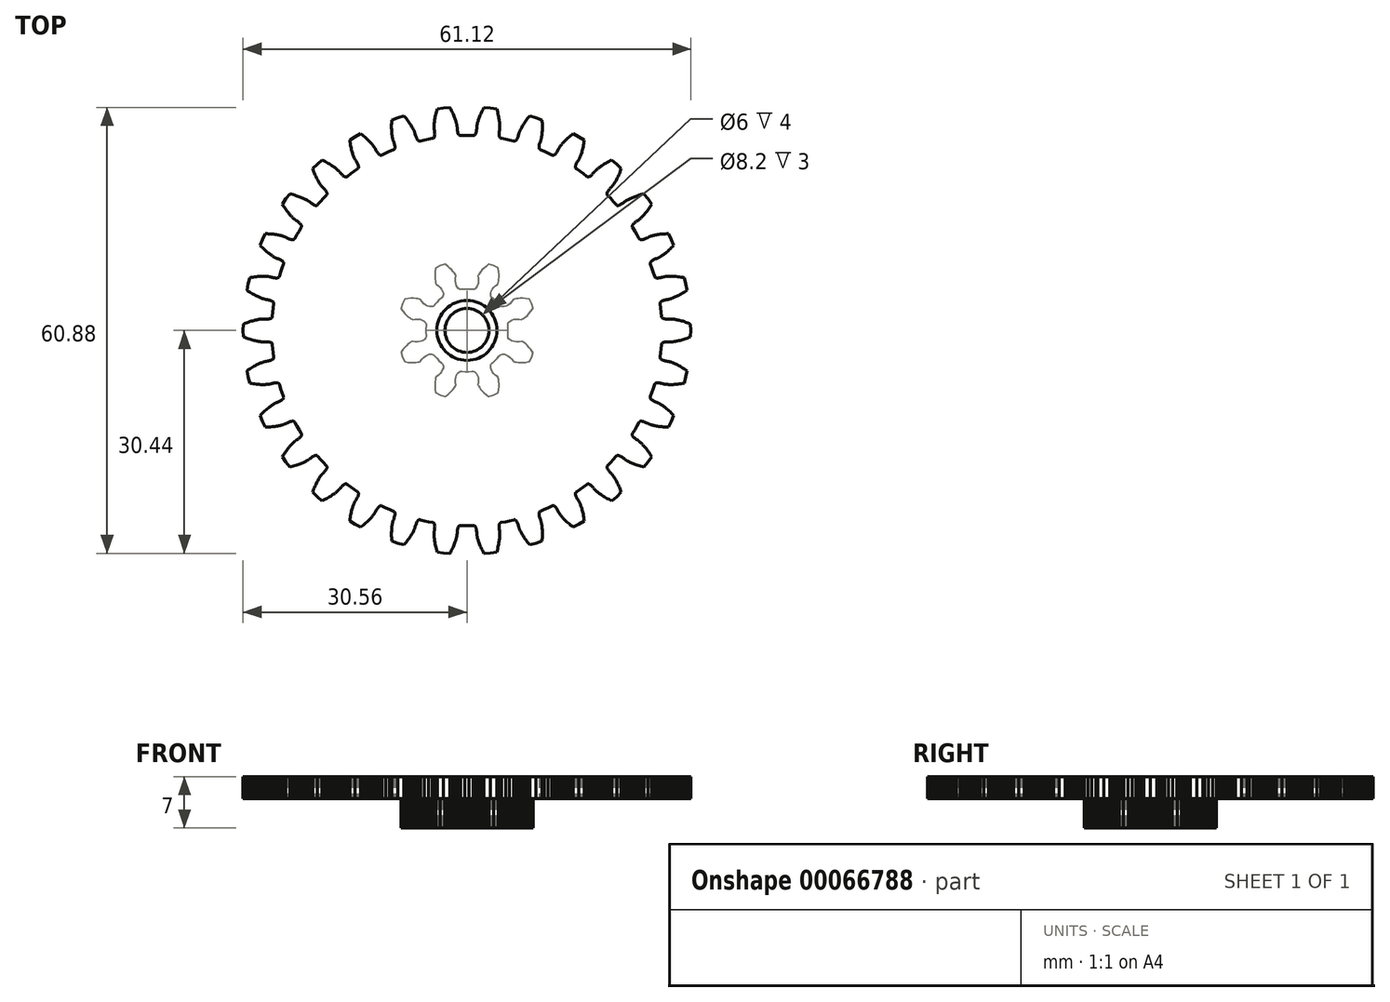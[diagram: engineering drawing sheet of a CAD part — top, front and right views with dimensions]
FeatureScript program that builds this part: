
annotation { "Feature Type Name" : "Feature", "Feature Type Description" : "" }
export const myFeature = defineFeature(function(context is Context, id is Id, definition is map)
    precondition{}
    {
        {
            var Q0;
            Q0=qCreatedBy(makeId("Top.planeOp"),FACE);
            var sketch = newSketch(context, id + "F0", { "sketchPlane" : qUnion([Q0])});
            skCircle(sketch, "E0", {"center": v(0, 0) * mm, "radius": 3 * mm});
            skLineSegment(sketch, "E1", {"start": v(-8.5, 4.26) * mm, "end": v(-8.82, 3.65) * mm});
            skLineSegment(sketch, "E2", {"start": v(-8.82, 3.65) * mm, "end": v(-9.02, 3) * mm});
            skLineSegment(sketch, "E3", {"start": v(-9.02, 3) * mm, "end": v(-9, 2.97) * mm});
            skLineSegment(sketch, "E4", {"start": v(-9, 2.97) * mm, "end": v(-8.75, 2.6) * mm});
            skLineSegment(sketch, "E5", {"start": v(-8.75, 2.6) * mm, "end": v(-8.5, 2.3) * mm});
            skLineSegment(sketch, "E6", {"start": v(-8.5, 2.3) * mm, "end": v(-8.25, 2.06) * mm});
            skLineSegment(sketch, "E7", {"start": v(-8.25, 2.06) * mm, "end": v(-8.02, 1.86) * mm});
            skLineSegment(sketch, "E8", {"start": v(-8.02, 1.86) * mm, "end": v(-7.81, 1.7) * mm});
            skLineSegment(sketch, "E9", {"start": v(-7.81, 1.7) * mm, "end": v(-7.63, 1.59) * mm});
            skLineSegment(sketch, "E10", {"start": v(-7.63, 1.59) * mm, "end": v(-7.48, 1.51) * mm});
            skLineSegment(sketch, "E11", {"start": v(-7.48, 1.51) * mm, "end": v(-7.43, 1.5) * mm});
            skLineSegment(sketch, "E12", {"start": v(-7.43, 1.5) * mm, "end": v(-7.11, 1.56) * mm});
            skLineSegment(sketch, "E13", {"start": v(-7.11, 1.56) * mm, "end": v(-6.74, 1.56) * mm});
            skLineSegment(sketch, "E14", {"start": v(-6.74, 1.56) * mm, "end": v(-6.41, 1.52) * mm});
            skLineSegment(sketch, "E15", {"start": v(-6.41, 1.52) * mm, "end": v(-6.13, 1.43) * mm});
            skLineSegment(sketch, "E16", {"start": v(-6.13, 1.43) * mm, "end": v(-5.9, 1.31) * mm});
            skLineSegment(sketch, "E17", {"start": v(-5.9, 1.31) * mm, "end": v(-5.74, 1.18) * mm});
            skLineSegment(sketch, "E18", {"start": v(-5.74, 1.18) * mm, "end": v(-5.63, 1.02) * mm});
            skLineSegment(sketch, "E19", {"start": v(-5.63, 1.02) * mm, "end": v(-5.58, 0.86) * mm});
            skLineSegment(sketch, "E20", {"start": v(-5.58, 0.86) * mm, "end": v(-5.59, 0.7) * mm});
            skLineSegment(sketch, "E21", {"start": v(-5.59, 0.7) * mm, "end": v(-5.6, 0.66) * mm});
            skLineSegment(sketch, "E22", {"start": v(-5.6, 0.66) * mm, "end": v(-5.63, 0.22) * mm});
            skLineSegment(sketch, "E23", {"start": v(-5.63, 0.22) * mm, "end": v(-5.63, -0.22) * mm});
            skLineSegment(sketch, "E24", {"start": v(-5.63, -0.22) * mm, "end": v(-5.6, -0.66) * mm});
            skLineSegment(sketch, "E25", {"start": v(-5.6, -0.66) * mm, "end": v(-5.59, -0.7) * mm});
            skLineSegment(sketch, "E26", {"start": v(-5.59, -0.7) * mm, "end": v(-5.58, -0.86) * mm});
            skLineSegment(sketch, "E27", {"start": v(-5.58, -0.86) * mm, "end": v(-5.63, -1.02) * mm});
            skLineSegment(sketch, "E28", {"start": v(-5.63, -1.02) * mm, "end": v(-5.74, -1.18) * mm});
            skLineSegment(sketch, "E29", {"start": v(-5.74, -1.18) * mm, "end": v(-5.9, -1.31) * mm});
            skLineSegment(sketch, "E30", {"start": v(-5.9, -1.31) * mm, "end": v(-6.13, -1.43) * mm});
            skLineSegment(sketch, "E31", {"start": v(-6.13, -1.43) * mm, "end": v(-6.41, -1.52) * mm});
            skLineSegment(sketch, "E32", {"start": v(-6.41, -1.52) * mm, "end": v(-6.74, -1.56) * mm});
            skLineSegment(sketch, "E33", {"start": v(-6.74, -1.56) * mm, "end": v(-7.11, -1.56) * mm});
            skLineSegment(sketch, "E34", {"start": v(-7.11, -1.56) * mm, "end": v(-7.43, -1.5) * mm});
            skLineSegment(sketch, "E35", {"start": v(-7.43, -1.5) * mm, "end": v(-7.48, -1.51) * mm});
            skLineSegment(sketch, "E36", {"start": v(-7.48, -1.51) * mm, "end": v(-7.63, -1.59) * mm});
            skLineSegment(sketch, "E37", {"start": v(-7.63, -1.59) * mm, "end": v(-7.81, -1.7) * mm});
            skLineSegment(sketch, "E38", {"start": v(-7.81, -1.7) * mm, "end": v(-8.02, -1.86) * mm});
            skLineSegment(sketch, "E39", {"start": v(-8.02, -1.86) * mm, "end": v(-8.25, -2.06) * mm});
            skLineSegment(sketch, "E40", {"start": v(-8.25, -2.06) * mm, "end": v(-8.5, -2.3) * mm});
            skLineSegment(sketch, "E41", {"start": v(-8.5, -2.3) * mm, "end": v(-8.75, -2.6) * mm});
            skLineSegment(sketch, "E42", {"start": v(-8.75, -2.6) * mm, "end": v(-9, -2.97) * mm});
            skLineSegment(sketch, "E43", {"start": v(-9, -2.97) * mm, "end": v(-9.02, -3) * mm});
            skLineSegment(sketch, "E44", {"start": v(-9.02, -3) * mm, "end": v(-8.82, -3.65) * mm});
            skLineSegment(sketch, "E45", {"start": v(-8.82, -3.65) * mm, "end": v(-8.5, -4.26) * mm});
            skLineSegment(sketch, "E46", {"start": v(-8.5, -4.26) * mm, "end": v(-8.46, -4.27) * mm});
            skLineSegment(sketch, "E47", {"start": v(-8.46, -4.27) * mm, "end": v(-8.03, -4.34) * mm});
            skLineSegment(sketch, "E48", {"start": v(-8.03, -4.34) * mm, "end": v(-7.64, -4.38) * mm});
            skLineSegment(sketch, "E49", {"start": v(-7.64, -4.38) * mm, "end": v(-7.29, -4.38) * mm});
            skLineSegment(sketch, "E50", {"start": v(-7.29, -4.38) * mm, "end": v(-6.98, -4.36) * mm});
            skLineSegment(sketch, "E51", {"start": v(-6.98, -4.36) * mm, "end": v(-6.73, -4.32) * mm});
            skLineSegment(sketch, "E52", {"start": v(-6.73, -4.32) * mm, "end": v(-6.52, -4.27) * mm});
            skLineSegment(sketch, "E53", {"start": v(-6.52, -4.27) * mm, "end": v(-6.36, -4.22) * mm});
            skLineSegment(sketch, "E54", {"start": v(-6.36, -4.22) * mm, "end": v(-6.3, -4.2) * mm});
            skLineSegment(sketch, "E55", {"start": v(-6.3, -4.2) * mm, "end": v(-6.14, -3.93) * mm});
            skLineSegment(sketch, "E56", {"start": v(-6.14, -3.93) * mm, "end": v(-5.87, -3.66) * mm});
            skLineSegment(sketch, "E57", {"start": v(-5.87, -3.66) * mm, "end": v(-5.6, -3.46) * mm});
            skLineSegment(sketch, "E58", {"start": v(-5.6, -3.46) * mm, "end": v(-5.35, -3.33) * mm});
            skLineSegment(sketch, "E59", {"start": v(-5.35, -3.33) * mm, "end": v(-5.1, -3.25) * mm});
            skLineSegment(sketch, "E60", {"start": v(-5.1, -3.25) * mm, "end": v(-4.89, -3.23) * mm});
            skLineSegment(sketch, "E61", {"start": v(-4.89, -3.23) * mm, "end": v(-4.7, -3.26) * mm});
            skLineSegment(sketch, "E62", {"start": v(-4.7, -3.26) * mm, "end": v(-4.56, -3.33) * mm});
            skLineSegment(sketch, "E63", {"start": v(-4.56, -3.33) * mm, "end": v(-4.45, -3.45) * mm});
            skLineSegment(sketch, "E64", {"start": v(-4.45, -3.45) * mm, "end": v(-4.42, -3.49) * mm});
            skLineSegment(sketch, "E65", {"start": v(-4.42, -3.49) * mm, "end": v(-4.14, -3.82) * mm});
            skLineSegment(sketch, "E66", {"start": v(-4.14, -3.82) * mm, "end": v(-3.82, -4.14) * mm});
            skLineSegment(sketch, "E67", {"start": v(-3.82, -4.14) * mm, "end": v(-3.49, -4.42) * mm});
            skLineSegment(sketch, "E68", {"start": v(-3.49, -4.42) * mm, "end": v(-3.45, -4.45) * mm});
            skLineSegment(sketch, "E69", {"start": v(-3.45, -4.45) * mm, "end": v(-3.33, -4.56) * mm});
            skLineSegment(sketch, "E70", {"start": v(-3.33, -4.56) * mm, "end": v(-3.26, -4.7) * mm});
            skLineSegment(sketch, "E71", {"start": v(-3.26, -4.7) * mm, "end": v(-3.23, -4.89) * mm});
            skLineSegment(sketch, "E72", {"start": v(-3.23, -4.89) * mm, "end": v(-3.25, -5.1) * mm});
            skLineSegment(sketch, "E73", {"start": v(-3.25, -5.1) * mm, "end": v(-3.33, -5.35) * mm});
            skLineSegment(sketch, "E74", {"start": v(-3.33, -5.35) * mm, "end": v(-3.46, -5.6) * mm});
            skLineSegment(sketch, "E75", {"start": v(-3.46, -5.6) * mm, "end": v(-3.66, -5.87) * mm});
            skLineSegment(sketch, "E76", {"start": v(-3.66, -5.87) * mm, "end": v(-3.93, -6.14) * mm});
            skLineSegment(sketch, "E77", {"start": v(-3.93, -6.14) * mm, "end": v(-4.2, -6.3) * mm});
            skLineSegment(sketch, "E78", {"start": v(-4.2, -6.3) * mm, "end": v(-4.22, -6.36) * mm});
            skLineSegment(sketch, "E79", {"start": v(-4.22, -6.36) * mm, "end": v(-4.27, -6.52) * mm});
            skLineSegment(sketch, "E80", {"start": v(-4.27, -6.52) * mm, "end": v(-4.32, -6.73) * mm});
            skLineSegment(sketch, "E81", {"start": v(-4.32, -6.73) * mm, "end": v(-4.36, -6.98) * mm});
            skLineSegment(sketch, "E82", {"start": v(-4.36, -6.98) * mm, "end": v(-4.38, -7.29) * mm});
            skLineSegment(sketch, "E83", {"start": v(-4.38, -7.29) * mm, "end": v(-4.38, -7.64) * mm});
            skLineSegment(sketch, "E84", {"start": v(-4.38, -7.64) * mm, "end": v(-4.34, -8.03) * mm});
            skLineSegment(sketch, "E85", {"start": v(-4.34, -8.03) * mm, "end": v(-4.27, -8.46) * mm});
            skLineSegment(sketch, "E86", {"start": v(-4.27, -8.46) * mm, "end": v(-4.26, -8.5) * mm});
            skLineSegment(sketch, "E87", {"start": v(-4.26, -8.5) * mm, "end": v(-3.65, -8.82) * mm});
            skLineSegment(sketch, "E88", {"start": v(-3.65, -8.82) * mm, "end": v(-3, -9.02) * mm});
            skLineSegment(sketch, "E89", {"start": v(-3, -9.02) * mm, "end": v(-2.97, -9) * mm});
            skLineSegment(sketch, "E90", {"start": v(-2.97, -9) * mm, "end": v(-2.6, -8.75) * mm});
            skLineSegment(sketch, "E91", {"start": v(-2.6, -8.75) * mm, "end": v(-2.3, -8.5) * mm});
            skLineSegment(sketch, "E92", {"start": v(-2.3, -8.5) * mm, "end": v(-2.06, -8.25) * mm});
            skLineSegment(sketch, "E93", {"start": v(-2.06, -8.25) * mm, "end": v(-1.86, -8.02) * mm});
            skLineSegment(sketch, "E94", {"start": v(-1.86, -8.02) * mm, "end": v(-1.7, -7.81) * mm});
            skLineSegment(sketch, "E95", {"start": v(-1.7, -7.81) * mm, "end": v(-1.59, -7.63) * mm});
            skLineSegment(sketch, "E96", {"start": v(-1.59, -7.63) * mm, "end": v(-1.51, -7.48) * mm});
            skLineSegment(sketch, "E97", {"start": v(-1.51, -7.48) * mm, "end": v(-1.5, -7.43) * mm});
            skLineSegment(sketch, "E98", {"start": v(-1.5, -7.43) * mm, "end": v(-1.56, -7.11) * mm});
            skLineSegment(sketch, "E99", {"start": v(-1.56, -7.11) * mm, "end": v(-1.56, -6.74) * mm});
            skLineSegment(sketch, "E100", {"start": v(-1.56, -6.74) * mm, "end": v(-1.52, -6.41) * mm});
            skLineSegment(sketch, "E101", {"start": v(-1.52, -6.41) * mm, "end": v(-1.43, -6.13) * mm});
            skLineSegment(sketch, "E102", {"start": v(-1.43, -6.13) * mm, "end": v(-1.31, -5.9) * mm});
            skLineSegment(sketch, "E103", {"start": v(-1.31, -5.9) * mm, "end": v(-1.18, -5.74) * mm});
            skLineSegment(sketch, "E104", {"start": v(-1.18, -5.74) * mm, "end": v(-1.02, -5.63) * mm});
            skLineSegment(sketch, "E105", {"start": v(-1.02, -5.63) * mm, "end": v(-0.86, -5.58) * mm});
            skLineSegment(sketch, "E106", {"start": v(-0.86, -5.58) * mm, "end": v(-0.7, -5.59) * mm});
            skLineSegment(sketch, "E107", {"start": v(-0.7, -5.59) * mm, "end": v(-0.66, -5.6) * mm});
            skLineSegment(sketch, "E108", {"start": v(-0.66, -5.6) * mm, "end": v(-0.22, -5.63) * mm});
            skLineSegment(sketch, "E109", {"start": v(-0.22, -5.63) * mm, "end": v(0.22, -5.63) * mm});
            skLineSegment(sketch, "E110", {"start": v(0.22, -5.63) * mm, "end": v(0.66, -5.6) * mm});
            skLineSegment(sketch, "E111", {"start": v(0.66, -5.6) * mm, "end": v(0.7, -5.59) * mm});
            skLineSegment(sketch, "E112", {"start": v(0.7, -5.59) * mm, "end": v(0.86, -5.58) * mm});
            skLineSegment(sketch, "E113", {"start": v(0.86, -5.58) * mm, "end": v(1.02, -5.63) * mm});
            skLineSegment(sketch, "E114", {"start": v(1.02, -5.63) * mm, "end": v(1.18, -5.74) * mm});
            skLineSegment(sketch, "E115", {"start": v(1.18, -5.74) * mm, "end": v(1.31, -5.9) * mm});
            skLineSegment(sketch, "E116", {"start": v(1.31, -5.9) * mm, "end": v(1.43, -6.13) * mm});
            skLineSegment(sketch, "E117", {"start": v(1.43, -6.13) * mm, "end": v(1.52, -6.41) * mm});
            skLineSegment(sketch, "E118", {"start": v(1.52, -6.41) * mm, "end": v(1.56, -6.74) * mm});
            skLineSegment(sketch, "E119", {"start": v(1.56, -6.74) * mm, "end": v(1.56, -7.11) * mm});
            skLineSegment(sketch, "E120", {"start": v(1.56, -7.11) * mm, "end": v(1.5, -7.43) * mm});
            skLineSegment(sketch, "E121", {"start": v(1.5, -7.43) * mm, "end": v(1.51, -7.48) * mm});
            skLineSegment(sketch, "E122", {"start": v(1.51, -7.48) * mm, "end": v(1.59, -7.63) * mm});
            skLineSegment(sketch, "E123", {"start": v(1.59, -7.63) * mm, "end": v(1.7, -7.81) * mm});
            skLineSegment(sketch, "E124", {"start": v(1.7, -7.81) * mm, "end": v(1.86, -8.02) * mm});
            skLineSegment(sketch, "E125", {"start": v(1.86, -8.02) * mm, "end": v(2.06, -8.25) * mm});
            skLineSegment(sketch, "E126", {"start": v(2.06, -8.25) * mm, "end": v(2.3, -8.5) * mm});
            skLineSegment(sketch, "E127", {"start": v(2.3, -8.5) * mm, "end": v(2.6, -8.75) * mm});
            skLineSegment(sketch, "E128", {"start": v(2.6, -8.75) * mm, "end": v(2.97, -9) * mm});
            skLineSegment(sketch, "E129", {"start": v(2.97, -9) * mm, "end": v(3, -9.02) * mm});
            skLineSegment(sketch, "E130", {"start": v(3, -9.02) * mm, "end": v(3.65, -8.82) * mm});
            skLineSegment(sketch, "E131", {"start": v(3.65, -8.82) * mm, "end": v(4.26, -8.5) * mm});
            skLineSegment(sketch, "E132", {"start": v(4.26, -8.5) * mm, "end": v(4.27, -8.46) * mm});
            skLineSegment(sketch, "E133", {"start": v(4.27, -8.46) * mm, "end": v(4.34, -8.03) * mm});
            skLineSegment(sketch, "E134", {"start": v(4.34, -8.03) * mm, "end": v(4.38, -7.64) * mm});
            skLineSegment(sketch, "E135", {"start": v(4.38, -7.64) * mm, "end": v(4.38, -7.29) * mm});
            skLineSegment(sketch, "E136", {"start": v(4.38, -7.29) * mm, "end": v(4.36, -6.98) * mm});
            skLineSegment(sketch, "E137", {"start": v(4.36, -6.98) * mm, "end": v(4.32, -6.73) * mm});
            skLineSegment(sketch, "E138", {"start": v(4.32, -6.73) * mm, "end": v(4.27, -6.52) * mm});
            skLineSegment(sketch, "E139", {"start": v(4.27, -6.52) * mm, "end": v(4.22, -6.36) * mm});
            skLineSegment(sketch, "E140", {"start": v(4.22, -6.36) * mm, "end": v(4.2, -6.3) * mm});
            skLineSegment(sketch, "E141", {"start": v(4.2, -6.3) * mm, "end": v(3.93, -6.14) * mm});
            skLineSegment(sketch, "E142", {"start": v(3.93, -6.14) * mm, "end": v(3.66, -5.87) * mm});
            skLineSegment(sketch, "E143", {"start": v(3.66, -5.87) * mm, "end": v(3.46, -5.6) * mm});
            skLineSegment(sketch, "E144", {"start": v(3.46, -5.6) * mm, "end": v(3.33, -5.35) * mm});
            skLineSegment(sketch, "E145", {"start": v(3.33, -5.35) * mm, "end": v(3.25, -5.1) * mm});
            skLineSegment(sketch, "E146", {"start": v(3.25, -5.1) * mm, "end": v(3.23, -4.89) * mm});
            skLineSegment(sketch, "E147", {"start": v(3.23, -4.89) * mm, "end": v(3.26, -4.7) * mm});
            skLineSegment(sketch, "E148", {"start": v(3.26, -4.7) * mm, "end": v(3.33, -4.56) * mm});
            skLineSegment(sketch, "E149", {"start": v(3.33, -4.56) * mm, "end": v(3.45, -4.45) * mm});
            skLineSegment(sketch, "E150", {"start": v(3.45, -4.45) * mm, "end": v(3.49, -4.42) * mm});
            skLineSegment(sketch, "E151", {"start": v(3.49, -4.42) * mm, "end": v(3.82, -4.14) * mm});
            skLineSegment(sketch, "E152", {"start": v(3.82, -4.14) * mm, "end": v(4.14, -3.82) * mm});
            skLineSegment(sketch, "E153", {"start": v(4.14, -3.82) * mm, "end": v(4.42, -3.49) * mm});
            skLineSegment(sketch, "E154", {"start": v(4.42, -3.49) * mm, "end": v(4.45, -3.45) * mm});
            skLineSegment(sketch, "E155", {"start": v(4.45, -3.45) * mm, "end": v(4.56, -3.33) * mm});
            skLineSegment(sketch, "E156", {"start": v(4.56, -3.33) * mm, "end": v(4.7, -3.26) * mm});
            skLineSegment(sketch, "E157", {"start": v(4.7, -3.26) * mm, "end": v(4.89, -3.23) * mm});
            skLineSegment(sketch, "E158", {"start": v(4.89, -3.23) * mm, "end": v(5.1, -3.25) * mm});
            skLineSegment(sketch, "E159", {"start": v(5.1, -3.25) * mm, "end": v(5.35, -3.33) * mm});
            skLineSegment(sketch, "E160", {"start": v(5.35, -3.33) * mm, "end": v(5.6, -3.46) * mm});
            skLineSegment(sketch, "E161", {"start": v(5.6, -3.46) * mm, "end": v(5.87, -3.66) * mm});
            skLineSegment(sketch, "E162", {"start": v(5.87, -3.66) * mm, "end": v(6.14, -3.93) * mm});
            skLineSegment(sketch, "E163", {"start": v(6.14, -3.93) * mm, "end": v(6.3, -4.2) * mm});
            skLineSegment(sketch, "E164", {"start": v(6.3, -4.2) * mm, "end": v(6.36, -4.22) * mm});
            skLineSegment(sketch, "E165", {"start": v(6.36, -4.22) * mm, "end": v(6.52, -4.27) * mm});
            skLineSegment(sketch, "E166", {"start": v(6.52, -4.27) * mm, "end": v(6.73, -4.32) * mm});
            skLineSegment(sketch, "E167", {"start": v(6.73, -4.32) * mm, "end": v(6.98, -4.36) * mm});
            skLineSegment(sketch, "E168", {"start": v(6.98, -4.36) * mm, "end": v(7.29, -4.38) * mm});
            skLineSegment(sketch, "E169", {"start": v(7.29, -4.38) * mm, "end": v(7.64, -4.38) * mm});
            skLineSegment(sketch, "E170", {"start": v(7.64, -4.38) * mm, "end": v(8.03, -4.34) * mm});
            skLineSegment(sketch, "E171", {"start": v(8.03, -4.34) * mm, "end": v(8.46, -4.27) * mm});
            skLineSegment(sketch, "E172", {"start": v(8.46, -4.27) * mm, "end": v(8.5, -4.26) * mm});
            skLineSegment(sketch, "E173", {"start": v(8.5, -4.26) * mm, "end": v(8.82, -3.65) * mm});
            skLineSegment(sketch, "E174", {"start": v(8.82, -3.65) * mm, "end": v(9.02, -3) * mm});
            skLineSegment(sketch, "E175", {"start": v(9.02, -3) * mm, "end": v(9, -2.97) * mm});
            skLineSegment(sketch, "E176", {"start": v(9, -2.97) * mm, "end": v(8.75, -2.6) * mm});
            skLineSegment(sketch, "E177", {"start": v(8.75, -2.6) * mm, "end": v(8.5, -2.3) * mm});
            skLineSegment(sketch, "E178", {"start": v(8.5, -2.3) * mm, "end": v(8.25, -2.06) * mm});
            skLineSegment(sketch, "E179", {"start": v(8.25, -2.06) * mm, "end": v(8.02, -1.86) * mm});
            skLineSegment(sketch, "E180", {"start": v(8.02, -1.86) * mm, "end": v(7.81, -1.7) * mm});
            skLineSegment(sketch, "E181", {"start": v(7.81, -1.7) * mm, "end": v(7.63, -1.59) * mm});
            skLineSegment(sketch, "E182", {"start": v(7.63, -1.59) * mm, "end": v(7.48, -1.51) * mm});
            skLineSegment(sketch, "E183", {"start": v(7.48, -1.51) * mm, "end": v(7.43, -1.5) * mm});
            skLineSegment(sketch, "E184", {"start": v(7.43, -1.5) * mm, "end": v(7.11, -1.56) * mm});
            skLineSegment(sketch, "E185", {"start": v(7.11, -1.56) * mm, "end": v(6.74, -1.56) * mm});
            skLineSegment(sketch, "E186", {"start": v(6.74, -1.56) * mm, "end": v(6.41, -1.52) * mm});
            skLineSegment(sketch, "E187", {"start": v(6.41, -1.52) * mm, "end": v(6.13, -1.43) * mm});
            skLineSegment(sketch, "E188", {"start": v(6.13, -1.43) * mm, "end": v(5.9, -1.31) * mm});
            skLineSegment(sketch, "E189", {"start": v(5.9, -1.31) * mm, "end": v(5.74, -1.18) * mm});
            skLineSegment(sketch, "E190", {"start": v(5.74, -1.18) * mm, "end": v(5.63, -1.02) * mm});
            skLineSegment(sketch, "E191", {"start": v(5.63, -1.02) * mm, "end": v(5.58, -0.86) * mm});
            skLineSegment(sketch, "E192", {"start": v(5.58, -0.86) * mm, "end": v(5.59, -0.7) * mm});
            skLineSegment(sketch, "E193", {"start": v(5.59, -0.7) * mm, "end": v(5.6, -0.66) * mm});
            skLineSegment(sketch, "E194", {"start": v(5.6, -0.66) * mm, "end": v(5.63, -0.22) * mm});
            skLineSegment(sketch, "E195", {"start": v(5.63, -0.22) * mm, "end": v(5.63, 0.22) * mm});
            skLineSegment(sketch, "E196", {"start": v(5.63, 0.22) * mm, "end": v(5.6, 0.66) * mm});
            skLineSegment(sketch, "E197", {"start": v(5.6, 0.66) * mm, "end": v(5.59, 0.7) * mm});
            skLineSegment(sketch, "E198", {"start": v(5.59, 0.7) * mm, "end": v(5.58, 0.86) * mm});
            skLineSegment(sketch, "E199", {"start": v(5.58, 0.86) * mm, "end": v(5.63, 1.02) * mm});
            skLineSegment(sketch, "E200", {"start": v(5.63, 1.02) * mm, "end": v(5.74, 1.18) * mm});
            skLineSegment(sketch, "E201", {"start": v(5.74, 1.18) * mm, "end": v(5.9, 1.31) * mm});
            skLineSegment(sketch, "E202", {"start": v(5.9, 1.31) * mm, "end": v(6.13, 1.43) * mm});
            skLineSegment(sketch, "E203", {"start": v(6.13, 1.43) * mm, "end": v(6.41, 1.52) * mm});
            skLineSegment(sketch, "E204", {"start": v(6.41, 1.52) * mm, "end": v(6.74, 1.56) * mm});
            skLineSegment(sketch, "E205", {"start": v(6.74, 1.56) * mm, "end": v(7.11, 1.56) * mm});
            skLineSegment(sketch, "E206", {"start": v(7.11, 1.56) * mm, "end": v(7.43, 1.5) * mm});
            skLineSegment(sketch, "E207", {"start": v(7.43, 1.5) * mm, "end": v(7.48, 1.51) * mm});
            skLineSegment(sketch, "E208", {"start": v(7.48, 1.51) * mm, "end": v(7.63, 1.59) * mm});
            skLineSegment(sketch, "E209", {"start": v(7.63, 1.59) * mm, "end": v(7.81, 1.7) * mm});
            skLineSegment(sketch, "E210", {"start": v(7.81, 1.7) * mm, "end": v(8.02, 1.86) * mm});
            skLineSegment(sketch, "E211", {"start": v(8.02, 1.86) * mm, "end": v(8.25, 2.06) * mm});
            skLineSegment(sketch, "E212", {"start": v(8.25, 2.06) * mm, "end": v(8.5, 2.3) * mm});
            skLineSegment(sketch, "E213", {"start": v(8.5, 2.3) * mm, "end": v(8.75, 2.6) * mm});
            skLineSegment(sketch, "E214", {"start": v(8.75, 2.6) * mm, "end": v(9, 2.97) * mm});
            skLineSegment(sketch, "E215", {"start": v(9, 2.97) * mm, "end": v(9.02, 3) * mm});
            skLineSegment(sketch, "E216", {"start": v(9.02, 3) * mm, "end": v(8.82, 3.65) * mm});
            skLineSegment(sketch, "E217", {"start": v(8.82, 3.65) * mm, "end": v(8.5, 4.26) * mm});
            skLineSegment(sketch, "E218", {"start": v(8.5, 4.26) * mm, "end": v(8.46, 4.27) * mm});
            skLineSegment(sketch, "E219", {"start": v(8.46, 4.27) * mm, "end": v(8.03, 4.34) * mm});
            skLineSegment(sketch, "E220", {"start": v(8.03, 4.34) * mm, "end": v(7.64, 4.38) * mm});
            skLineSegment(sketch, "E221", {"start": v(7.64, 4.38) * mm, "end": v(7.29, 4.38) * mm});
            skLineSegment(sketch, "E222", {"start": v(7.29, 4.38) * mm, "end": v(6.98, 4.36) * mm});
            skLineSegment(sketch, "E223", {"start": v(6.98, 4.36) * mm, "end": v(6.73, 4.32) * mm});
            skLineSegment(sketch, "E224", {"start": v(6.73, 4.32) * mm, "end": v(6.52, 4.27) * mm});
            skLineSegment(sketch, "E225", {"start": v(6.52, 4.27) * mm, "end": v(6.36, 4.22) * mm});
            skLineSegment(sketch, "E226", {"start": v(6.36, 4.22) * mm, "end": v(6.3, 4.2) * mm});
            skLineSegment(sketch, "E227", {"start": v(6.3, 4.2) * mm, "end": v(6.14, 3.93) * mm});
            skLineSegment(sketch, "E228", {"start": v(6.14, 3.93) * mm, "end": v(5.87, 3.66) * mm});
            skLineSegment(sketch, "E229", {"start": v(5.87, 3.66) * mm, "end": v(5.6, 3.46) * mm});
            skLineSegment(sketch, "E230", {"start": v(5.6, 3.46) * mm, "end": v(5.35, 3.33) * mm});
            skLineSegment(sketch, "E231", {"start": v(5.35, 3.33) * mm, "end": v(5.1, 3.25) * mm});
            skLineSegment(sketch, "E232", {"start": v(5.1, 3.25) * mm, "end": v(4.89, 3.23) * mm});
            skLineSegment(sketch, "E233", {"start": v(4.89, 3.23) * mm, "end": v(4.7, 3.26) * mm});
            skLineSegment(sketch, "E234", {"start": v(4.7, 3.26) * mm, "end": v(4.56, 3.33) * mm});
            skLineSegment(sketch, "E235", {"start": v(4.56, 3.33) * mm, "end": v(4.45, 3.45) * mm});
            skLineSegment(sketch, "E236", {"start": v(4.45, 3.45) * mm, "end": v(4.42, 3.49) * mm});
            skLineSegment(sketch, "E237", {"start": v(4.42, 3.49) * mm, "end": v(4.14, 3.82) * mm});
            skLineSegment(sketch, "E238", {"start": v(4.14, 3.82) * mm, "end": v(3.82, 4.14) * mm});
            skLineSegment(sketch, "E239", {"start": v(3.82, 4.14) * mm, "end": v(3.49, 4.42) * mm});
            skLineSegment(sketch, "E240", {"start": v(3.49, 4.42) * mm, "end": v(3.45, 4.45) * mm});
            skLineSegment(sketch, "E241", {"start": v(3.45, 4.45) * mm, "end": v(3.33, 4.56) * mm});
            skLineSegment(sketch, "E242", {"start": v(3.33, 4.56) * mm, "end": v(3.26, 4.7) * mm});
            skLineSegment(sketch, "E243", {"start": v(3.26, 4.7) * mm, "end": v(3.23, 4.89) * mm});
            skLineSegment(sketch, "E244", {"start": v(3.23, 4.89) * mm, "end": v(3.25, 5.1) * mm});
            skLineSegment(sketch, "E245", {"start": v(3.25, 5.1) * mm, "end": v(3.33, 5.35) * mm});
            skLineSegment(sketch, "E246", {"start": v(3.33, 5.35) * mm, "end": v(3.46, 5.6) * mm});
            skLineSegment(sketch, "E247", {"start": v(3.46, 5.6) * mm, "end": v(3.66, 5.87) * mm});
            skLineSegment(sketch, "E248", {"start": v(3.66, 5.87) * mm, "end": v(3.93, 6.14) * mm});
            skLineSegment(sketch, "E249", {"start": v(3.93, 6.14) * mm, "end": v(4.2, 6.3) * mm});
            skLineSegment(sketch, "E250", {"start": v(4.2, 6.3) * mm, "end": v(4.22, 6.36) * mm});
            skLineSegment(sketch, "E251", {"start": v(4.22, 6.36) * mm, "end": v(4.27, 6.52) * mm});
            skLineSegment(sketch, "E252", {"start": v(4.27, 6.52) * mm, "end": v(4.32, 6.73) * mm});
            skLineSegment(sketch, "E253", {"start": v(4.32, 6.73) * mm, "end": v(4.36, 6.98) * mm});
            skLineSegment(sketch, "E254", {"start": v(4.36, 6.98) * mm, "end": v(4.38, 7.29) * mm});
            skLineSegment(sketch, "E255", {"start": v(4.38, 7.29) * mm, "end": v(4.38, 7.64) * mm});
            skLineSegment(sketch, "E256", {"start": v(4.38, 7.64) * mm, "end": v(4.34, 8.03) * mm});
            skLineSegment(sketch, "E257", {"start": v(4.34, 8.03) * mm, "end": v(4.27, 8.46) * mm});
            skLineSegment(sketch, "E258", {"start": v(4.27, 8.46) * mm, "end": v(4.26, 8.5) * mm});
            skLineSegment(sketch, "E259", {"start": v(4.26, 8.5) * mm, "end": v(3.65, 8.82) * mm});
            skLineSegment(sketch, "E260", {"start": v(3.65, 8.82) * mm, "end": v(3, 9.02) * mm});
            skLineSegment(sketch, "E261", {"start": v(3, 9.02) * mm, "end": v(2.97, 9) * mm});
            skLineSegment(sketch, "E262", {"start": v(2.97, 9) * mm, "end": v(2.6, 8.75) * mm});
            skLineSegment(sketch, "E263", {"start": v(2.6, 8.75) * mm, "end": v(2.3, 8.5) * mm});
            skLineSegment(sketch, "E264", {"start": v(2.3, 8.5) * mm, "end": v(2.06, 8.25) * mm});
            skLineSegment(sketch, "E265", {"start": v(2.06, 8.25) * mm, "end": v(1.86, 8.02) * mm});
            skLineSegment(sketch, "E266", {"start": v(1.86, 8.02) * mm, "end": v(1.7, 7.81) * mm});
            skLineSegment(sketch, "E267", {"start": v(1.7, 7.81) * mm, "end": v(1.59, 7.63) * mm});
            skLineSegment(sketch, "E268", {"start": v(1.59, 7.63) * mm, "end": v(1.51, 7.48) * mm});
            skLineSegment(sketch, "E269", {"start": v(1.51, 7.48) * mm, "end": v(1.5, 7.43) * mm});
            skLineSegment(sketch, "E270", {"start": v(1.5, 7.43) * mm, "end": v(1.56, 7.11) * mm});
            skLineSegment(sketch, "E271", {"start": v(1.56, 7.11) * mm, "end": v(1.56, 6.74) * mm});
            skLineSegment(sketch, "E272", {"start": v(1.56, 6.74) * mm, "end": v(1.52, 6.41) * mm});
            skLineSegment(sketch, "E273", {"start": v(1.52, 6.41) * mm, "end": v(1.43, 6.13) * mm});
            skLineSegment(sketch, "E274", {"start": v(1.43, 6.13) * mm, "end": v(1.31, 5.9) * mm});
            skLineSegment(sketch, "E275", {"start": v(1.31, 5.9) * mm, "end": v(1.18, 5.74) * mm});
            skLineSegment(sketch, "E276", {"start": v(1.18, 5.74) * mm, "end": v(1.02, 5.63) * mm});
            skLineSegment(sketch, "E277", {"start": v(1.02, 5.63) * mm, "end": v(0.86, 5.58) * mm});
            skLineSegment(sketch, "E278", {"start": v(0.86, 5.58) * mm, "end": v(0.7, 5.59) * mm});
            skLineSegment(sketch, "E279", {"start": v(0.7, 5.59) * mm, "end": v(0.66, 5.6) * mm});
            skLineSegment(sketch, "E280", {"start": v(0.66, 5.6) * mm, "end": v(0.22, 5.63) * mm});
            skLineSegment(sketch, "E281", {"start": v(0.22, 5.63) * mm, "end": v(-0.22, 5.63) * mm});
            skLineSegment(sketch, "E282", {"start": v(-0.22, 5.63) * mm, "end": v(-0.66, 5.6) * mm});
            skLineSegment(sketch, "E283", {"start": v(-0.66, 5.6) * mm, "end": v(-0.7, 5.59) * mm});
            skLineSegment(sketch, "E284", {"start": v(-0.7, 5.59) * mm, "end": v(-0.86, 5.58) * mm});
            skLineSegment(sketch, "E285", {"start": v(-0.86, 5.58) * mm, "end": v(-1.02, 5.63) * mm});
            skLineSegment(sketch, "E286", {"start": v(-1.02, 5.63) * mm, "end": v(-1.18, 5.74) * mm});
            skLineSegment(sketch, "E287", {"start": v(-1.18, 5.74) * mm, "end": v(-1.31, 5.9) * mm});
            skLineSegment(sketch, "E288", {"start": v(-1.31, 5.9) * mm, "end": v(-1.43, 6.13) * mm});
            skLineSegment(sketch, "E289", {"start": v(-1.43, 6.13) * mm, "end": v(-1.52, 6.41) * mm});
            skLineSegment(sketch, "E290", {"start": v(-1.52, 6.41) * mm, "end": v(-1.56, 6.74) * mm});
            skLineSegment(sketch, "E291", {"start": v(-1.56, 6.74) * mm, "end": v(-1.56, 7.11) * mm});
            skLineSegment(sketch, "E292", {"start": v(-1.56, 7.11) * mm, "end": v(-1.5, 7.43) * mm});
            skLineSegment(sketch, "E293", {"start": v(-1.5, 7.43) * mm, "end": v(-1.51, 7.48) * mm});
            skLineSegment(sketch, "E294", {"start": v(-1.51, 7.48) * mm, "end": v(-1.59, 7.63) * mm});
            skLineSegment(sketch, "E295", {"start": v(-1.59, 7.63) * mm, "end": v(-1.7, 7.81) * mm});
            skLineSegment(sketch, "E296", {"start": v(-1.7, 7.81) * mm, "end": v(-1.86, 8.02) * mm});
            skLineSegment(sketch, "E297", {"start": v(-1.86, 8.02) * mm, "end": v(-2.06, 8.25) * mm});
            skLineSegment(sketch, "E298", {"start": v(-2.06, 8.25) * mm, "end": v(-2.3, 8.5) * mm});
            skLineSegment(sketch, "E299", {"start": v(-2.3, 8.5) * mm, "end": v(-2.6, 8.75) * mm});
            skLineSegment(sketch, "E300", {"start": v(-2.6, 8.75) * mm, "end": v(-2.97, 9) * mm});
            skLineSegment(sketch, "E301", {"start": v(-2.97, 9) * mm, "end": v(-3, 9.02) * mm});
            skLineSegment(sketch, "E302", {"start": v(-3, 9.02) * mm, "end": v(-3.65, 8.82) * mm});
            skLineSegment(sketch, "E303", {"start": v(-3.65, 8.82) * mm, "end": v(-4.26, 8.5) * mm});
            skLineSegment(sketch, "E304", {"start": v(-4.26, 8.5) * mm, "end": v(-4.27, 8.46) * mm});
            skLineSegment(sketch, "E305", {"start": v(-4.27, 8.46) * mm, "end": v(-4.34, 8.03) * mm});
            skLineSegment(sketch, "E306", {"start": v(-4.34, 8.03) * mm, "end": v(-4.38, 7.64) * mm});
            skLineSegment(sketch, "E307", {"start": v(-4.38, 7.64) * mm, "end": v(-4.38, 7.29) * mm});
            skLineSegment(sketch, "E308", {"start": v(-4.38, 7.29) * mm, "end": v(-4.36, 6.98) * mm});
            skLineSegment(sketch, "E309", {"start": v(-4.36, 6.98) * mm, "end": v(-4.32, 6.73) * mm});
            skLineSegment(sketch, "E310", {"start": v(-4.32, 6.73) * mm, "end": v(-4.27, 6.52) * mm});
            skLineSegment(sketch, "E311", {"start": v(-4.27, 6.52) * mm, "end": v(-4.22, 6.36) * mm});
            skLineSegment(sketch, "E312", {"start": v(-4.22, 6.36) * mm, "end": v(-4.2, 6.3) * mm});
            skLineSegment(sketch, "E313", {"start": v(-4.2, 6.3) * mm, "end": v(-3.93, 6.14) * mm});
            skLineSegment(sketch, "E314", {"start": v(-3.93, 6.14) * mm, "end": v(-3.66, 5.87) * mm});
            skLineSegment(sketch, "E315", {"start": v(-3.66, 5.87) * mm, "end": v(-3.46, 5.6) * mm});
            skLineSegment(sketch, "E316", {"start": v(-3.46, 5.6) * mm, "end": v(-3.33, 5.35) * mm});
            skLineSegment(sketch, "E317", {"start": v(-3.33, 5.35) * mm, "end": v(-3.25, 5.1) * mm});
            skLineSegment(sketch, "E318", {"start": v(-3.25, 5.1) * mm, "end": v(-3.23, 4.89) * mm});
            skLineSegment(sketch, "E319", {"start": v(-3.23, 4.89) * mm, "end": v(-3.26, 4.7) * mm});
            skLineSegment(sketch, "E320", {"start": v(-3.26, 4.7) * mm, "end": v(-3.33, 4.56) * mm});
            skLineSegment(sketch, "E321", {"start": v(-3.33, 4.56) * mm, "end": v(-3.45, 4.45) * mm});
            skLineSegment(sketch, "E322", {"start": v(-3.45, 4.45) * mm, "end": v(-3.49, 4.42) * mm});
            skLineSegment(sketch, "E323", {"start": v(-3.49, 4.42) * mm, "end": v(-3.82, 4.14) * mm});
            skLineSegment(sketch, "E324", {"start": v(-3.82, 4.14) * mm, "end": v(-4.14, 3.82) * mm});
            skLineSegment(sketch, "E325", {"start": v(-4.14, 3.82) * mm, "end": v(-4.42, 3.49) * mm});
            skLineSegment(sketch, "E326", {"start": v(-4.42, 3.49) * mm, "end": v(-4.45, 3.45) * mm});
            skLineSegment(sketch, "E327", {"start": v(-4.45, 3.45) * mm, "end": v(-4.56, 3.33) * mm});
            skLineSegment(sketch, "E328", {"start": v(-4.56, 3.33) * mm, "end": v(-4.7, 3.26) * mm});
            skLineSegment(sketch, "E329", {"start": v(-4.7, 3.26) * mm, "end": v(-4.89, 3.23) * mm});
            skLineSegment(sketch, "E330", {"start": v(-4.89, 3.23) * mm, "end": v(-5.1, 3.25) * mm});
            skLineSegment(sketch, "E331", {"start": v(-5.1, 3.25) * mm, "end": v(-5.35, 3.33) * mm});
            skLineSegment(sketch, "E332", {"start": v(-5.35, 3.33) * mm, "end": v(-5.6, 3.46) * mm});
            skLineSegment(sketch, "E333", {"start": v(-5.6, 3.46) * mm, "end": v(-5.87, 3.66) * mm});
            skLineSegment(sketch, "E334", {"start": v(-5.87, 3.66) * mm, "end": v(-6.14, 3.93) * mm});
            skLineSegment(sketch, "E335", {"start": v(-6.14, 3.93) * mm, "end": v(-6.3, 4.2) * mm});
            skLineSegment(sketch, "E336", {"start": v(-6.3, 4.2) * mm, "end": v(-6.36, 4.22) * mm});
            skLineSegment(sketch, "E337", {"start": v(-6.36, 4.22) * mm, "end": v(-6.52, 4.27) * mm});
            skLineSegment(sketch, "E338", {"start": v(-6.52, 4.27) * mm, "end": v(-6.73, 4.32) * mm});
            skLineSegment(sketch, "E339", {"start": v(-6.73, 4.32) * mm, "end": v(-6.98, 4.36) * mm});
            skLineSegment(sketch, "E340", {"start": v(-6.98, 4.36) * mm, "end": v(-7.29, 4.38) * mm});
            skLineSegment(sketch, "E341", {"start": v(-7.29, 4.38) * mm, "end": v(-7.64, 4.38) * mm});
            skLineSegment(sketch, "E342", {"start": v(-7.64, 4.38) * mm, "end": v(-8.03, 4.34) * mm});
            skLineSegment(sketch, "E343", {"start": v(-8.03, 4.34) * mm, "end": v(-8.46, 4.27) * mm});
            skLineSegment(sketch, "E344", {"start": v(-8.46, 4.27) * mm, "end": v(-8.5, 4.26) * mm});
            skSolve(sketch);
        }
        {
            var Q0;
            Q0=makeQuery(id+"F0.imprint","IMPRINT",FACE,{"disambiguationData":[TD([[makeQuery(id+"F0.imprint","IMPRINT",EDGE,{"derivedFrom":sQuery(id+"F0.wireOp",EDGE,"E0")}),-1.0]])]});
            extrude(context, id + "F1", {"entities" : qUnion([Q0]), "depth" : 4 * mm});
        }
        {
            var Q0;
            Q0=makeQuery(id+"F1.opExtrude","CAP_FACE",FACE,{"disambiguationData":[OSD([sQuery(id+"F0.wireOp",EDGE,"E0"),sQuery(id+"F0.wireOp",EDGE,"E1"),sQuery(id+"F0.wireOp",EDGE,"E2"),sQuery(id+"F0.wireOp",EDGE,"E3"),sQuery(id+"F0.wireOp",EDGE,"E4"),sQuery(id+"F0.wireOp",EDGE,"E5"),sQuery(id+"F0.wireOp",EDGE,"E6"),sQuery(id+"F0.wireOp",EDGE,"E7"),sQuery(id+"F0.wireOp",EDGE,"E8"),sQuery(id+"F0.wireOp",EDGE,"E9"),sQuery(id+"F0.wireOp",EDGE,"E10"),sQuery(id+"F0.wireOp",EDGE,"E11"),sQuery(id+"F0.wireOp",EDGE,"E12"),sQuery(id+"F0.wireOp",EDGE,"E13"),sQuery(id+"F0.wireOp",EDGE,"E14"),sQuery(id+"F0.wireOp",EDGE,"E15"),sQuery(id+"F0.wireOp",EDGE,"E16"),sQuery(id+"F0.wireOp",EDGE,"E17"),sQuery(id+"F0.wireOp",EDGE,"E18"),sQuery(id+"F0.wireOp",EDGE,"E19"),sQuery(id+"F0.wireOp",EDGE,"E20"),sQuery(id+"F0.wireOp",EDGE,"E21"),sQuery(id+"F0.wireOp",EDGE,"E22"),sQuery(id+"F0.wireOp",EDGE,"E23"),sQuery(id+"F0.wireOp",EDGE,"E24"),sQuery(id+"F0.wireOp",EDGE,"E25"),sQuery(id+"F0.wireOp",EDGE,"E26"),sQuery(id+"F0.wireOp",EDGE,"E27"),sQuery(id+"F0.wireOp",EDGE,"E28"),sQuery(id+"F0.wireOp",EDGE,"E29"),sQuery(id+"F0.wireOp",EDGE,"E30"),sQuery(id+"F0.wireOp",EDGE,"E31"),sQuery(id+"F0.wireOp",EDGE,"E32"),sQuery(id+"F0.wireOp",EDGE,"E33"),sQuery(id+"F0.wireOp",EDGE,"E34"),sQuery(id+"F0.wireOp",EDGE,"E35"),sQuery(id+"F0.wireOp",EDGE,"E36"),sQuery(id+"F0.wireOp",EDGE,"E37"),sQuery(id+"F0.wireOp",EDGE,"E38"),sQuery(id+"F0.wireOp",EDGE,"E39"),sQuery(id+"F0.wireOp",EDGE,"E40"),sQuery(id+"F0.wireOp",EDGE,"E41"),sQuery(id+"F0.wireOp",EDGE,"E42"),sQuery(id+"F0.wireOp",EDGE,"E43"),sQuery(id+"F0.wireOp",EDGE,"E44"),sQuery(id+"F0.wireOp",EDGE,"E45"),sQuery(id+"F0.wireOp",EDGE,"E46"),sQuery(id+"F0.wireOp",EDGE,"E47"),sQuery(id+"F0.wireOp",EDGE,"E48"),sQuery(id+"F0.wireOp",EDGE,"E49"),sQuery(id+"F0.wireOp",EDGE,"E50"),sQuery(id+"F0.wireOp",EDGE,"E51"),sQuery(id+"F0.wireOp",EDGE,"E52"),sQuery(id+"F0.wireOp",EDGE,"E53"),sQuery(id+"F0.wireOp",EDGE,"E54"),sQuery(id+"F0.wireOp",EDGE,"E55"),sQuery(id+"F0.wireOp",EDGE,"E56"),sQuery(id+"F0.wireOp",EDGE,"E57"),sQuery(id+"F0.wireOp",EDGE,"E58"),sQuery(id+"F0.wireOp",EDGE,"E59"),sQuery(id+"F0.wireOp",EDGE,"E60"),sQuery(id+"F0.wireOp",EDGE,"E61"),sQuery(id+"F0.wireOp",EDGE,"E62"),sQuery(id+"F0.wireOp",EDGE,"E63"),sQuery(id+"F0.wireOp",EDGE,"E64"),sQuery(id+"F0.wireOp",EDGE,"E65"),sQuery(id+"F0.wireOp",EDGE,"E66"),sQuery(id+"F0.wireOp",EDGE,"E67"),sQuery(id+"F0.wireOp",EDGE,"E68"),sQuery(id+"F0.wireOp",EDGE,"E69"),sQuery(id+"F0.wireOp",EDGE,"E70"),sQuery(id+"F0.wireOp",EDGE,"E71"),sQuery(id+"F0.wireOp",EDGE,"E72"),sQuery(id+"F0.wireOp",EDGE,"E73"),sQuery(id+"F0.wireOp",EDGE,"E74"),sQuery(id+"F0.wireOp",EDGE,"E75"),sQuery(id+"F0.wireOp",EDGE,"E76"),sQuery(id+"F0.wireOp",EDGE,"E77"),sQuery(id+"F0.wireOp",EDGE,"E78"),sQuery(id+"F0.wireOp",EDGE,"E79"),sQuery(id+"F0.wireOp",EDGE,"E80"),sQuery(id+"F0.wireOp",EDGE,"E81"),sQuery(id+"F0.wireOp",EDGE,"E82"),sQuery(id+"F0.wireOp",EDGE,"E83"),sQuery(id+"F0.wireOp",EDGE,"E84"),sQuery(id+"F0.wireOp",EDGE,"E85"),sQuery(id+"F0.wireOp",EDGE,"E86"),sQuery(id+"F0.wireOp",EDGE,"E87"),sQuery(id+"F0.wireOp",EDGE,"E88"),sQuery(id+"F0.wireOp",EDGE,"E89"),sQuery(id+"F0.wireOp",EDGE,"E90"),sQuery(id+"F0.wireOp",EDGE,"E91"),sQuery(id+"F0.wireOp",EDGE,"E92"),sQuery(id+"F0.wireOp",EDGE,"E93"),sQuery(id+"F0.wireOp",EDGE,"E94"),sQuery(id+"F0.wireOp",EDGE,"E95"),sQuery(id+"F0.wireOp",EDGE,"E96"),sQuery(id+"F0.wireOp",EDGE,"E97"),sQuery(id+"F0.wireOp",EDGE,"E98"),sQuery(id+"F0.wireOp",EDGE,"E99"),sQuery(id+"F0.wireOp",EDGE,"E100"),sQuery(id+"F0.wireOp",EDGE,"E101"),sQuery(id+"F0.wireOp",EDGE,"E102"),sQuery(id+"F0.wireOp",EDGE,"E103"),sQuery(id+"F0.wireOp",EDGE,"E104"),sQuery(id+"F0.wireOp",EDGE,"E105"),sQuery(id+"F0.wireOp",EDGE,"E106"),sQuery(id+"F0.wireOp",EDGE,"E107"),sQuery(id+"F0.wireOp",EDGE,"E108"),sQuery(id+"F0.wireOp",EDGE,"E109"),sQuery(id+"F0.wireOp",EDGE,"E110"),sQuery(id+"F0.wireOp",EDGE,"E111"),sQuery(id+"F0.wireOp",EDGE,"E112"),sQuery(id+"F0.wireOp",EDGE,"E113"),sQuery(id+"F0.wireOp",EDGE,"E114"),sQuery(id+"F0.wireOp",EDGE,"E115"),sQuery(id+"F0.wireOp",EDGE,"E116"),sQuery(id+"F0.wireOp",EDGE,"E117"),sQuery(id+"F0.wireOp",EDGE,"E118"),sQuery(id+"F0.wireOp",EDGE,"E119"),sQuery(id+"F0.wireOp",EDGE,"E120"),sQuery(id+"F0.wireOp",EDGE,"E121"),sQuery(id+"F0.wireOp",EDGE,"E122"),sQuery(id+"F0.wireOp",EDGE,"E123"),sQuery(id+"F0.wireOp",EDGE,"E124"),sQuery(id+"F0.wireOp",EDGE,"E125"),sQuery(id+"F0.wireOp",EDGE,"E126"),sQuery(id+"F0.wireOp",EDGE,"E127"),sQuery(id+"F0.wireOp",EDGE,"E128"),sQuery(id+"F0.wireOp",EDGE,"E129"),sQuery(id+"F0.wireOp",EDGE,"E130"),sQuery(id+"F0.wireOp",EDGE,"E131"),sQuery(id+"F0.wireOp",EDGE,"E132"),sQuery(id+"F0.wireOp",EDGE,"E133"),sQuery(id+"F0.wireOp",EDGE,"E134"),sQuery(id+"F0.wireOp",EDGE,"E135"),sQuery(id+"F0.wireOp",EDGE,"E136"),sQuery(id+"F0.wireOp",EDGE,"E137"),sQuery(id+"F0.wireOp",EDGE,"E138"),sQuery(id+"F0.wireOp",EDGE,"E139"),sQuery(id+"F0.wireOp",EDGE,"E140"),sQuery(id+"F0.wireOp",EDGE,"E141"),sQuery(id+"F0.wireOp",EDGE,"E142"),sQuery(id+"F0.wireOp",EDGE,"E143"),sQuery(id+"F0.wireOp",EDGE,"E144"),sQuery(id+"F0.wireOp",EDGE,"E145"),sQuery(id+"F0.wireOp",EDGE,"E146"),sQuery(id+"F0.wireOp",EDGE,"E147"),sQuery(id+"F0.wireOp",EDGE,"E148"),sQuery(id+"F0.wireOp",EDGE,"E149"),sQuery(id+"F0.wireOp",EDGE,"E150"),sQuery(id+"F0.wireOp",EDGE,"E151"),sQuery(id+"F0.wireOp",EDGE,"E152"),sQuery(id+"F0.wireOp",EDGE,"E153"),sQuery(id+"F0.wireOp",EDGE,"E154"),sQuery(id+"F0.wireOp",EDGE,"E155"),sQuery(id+"F0.wireOp",EDGE,"E156"),sQuery(id+"F0.wireOp",EDGE,"E157"),sQuery(id+"F0.wireOp",EDGE,"E158"),sQuery(id+"F0.wireOp",EDGE,"E159"),sQuery(id+"F0.wireOp",EDGE,"E160"),sQuery(id+"F0.wireOp",EDGE,"E161"),sQuery(id+"F0.wireOp",EDGE,"E162"),sQuery(id+"F0.wireOp",EDGE,"E163"),sQuery(id+"F0.wireOp",EDGE,"E164"),sQuery(id+"F0.wireOp",EDGE,"E165"),sQuery(id+"F0.wireOp",EDGE,"E166"),sQuery(id+"F0.wireOp",EDGE,"E167"),sQuery(id+"F0.wireOp",EDGE,"E168"),sQuery(id+"F0.wireOp",EDGE,"E169"),sQuery(id+"F0.wireOp",EDGE,"E170"),sQuery(id+"F0.wireOp",EDGE,"E171"),sQuery(id+"F0.wireOp",EDGE,"E172"),sQuery(id+"F0.wireOp",EDGE,"E173"),sQuery(id+"F0.wireOp",EDGE,"E174"),sQuery(id+"F0.wireOp",EDGE,"E175"),sQuery(id+"F0.wireOp",EDGE,"E176"),sQuery(id+"F0.wireOp",EDGE,"E177"),sQuery(id+"F0.wireOp",EDGE,"E178"),sQuery(id+"F0.wireOp",EDGE,"E179"),sQuery(id+"F0.wireOp",EDGE,"E180"),sQuery(id+"F0.wireOp",EDGE,"E181"),sQuery(id+"F0.wireOp",EDGE,"E182"),sQuery(id+"F0.wireOp",EDGE,"E183"),sQuery(id+"F0.wireOp",EDGE,"E184"),sQuery(id+"F0.wireOp",EDGE,"E185"),sQuery(id+"F0.wireOp",EDGE,"E186"),sQuery(id+"F0.wireOp",EDGE,"E187"),sQuery(id+"F0.wireOp",EDGE,"E188"),sQuery(id+"F0.wireOp",EDGE,"E189"),sQuery(id+"F0.wireOp",EDGE,"E190"),sQuery(id+"F0.wireOp",EDGE,"E191"),sQuery(id+"F0.wireOp",EDGE,"E192"),sQuery(id+"F0.wireOp",EDGE,"E193"),sQuery(id+"F0.wireOp",EDGE,"E194"),sQuery(id+"F0.wireOp",EDGE,"E195"),sQuery(id+"F0.wireOp",EDGE,"E196"),sQuery(id+"F0.wireOp",EDGE,"E197"),sQuery(id+"F0.wireOp",EDGE,"E198"),sQuery(id+"F0.wireOp",EDGE,"E199"),sQuery(id+"F0.wireOp",EDGE,"E200"),sQuery(id+"F0.wireOp",EDGE,"E201"),sQuery(id+"F0.wireOp",EDGE,"E202"),sQuery(id+"F0.wireOp",EDGE,"E203"),sQuery(id+"F0.wireOp",EDGE,"E204"),sQuery(id+"F0.wireOp",EDGE,"E205"),sQuery(id+"F0.wireOp",EDGE,"E206"),sQuery(id+"F0.wireOp",EDGE,"E207"),sQuery(id+"F0.wireOp",EDGE,"E208"),sQuery(id+"F0.wireOp",EDGE,"E209"),sQuery(id+"F0.wireOp",EDGE,"E210"),sQuery(id+"F0.wireOp",EDGE,"E211"),sQuery(id+"F0.wireOp",EDGE,"E212"),sQuery(id+"F0.wireOp",EDGE,"E213"),sQuery(id+"F0.wireOp",EDGE,"E214"),sQuery(id+"F0.wireOp",EDGE,"E215"),sQuery(id+"F0.wireOp",EDGE,"E216"),sQuery(id+"F0.wireOp",EDGE,"E217"),sQuery(id+"F0.wireOp",EDGE,"E218"),sQuery(id+"F0.wireOp",EDGE,"E219"),sQuery(id+"F0.wireOp",EDGE,"E220"),sQuery(id+"F0.wireOp",EDGE,"E221"),sQuery(id+"F0.wireOp",EDGE,"E222"),sQuery(id+"F0.wireOp",EDGE,"E223"),sQuery(id+"F0.wireOp",EDGE,"E224"),sQuery(id+"F0.wireOp",EDGE,"E225"),sQuery(id+"F0.wireOp",EDGE,"E226"),sQuery(id+"F0.wireOp",EDGE,"E227"),sQuery(id+"F0.wireOp",EDGE,"E228"),sQuery(id+"F0.wireOp",EDGE,"E229"),sQuery(id+"F0.wireOp",EDGE,"E230"),sQuery(id+"F0.wireOp",EDGE,"E231"),sQuery(id+"F0.wireOp",EDGE,"E232"),sQuery(id+"F0.wireOp",EDGE,"E233"),sQuery(id+"F0.wireOp",EDGE,"E234"),sQuery(id+"F0.wireOp",EDGE,"E235"),sQuery(id+"F0.wireOp",EDGE,"E236"),sQuery(id+"F0.wireOp",EDGE,"E237"),sQuery(id+"F0.wireOp",EDGE,"E238"),sQuery(id+"F0.wireOp",EDGE,"E239"),sQuery(id+"F0.wireOp",EDGE,"E240"),sQuery(id+"F0.wireOp",EDGE,"E241"),sQuery(id+"F0.wireOp",EDGE,"E242"),sQuery(id+"F0.wireOp",EDGE,"E243"),sQuery(id+"F0.wireOp",EDGE,"E244"),sQuery(id+"F0.wireOp",EDGE,"E245"),sQuery(id+"F0.wireOp",EDGE,"E246"),sQuery(id+"F0.wireOp",EDGE,"E247"),sQuery(id+"F0.wireOp",EDGE,"E248"),sQuery(id+"F0.wireOp",EDGE,"E249"),sQuery(id+"F0.wireOp",EDGE,"E250"),sQuery(id+"F0.wireOp",EDGE,"E251"),sQuery(id+"F0.wireOp",EDGE,"E252"),sQuery(id+"F0.wireOp",EDGE,"E253"),sQuery(id+"F0.wireOp",EDGE,"E254"),sQuery(id+"F0.wireOp",EDGE,"E255"),sQuery(id+"F0.wireOp",EDGE,"E256"),sQuery(id+"F0.wireOp",EDGE,"E257"),sQuery(id+"F0.wireOp",EDGE,"E258"),sQuery(id+"F0.wireOp",EDGE,"E259"),sQuery(id+"F0.wireOp",EDGE,"E260"),sQuery(id+"F0.wireOp",EDGE,"E261"),sQuery(id+"F0.wireOp",EDGE,"E262"),sQuery(id+"F0.wireOp",EDGE,"E263"),sQuery(id+"F0.wireOp",EDGE,"E264"),sQuery(id+"F0.wireOp",EDGE,"E265"),sQuery(id+"F0.wireOp",EDGE,"E266"),sQuery(id+"F0.wireOp",EDGE,"E267"),sQuery(id+"F0.wireOp",EDGE,"E268"),sQuery(id+"F0.wireOp",EDGE,"E269"),sQuery(id+"F0.wireOp",EDGE,"E270"),sQuery(id+"F0.wireOp",EDGE,"E271"),sQuery(id+"F0.wireOp",EDGE,"E272"),sQuery(id+"F0.wireOp",EDGE,"E273"),sQuery(id+"F0.wireOp",EDGE,"E274"),sQuery(id+"F0.wireOp",EDGE,"E275"),sQuery(id+"F0.wireOp",EDGE,"E276"),sQuery(id+"F0.wireOp",EDGE,"E277"),sQuery(id+"F0.wireOp",EDGE,"E278"),sQuery(id+"F0.wireOp",EDGE,"E279"),sQuery(id+"F0.wireOp",EDGE,"E280"),sQuery(id+"F0.wireOp",EDGE,"E281"),sQuery(id+"F0.wireOp",EDGE,"E282"),sQuery(id+"F0.wireOp",EDGE,"E283"),sQuery(id+"F0.wireOp",EDGE,"E284"),sQuery(id+"F0.wireOp",EDGE,"E285"),sQuery(id+"F0.wireOp",EDGE,"E286"),sQuery(id+"F0.wireOp",EDGE,"E287"),sQuery(id+"F0.wireOp",EDGE,"E288"),sQuery(id+"F0.wireOp",EDGE,"E289"),sQuery(id+"F0.wireOp",EDGE,"E290"),sQuery(id+"F0.wireOp",EDGE,"E291"),sQuery(id+"F0.wireOp",EDGE,"E292"),sQuery(id+"F0.wireOp",EDGE,"E293"),sQuery(id+"F0.wireOp",EDGE,"E294"),sQuery(id+"F0.wireOp",EDGE,"E295"),sQuery(id+"F0.wireOp",EDGE,"E296"),sQuery(id+"F0.wireOp",EDGE,"E297"),sQuery(id+"F0.wireOp",EDGE,"E298"),sQuery(id+"F0.wireOp",EDGE,"E299"),sQuery(id+"F0.wireOp",EDGE,"E300"),sQuery(id+"F0.wireOp",EDGE,"E301"),sQuery(id+"F0.wireOp",EDGE,"E302"),sQuery(id+"F0.wireOp",EDGE,"E303"),sQuery(id+"F0.wireOp",EDGE,"E304"),sQuery(id+"F0.wireOp",EDGE,"E305"),sQuery(id+"F0.wireOp",EDGE,"E306"),sQuery(id+"F0.wireOp",EDGE,"E307"),sQuery(id+"F0.wireOp",EDGE,"E308"),sQuery(id+"F0.wireOp",EDGE,"E309"),sQuery(id+"F0.wireOp",EDGE,"E310"),sQuery(id+"F0.wireOp",EDGE,"E311"),sQuery(id+"F0.wireOp",EDGE,"E312"),sQuery(id+"F0.wireOp",EDGE,"E313"),sQuery(id+"F0.wireOp",EDGE,"E314"),sQuery(id+"F0.wireOp",EDGE,"E315"),sQuery(id+"F0.wireOp",EDGE,"E316"),sQuery(id+"F0.wireOp",EDGE,"E317"),sQuery(id+"F0.wireOp",EDGE,"E318"),sQuery(id+"F0.wireOp",EDGE,"E319"),sQuery(id+"F0.wireOp",EDGE,"E320"),sQuery(id+"F0.wireOp",EDGE,"E321"),sQuery(id+"F0.wireOp",EDGE,"E322"),sQuery(id+"F0.wireOp",EDGE,"E323"),sQuery(id+"F0.wireOp",EDGE,"E324"),sQuery(id+"F0.wireOp",EDGE,"E325"),sQuery(id+"F0.wireOp",EDGE,"E326"),sQuery(id+"F0.wireOp",EDGE,"E327"),sQuery(id+"F0.wireOp",EDGE,"E328"),sQuery(id+"F0.wireOp",EDGE,"E329"),sQuery(id+"F0.wireOp",EDGE,"E330"),sQuery(id+"F0.wireOp",EDGE,"E331"),sQuery(id+"F0.wireOp",EDGE,"E332"),sQuery(id+"F0.wireOp",EDGE,"E333"),sQuery(id+"F0.wireOp",EDGE,"E334"),sQuery(id+"F0.wireOp",EDGE,"E335"),sQuery(id+"F0.wireOp",EDGE,"E336"),sQuery(id+"F0.wireOp",EDGE,"E337"),sQuery(id+"F0.wireOp",EDGE,"E338"),sQuery(id+"F0.wireOp",EDGE,"E339"),sQuery(id+"F0.wireOp",EDGE,"E340"),sQuery(id+"F0.wireOp",EDGE,"E341"),sQuery(id+"F0.wireOp",EDGE,"E342"),sQuery(id+"F0.wireOp",EDGE,"E343"),sQuery(id+"F0.wireOp",EDGE,"E344")])],"isStart":false});
            var sketch = newSketch(context, id + "F2", { "sketchPlane" : qUnion([Q0])});
            skCircle(sketch, "E345", {"center": v(0, 0) * mm, "radius": 4.1 * mm});
            skLineSegment(sketch, "E346", {"start": v(29.66, -7.2) * mm, "end": v(29.89, -6.35) * mm});
            skLineSegment(sketch, "E347", {"start": v(29.89, -6.35) * mm, "end": v(30.03, -5.49) * mm});
            skLineSegment(sketch, "E348", {"start": v(30.03, -5.49) * mm, "end": v(29.86, -5.37) * mm});
            skLineSegment(sketch, "E349", {"start": v(29.86, -5.37) * mm, "end": v(29.65, -5.24) * mm});
            skLineSegment(sketch, "E350", {"start": v(29.65, -5.24) * mm, "end": v(29.45, -5.11) * mm});
            skLineSegment(sketch, "E351", {"start": v(29.45, -5.11) * mm, "end": v(29.26, -5) * mm});
            skLineSegment(sketch, "E352", {"start": v(29.26, -5) * mm, "end": v(29.07, -4.9) * mm});
            skLineSegment(sketch, "E353", {"start": v(29.07, -4.9) * mm, "end": v(28.9, -4.8) * mm});
            skLineSegment(sketch, "E354", {"start": v(28.9, -4.8) * mm, "end": v(28.73, -4.71) * mm});
            skLineSegment(sketch, "E355", {"start": v(28.73, -4.71) * mm, "end": v(28.57, -4.63) * mm});
            skLineSegment(sketch, "E356", {"start": v(28.57, -4.63) * mm, "end": v(28.42, -4.57) * mm});
            skLineSegment(sketch, "E357", {"start": v(28.42, -4.57) * mm, "end": v(28.29, -4.5) * mm});
            skLineSegment(sketch, "E358", {"start": v(28.29, -4.5) * mm, "end": v(28.16, -4.45) * mm});
            skLineSegment(sketch, "E359", {"start": v(28.16, -4.45) * mm, "end": v(28.04, -4.4) * mm});
            skLineSegment(sketch, "E360", {"start": v(28.04, -4.4) * mm, "end": v(27.93, -4.37) * mm});
            skLineSegment(sketch, "E361", {"start": v(27.93, -4.37) * mm, "end": v(27.83, -4.33) * mm});
            skLineSegment(sketch, "E362", {"start": v(27.83, -4.33) * mm, "end": v(27.75, -4.3) * mm});
            skLineSegment(sketch, "E363", {"start": v(27.75, -4.3) * mm, "end": v(27.67, -4.28) * mm});
            skLineSegment(sketch, "E364", {"start": v(27.67, -4.28) * mm, "end": v(27.6, -4.27) * mm});
            skLineSegment(sketch, "E365", {"start": v(27.6, -4.27) * mm, "end": v(27.56, -4.25) * mm});
            skLineSegment(sketch, "E366", {"start": v(27.56, -4.25) * mm, "end": v(27.52, -4.24) * mm});
            skLineSegment(sketch, "E367", {"start": v(27.52, -4.24) * mm, "end": v(27.49, -4.24) * mm});
            skLineSegment(sketch, "E368", {"start": v(27.49, -4.24) * mm, "end": v(27.47, -4.23) * mm});
            skLineSegment(sketch, "E369", {"start": v(27.47, -4.23) * mm, "end": v(27.47, -4.23) * mm});
            skLineSegment(sketch, "E370", {"start": v(27.47, -4.23) * mm, "end": v(27.38, -4.22) * mm});
            skLineSegment(sketch, "E371", {"start": v(27.38, -4.22) * mm, "end": v(27.23, -4.2) * mm});
            skLineSegment(sketch, "E372", {"start": v(27.23, -4.2) * mm, "end": v(27.08, -4.17) * mm});
            skLineSegment(sketch, "E373", {"start": v(27.08, -4.17) * mm, "end": v(26.95, -4.14) * mm});
            skLineSegment(sketch, "E374", {"start": v(26.95, -4.14) * mm, "end": v(26.83, -4.1) * mm});
            skLineSegment(sketch, "E375", {"start": v(26.83, -4.1) * mm, "end": v(26.73, -4.06) * mm});
            skLineSegment(sketch, "E376", {"start": v(26.73, -4.06) * mm, "end": v(26.64, -4.02) * mm});
            skLineSegment(sketch, "E377", {"start": v(26.64, -4.02) * mm, "end": v(26.56, -3.98) * mm});
            skLineSegment(sketch, "E378", {"start": v(26.56, -3.98) * mm, "end": v(26.5, -3.94) * mm});
            skLineSegment(sketch, "E379", {"start": v(26.5, -3.94) * mm, "end": v(26.45, -3.9) * mm});
            skLineSegment(sketch, "E380", {"start": v(26.45, -3.9) * mm, "end": v(26.4, -3.85) * mm});
            skLineSegment(sketch, "E381", {"start": v(26.4, -3.85) * mm, "end": v(26.39, -3.8) * mm});
            skLineSegment(sketch, "E382", {"start": v(26.39, -3.8) * mm, "end": v(26.38, -3.76) * mm});
            skLineSegment(sketch, "E383", {"start": v(26.38, -3.76) * mm, "end": v(26.38, -3.72) * mm});
            skLineSegment(sketch, "E384", {"start": v(26.38, -3.72) * mm, "end": v(26.4, -3.62) * mm});
            skLineSegment(sketch, "E385", {"start": v(26.4, -3.62) * mm, "end": v(26.46, -3.06) * mm});
            skLineSegment(sketch, "E386", {"start": v(26.46, -3.06) * mm, "end": v(26.52, -2.5) * mm});
            skLineSegment(sketch, "E387", {"start": v(26.52, -2.5) * mm, "end": v(26.57, -1.95) * mm});
            skLineSegment(sketch, "E388", {"start": v(26.57, -1.95) * mm, "end": v(26.57, -1.85) * mm});
            skLineSegment(sketch, "E389", {"start": v(26.57, -1.85) * mm, "end": v(26.58, -1.8) * mm});
            skLineSegment(sketch, "E390", {"start": v(26.58, -1.8) * mm, "end": v(26.6, -1.77) * mm});
            skLineSegment(sketch, "E391", {"start": v(26.6, -1.77) * mm, "end": v(26.63, -1.73) * mm});
            skLineSegment(sketch, "E392", {"start": v(26.63, -1.73) * mm, "end": v(26.68, -1.7) * mm});
            skLineSegment(sketch, "E393", {"start": v(26.68, -1.7) * mm, "end": v(26.74, -1.66) * mm});
            skLineSegment(sketch, "E394", {"start": v(26.74, -1.66) * mm, "end": v(26.8, -1.63) * mm});
            skLineSegment(sketch, "E395", {"start": v(26.8, -1.63) * mm, "end": v(26.9, -1.6) * mm});
            skLineSegment(sketch, "E396", {"start": v(26.9, -1.6) * mm, "end": v(26.99, -1.58) * mm});
            skLineSegment(sketch, "E397", {"start": v(26.99, -1.58) * mm, "end": v(27.1, -1.57) * mm});
            skLineSegment(sketch, "E398", {"start": v(27.1, -1.57) * mm, "end": v(27.22, -1.56) * mm});
            skLineSegment(sketch, "E399", {"start": v(27.22, -1.56) * mm, "end": v(27.36, -1.55) * mm});
            skLineSegment(sketch, "E400", {"start": v(27.36, -1.55) * mm, "end": v(27.5, -1.55) * mm});
            skLineSegment(sketch, "E401", {"start": v(27.5, -1.55) * mm, "end": v(27.66, -1.56) * mm});
            skLineSegment(sketch, "E402", {"start": v(27.66, -1.56) * mm, "end": v(27.75, -1.57) * mm});
            skLineSegment(sketch, "E403", {"start": v(27.75, -1.57) * mm, "end": v(27.75, -1.57) * mm});
            skLineSegment(sketch, "E404", {"start": v(27.75, -1.57) * mm, "end": v(27.77, -1.57) * mm});
            skLineSegment(sketch, "E405", {"start": v(27.77, -1.57) * mm, "end": v(27.8, -1.57) * mm});
            skLineSegment(sketch, "E406", {"start": v(27.8, -1.57) * mm, "end": v(27.84, -1.57) * mm});
            skLineSegment(sketch, "E407", {"start": v(27.84, -1.57) * mm, "end": v(27.9, -1.57) * mm});
            skLineSegment(sketch, "E408", {"start": v(27.9, -1.57) * mm, "end": v(27.96, -1.56) * mm});
            skLineSegment(sketch, "E409", {"start": v(27.96, -1.56) * mm, "end": v(28.04, -1.56) * mm});
            skLineSegment(sketch, "E410", {"start": v(28.04, -1.56) * mm, "end": v(28.13, -1.55) * mm});
            skLineSegment(sketch, "E411", {"start": v(28.13, -1.55) * mm, "end": v(28.23, -1.54) * mm});
            skLineSegment(sketch, "E412", {"start": v(28.23, -1.54) * mm, "end": v(28.34, -1.52) * mm});
            skLineSegment(sketch, "E413", {"start": v(28.34, -1.52) * mm, "end": v(28.47, -1.5) * mm});
            skLineSegment(sketch, "E414", {"start": v(28.47, -1.5) * mm, "end": v(28.6, -1.48) * mm});
            skLineSegment(sketch, "E415", {"start": v(28.6, -1.48) * mm, "end": v(28.75, -1.44) * mm});
            skLineSegment(sketch, "E416", {"start": v(28.75, -1.44) * mm, "end": v(28.91, -1.4) * mm});
            skLineSegment(sketch, "E417", {"start": v(28.91, -1.4) * mm, "end": v(29.08, -1.37) * mm});
            skLineSegment(sketch, "E418", {"start": v(29.08, -1.37) * mm, "end": v(29.26, -1.32) * mm});
            skLineSegment(sketch, "E419", {"start": v(29.26, -1.32) * mm, "end": v(29.46, -1.26) * mm});
            skLineSegment(sketch, "E420", {"start": v(29.46, -1.26) * mm, "end": v(29.66, -1.2) * mm});
            skLineSegment(sketch, "E421", {"start": v(29.66, -1.2) * mm, "end": v(29.87, -1.12) * mm});
            skLineSegment(sketch, "E422", {"start": v(29.87, -1.12) * mm, "end": v(30.1, -1.04) * mm});
            skLineSegment(sketch, "E423", {"start": v(30.1, -1.04) * mm, "end": v(30.32, -0.95) * mm});
            skLineSegment(sketch, "E424", {"start": v(30.32, -0.95) * mm, "end": v(30.51, -0.87) * mm});
            skLineSegment(sketch, "E425", {"start": v(30.51, -0.87) * mm, "end": v(30.56, 0) * mm});
            skLineSegment(sketch, "E426", {"start": v(30.56, 0) * mm, "end": v(30.51, 0.87) * mm});
            skLineSegment(sketch, "E427", {"start": v(30.51, 0.87) * mm, "end": v(30.32, 0.95) * mm});
            skLineSegment(sketch, "E428", {"start": v(30.32, 0.95) * mm, "end": v(30.1, 1.04) * mm});
            skLineSegment(sketch, "E429", {"start": v(30.1, 1.04) * mm, "end": v(29.87, 1.12) * mm});
            skLineSegment(sketch, "E430", {"start": v(29.87, 1.12) * mm, "end": v(29.66, 1.2) * mm});
            skLineSegment(sketch, "E431", {"start": v(29.66, 1.2) * mm, "end": v(29.46, 1.26) * mm});
            skLineSegment(sketch, "E432", {"start": v(29.46, 1.26) * mm, "end": v(29.26, 1.32) * mm});
            skLineSegment(sketch, "E433", {"start": v(29.26, 1.32) * mm, "end": v(29.08, 1.37) * mm});
            skLineSegment(sketch, "E434", {"start": v(29.08, 1.37) * mm, "end": v(28.91, 1.4) * mm});
            skLineSegment(sketch, "E435", {"start": v(28.91, 1.4) * mm, "end": v(28.75, 1.44) * mm});
            skLineSegment(sketch, "E436", {"start": v(28.75, 1.44) * mm, "end": v(28.6, 1.48) * mm});
            skLineSegment(sketch, "E437", {"start": v(28.6, 1.48) * mm, "end": v(28.47, 1.5) * mm});
            skLineSegment(sketch, "E438", {"start": v(28.47, 1.5) * mm, "end": v(28.34, 1.52) * mm});
            skLineSegment(sketch, "E439", {"start": v(28.34, 1.52) * mm, "end": v(28.23, 1.54) * mm});
            skLineSegment(sketch, "E440", {"start": v(28.23, 1.54) * mm, "end": v(28.13, 1.55) * mm});
            skLineSegment(sketch, "E441", {"start": v(28.13, 1.55) * mm, "end": v(28.04, 1.56) * mm});
            skLineSegment(sketch, "E442", {"start": v(28.04, 1.56) * mm, "end": v(27.96, 1.56) * mm});
            skLineSegment(sketch, "E443", {"start": v(27.96, 1.56) * mm, "end": v(27.9, 1.57) * mm});
            skLineSegment(sketch, "E444", {"start": v(27.9, 1.57) * mm, "end": v(27.84, 1.57) * mm});
            skLineSegment(sketch, "E445", {"start": v(27.84, 1.57) * mm, "end": v(27.8, 1.57) * mm});
            skLineSegment(sketch, "E446", {"start": v(27.8, 1.57) * mm, "end": v(27.77, 1.57) * mm});
            skLineSegment(sketch, "E447", {"start": v(27.77, 1.57) * mm, "end": v(27.75, 1.57) * mm});
            skLineSegment(sketch, "E448", {"start": v(27.75, 1.57) * mm, "end": v(27.75, 1.57) * mm});
            skLineSegment(sketch, "E449", {"start": v(27.75, 1.57) * mm, "end": v(27.66, 1.56) * mm});
            skLineSegment(sketch, "E450", {"start": v(27.66, 1.56) * mm, "end": v(27.5, 1.55) * mm});
            skLineSegment(sketch, "E451", {"start": v(27.5, 1.55) * mm, "end": v(27.36, 1.55) * mm});
            skLineSegment(sketch, "E452", {"start": v(27.36, 1.55) * mm, "end": v(27.22, 1.56) * mm});
            skLineSegment(sketch, "E453", {"start": v(27.22, 1.56) * mm, "end": v(27.1, 1.57) * mm});
            skLineSegment(sketch, "E454", {"start": v(27.1, 1.57) * mm, "end": v(26.99, 1.58) * mm});
            skLineSegment(sketch, "E455", {"start": v(26.99, 1.58) * mm, "end": v(26.9, 1.6) * mm});
            skLineSegment(sketch, "E456", {"start": v(26.9, 1.6) * mm, "end": v(26.8, 1.63) * mm});
            skLineSegment(sketch, "E457", {"start": v(26.8, 1.63) * mm, "end": v(26.74, 1.66) * mm});
            skLineSegment(sketch, "E458", {"start": v(26.74, 1.66) * mm, "end": v(26.68, 1.7) * mm});
            skLineSegment(sketch, "E459", {"start": v(26.68, 1.7) * mm, "end": v(26.63, 1.73) * mm});
            skLineSegment(sketch, "E460", {"start": v(26.63, 1.73) * mm, "end": v(26.6, 1.77) * mm});
            skLineSegment(sketch, "E461", {"start": v(26.6, 1.77) * mm, "end": v(26.58, 1.8) * mm});
            skLineSegment(sketch, "E462", {"start": v(26.58, 1.8) * mm, "end": v(26.57, 1.85) * mm});
            skLineSegment(sketch, "E463", {"start": v(26.57, 1.85) * mm, "end": v(26.57, 1.95) * mm});
            skLineSegment(sketch, "E464", {"start": v(26.57, 1.95) * mm, "end": v(26.52, 2.5) * mm});
            skLineSegment(sketch, "E465", {"start": v(26.52, 2.5) * mm, "end": v(26.46, 3.06) * mm});
            skLineSegment(sketch, "E466", {"start": v(26.46, 3.06) * mm, "end": v(26.4, 3.62) * mm});
            skLineSegment(sketch, "E467", {"start": v(26.4, 3.62) * mm, "end": v(26.38, 3.72) * mm});
            skLineSegment(sketch, "E468", {"start": v(26.38, 3.72) * mm, "end": v(26.38, 3.76) * mm});
            skLineSegment(sketch, "E469", {"start": v(26.38, 3.76) * mm, "end": v(26.39, 3.8) * mm});
            skLineSegment(sketch, "E470", {"start": v(26.39, 3.8) * mm, "end": v(26.4, 3.85) * mm});
            skLineSegment(sketch, "E471", {"start": v(26.4, 3.85) * mm, "end": v(26.45, 3.9) * mm});
            skLineSegment(sketch, "E472", {"start": v(26.45, 3.9) * mm, "end": v(26.5, 3.94) * mm});
            skLineSegment(sketch, "E473", {"start": v(26.5, 3.94) * mm, "end": v(26.56, 3.98) * mm});
            skLineSegment(sketch, "E474", {"start": v(26.56, 3.98) * mm, "end": v(26.64, 4.02) * mm});
            skLineSegment(sketch, "E475", {"start": v(26.64, 4.02) * mm, "end": v(26.73, 4.06) * mm});
            skLineSegment(sketch, "E476", {"start": v(26.73, 4.06) * mm, "end": v(26.83, 4.1) * mm});
            skLineSegment(sketch, "E477", {"start": v(26.83, 4.1) * mm, "end": v(26.95, 4.14) * mm});
            skLineSegment(sketch, "E478", {"start": v(26.95, 4.14) * mm, "end": v(27.08, 4.17) * mm});
            skLineSegment(sketch, "E479", {"start": v(27.08, 4.17) * mm, "end": v(27.23, 4.2) * mm});
            skLineSegment(sketch, "E480", {"start": v(27.23, 4.2) * mm, "end": v(27.38, 4.22) * mm});
            skLineSegment(sketch, "E481", {"start": v(27.38, 4.22) * mm, "end": v(27.47, 4.23) * mm});
            skLineSegment(sketch, "E482", {"start": v(27.47, 4.23) * mm, "end": v(27.47, 4.23) * mm});
            skLineSegment(sketch, "E483", {"start": v(27.47, 4.23) * mm, "end": v(27.49, 4.24) * mm});
            skLineSegment(sketch, "E484", {"start": v(27.49, 4.24) * mm, "end": v(27.52, 4.24) * mm});
            skLineSegment(sketch, "E485", {"start": v(27.52, 4.24) * mm, "end": v(27.56, 4.25) * mm});
            skLineSegment(sketch, "E486", {"start": v(27.56, 4.25) * mm, "end": v(27.6, 4.27) * mm});
            skLineSegment(sketch, "E487", {"start": v(27.6, 4.27) * mm, "end": v(27.67, 4.28) * mm});
            skLineSegment(sketch, "E488", {"start": v(27.67, 4.28) * mm, "end": v(27.75, 4.3) * mm});
            skLineSegment(sketch, "E489", {"start": v(27.75, 4.3) * mm, "end": v(27.83, 4.33) * mm});
            skLineSegment(sketch, "E490", {"start": v(27.83, 4.33) * mm, "end": v(27.93, 4.37) * mm});
            skLineSegment(sketch, "E491", {"start": v(27.93, 4.37) * mm, "end": v(28.04, 4.4) * mm});
            skLineSegment(sketch, "E492", {"start": v(28.04, 4.4) * mm, "end": v(28.16, 4.45) * mm});
            skLineSegment(sketch, "E493", {"start": v(28.16, 4.45) * mm, "end": v(28.29, 4.5) * mm});
            skLineSegment(sketch, "E494", {"start": v(28.29, 4.5) * mm, "end": v(28.42, 4.57) * mm});
            skLineSegment(sketch, "E495", {"start": v(28.42, 4.57) * mm, "end": v(28.57, 4.63) * mm});
            skLineSegment(sketch, "E496", {"start": v(28.57, 4.63) * mm, "end": v(28.73, 4.71) * mm});
            skLineSegment(sketch, "E497", {"start": v(28.73, 4.71) * mm, "end": v(28.9, 4.8) * mm});
            skLineSegment(sketch, "E498", {"start": v(28.9, 4.8) * mm, "end": v(29.07, 4.9) * mm});
            skLineSegment(sketch, "E499", {"start": v(29.07, 4.9) * mm, "end": v(29.26, 5) * mm});
            skLineSegment(sketch, "E500", {"start": v(29.26, 5) * mm, "end": v(29.45, 5.11) * mm});
            skLineSegment(sketch, "E501", {"start": v(29.45, 5.11) * mm, "end": v(29.65, 5.24) * mm});
            skLineSegment(sketch, "E502", {"start": v(29.65, 5.24) * mm, "end": v(29.86, 5.37) * mm});
            skLineSegment(sketch, "E503", {"start": v(29.86, 5.37) * mm, "end": v(30.03, 5.49) * mm});
            skLineSegment(sketch, "E504", {"start": v(30.03, 5.49) * mm, "end": v(29.89, 6.35) * mm});
            skLineSegment(sketch, "E505", {"start": v(29.89, 6.35) * mm, "end": v(29.66, 7.2) * mm});
            skLineSegment(sketch, "E506", {"start": v(29.66, 7.2) * mm, "end": v(29.46, 7.23) * mm});
            skLineSegment(sketch, "E507", {"start": v(29.46, 7.23) * mm, "end": v(29.22, 7.28) * mm});
            skLineSegment(sketch, "E508", {"start": v(29.22, 7.28) * mm, "end": v(28.98, 7.3) * mm});
            skLineSegment(sketch, "E509", {"start": v(28.98, 7.3) * mm, "end": v(28.76, 7.33) * mm});
            skLineSegment(sketch, "E510", {"start": v(28.76, 7.33) * mm, "end": v(28.55, 7.36) * mm});
            skLineSegment(sketch, "E511", {"start": v(28.55, 7.36) * mm, "end": v(28.35, 7.37) * mm});
            skLineSegment(sketch, "E512", {"start": v(28.35, 7.37) * mm, "end": v(28.16, 7.38) * mm});
            skLineSegment(sketch, "E513", {"start": v(28.16, 7.38) * mm, "end": v(27.99, 7.39) * mm});
            skLineSegment(sketch, "E514", {"start": v(27.99, 7.39) * mm, "end": v(27.82, 7.4) * mm});
            skLineSegment(sketch, "E515", {"start": v(27.82, 7.4) * mm, "end": v(27.67, 7.39) * mm});
            skLineSegment(sketch, "E516", {"start": v(27.67, 7.39) * mm, "end": v(27.53, 7.39) * mm});
            skLineSegment(sketch, "E517", {"start": v(27.53, 7.39) * mm, "end": v(27.4, 7.38) * mm});
            skLineSegment(sketch, "E518", {"start": v(27.4, 7.38) * mm, "end": v(27.3, 7.37) * mm});
            skLineSegment(sketch, "E519", {"start": v(27.3, 7.37) * mm, "end": v(27.2, 7.36) * mm});
            skLineSegment(sketch, "E520", {"start": v(27.2, 7.36) * mm, "end": v(27.1, 7.35) * mm});
            skLineSegment(sketch, "E521", {"start": v(27.1, 7.35) * mm, "end": v(27.02, 7.34) * mm});
            skLineSegment(sketch, "E522", {"start": v(27.02, 7.34) * mm, "end": v(26.96, 7.33) * mm});
            skLineSegment(sketch, "E523", {"start": v(26.96, 7.33) * mm, "end": v(26.9, 7.32) * mm});
            skLineSegment(sketch, "E524", {"start": v(26.9, 7.32) * mm, "end": v(26.86, 7.32) * mm});
            skLineSegment(sketch, "E525", {"start": v(26.86, 7.32) * mm, "end": v(26.84, 7.3) * mm});
            skLineSegment(sketch, "E526", {"start": v(26.84, 7.3) * mm, "end": v(26.82, 7.3) * mm});
            skLineSegment(sketch, "E527", {"start": v(26.82, 7.3) * mm, "end": v(26.82, 7.3) * mm});
            skLineSegment(sketch, "E528", {"start": v(26.82, 7.3) * mm, "end": v(26.73, 7.28) * mm});
            skLineSegment(sketch, "E529", {"start": v(26.73, 7.28) * mm, "end": v(26.58, 7.24) * mm});
            skLineSegment(sketch, "E530", {"start": v(26.58, 7.24) * mm, "end": v(26.44, 7.2) * mm});
            skLineSegment(sketch, "E531", {"start": v(26.44, 7.2) * mm, "end": v(26.3, 7.18) * mm});
            skLineSegment(sketch, "E532", {"start": v(26.3, 7.18) * mm, "end": v(26.18, 7.17) * mm});
            skLineSegment(sketch, "E533", {"start": v(26.18, 7.17) * mm, "end": v(26.07, 7.16) * mm});
            skLineSegment(sketch, "E534", {"start": v(26.07, 7.16) * mm, "end": v(25.97, 7.16) * mm});
            skLineSegment(sketch, "E535", {"start": v(25.97, 7.16) * mm, "end": v(25.88, 7.17) * mm});
            skLineSegment(sketch, "E536", {"start": v(25.88, 7.17) * mm, "end": v(25.8, 7.18) * mm});
            skLineSegment(sketch, "E537", {"start": v(25.8, 7.18) * mm, "end": v(25.74, 7.2) * mm});
            skLineSegment(sketch, "E538", {"start": v(25.74, 7.2) * mm, "end": v(25.69, 7.23) * mm});
            skLineSegment(sketch, "E539", {"start": v(25.69, 7.23) * mm, "end": v(25.65, 7.26) * mm});
            skLineSegment(sketch, "E540", {"start": v(25.65, 7.26) * mm, "end": v(25.62, 7.3) * mm});
            skLineSegment(sketch, "E541", {"start": v(25.62, 7.3) * mm, "end": v(25.6, 7.33) * mm});
            skLineSegment(sketch, "E542", {"start": v(25.6, 7.33) * mm, "end": v(25.58, 7.43) * mm});
            skLineSegment(sketch, "E543", {"start": v(25.58, 7.43) * mm, "end": v(25.42, 7.97) * mm});
            skLineSegment(sketch, "E544", {"start": v(25.42, 7.97) * mm, "end": v(25.25, 8.5) * mm});
            skLineSegment(sketch, "E545", {"start": v(25.25, 8.5) * mm, "end": v(25.06, 9.02) * mm});
            skLineSegment(sketch, "E546", {"start": v(25.06, 9.02) * mm, "end": v(25.03, 9.12) * mm});
            skLineSegment(sketch, "E547", {"start": v(25.03, 9.12) * mm, "end": v(25.02, 9.16) * mm});
            skLineSegment(sketch, "E548", {"start": v(25.02, 9.16) * mm, "end": v(25.02, 9.2) * mm});
            skLineSegment(sketch, "E549", {"start": v(25.02, 9.2) * mm, "end": v(25.03, 9.25) * mm});
            skLineSegment(sketch, "E550", {"start": v(25.03, 9.25) * mm, "end": v(25.06, 9.3) * mm});
            skLineSegment(sketch, "E551", {"start": v(25.06, 9.3) * mm, "end": v(25.1, 9.36) * mm});
            skLineSegment(sketch, "E552", {"start": v(25.1, 9.36) * mm, "end": v(25.15, 9.41) * mm});
            skLineSegment(sketch, "E553", {"start": v(25.15, 9.41) * mm, "end": v(25.22, 9.47) * mm});
            skLineSegment(sketch, "E554", {"start": v(25.22, 9.47) * mm, "end": v(25.3, 9.53) * mm});
            skLineSegment(sketch, "E555", {"start": v(25.3, 9.53) * mm, "end": v(25.4, 9.6) * mm});
            skLineSegment(sketch, "E556", {"start": v(25.4, 9.6) * mm, "end": v(25.5, 9.65) * mm});
            skLineSegment(sketch, "E557", {"start": v(25.5, 9.65) * mm, "end": v(25.62, 9.71) * mm});
            skLineSegment(sketch, "E558", {"start": v(25.62, 9.71) * mm, "end": v(25.76, 9.77) * mm});
            skLineSegment(sketch, "E559", {"start": v(25.76, 9.77) * mm, "end": v(25.9, 9.82) * mm});
            skLineSegment(sketch, "E560", {"start": v(25.9, 9.82) * mm, "end": v(25.99, 9.85) * mm});
            skLineSegment(sketch, "E561", {"start": v(25.99, 9.85) * mm, "end": v(26, 9.85) * mm});
            skLineSegment(sketch, "E562", {"start": v(26, 9.85) * mm, "end": v(26, 9.86) * mm});
            skLineSegment(sketch, "E563", {"start": v(26, 9.86) * mm, "end": v(26.03, 9.87) * mm});
            skLineSegment(sketch, "E564", {"start": v(26.03, 9.87) * mm, "end": v(26.07, 9.89) * mm});
            skLineSegment(sketch, "E565", {"start": v(26.07, 9.89) * mm, "end": v(26.12, 9.91) * mm});
            skLineSegment(sketch, "E566", {"start": v(26.12, 9.91) * mm, "end": v(26.18, 9.94) * mm});
            skLineSegment(sketch, "E567", {"start": v(26.18, 9.94) * mm, "end": v(26.25, 9.98) * mm});
            skLineSegment(sketch, "E568", {"start": v(26.25, 9.98) * mm, "end": v(26.33, 10.03) * mm});
            skLineSegment(sketch, "E569", {"start": v(26.33, 10.03) * mm, "end": v(26.41, 10.08) * mm});
            skLineSegment(sketch, "E570", {"start": v(26.41, 10.08) * mm, "end": v(26.51, 10.14) * mm});
            skLineSegment(sketch, "E571", {"start": v(26.51, 10.14) * mm, "end": v(26.62, 10.2) * mm});
            skLineSegment(sketch, "E572", {"start": v(26.62, 10.2) * mm, "end": v(26.73, 10.29) * mm});
            skLineSegment(sketch, "E573", {"start": v(26.73, 10.29) * mm, "end": v(26.85, 10.38) * mm});
            skLineSegment(sketch, "E574", {"start": v(26.85, 10.38) * mm, "end": v(26.99, 10.47) * mm});
            skLineSegment(sketch, "E575", {"start": v(26.99, 10.47) * mm, "end": v(27.12, 10.58) * mm});
            skLineSegment(sketch, "E576", {"start": v(27.12, 10.58) * mm, "end": v(27.27, 10.7) * mm});
            skLineSegment(sketch, "E577", {"start": v(27.27, 10.7) * mm, "end": v(27.42, 10.83) * mm});
            skLineSegment(sketch, "E578", {"start": v(27.42, 10.83) * mm, "end": v(27.58, 10.97) * mm});
            skLineSegment(sketch, "E579", {"start": v(27.58, 10.97) * mm, "end": v(27.74, 11.12) * mm});
            skLineSegment(sketch, "E580", {"start": v(27.74, 11.12) * mm, "end": v(27.91, 11.29) * mm});
            skLineSegment(sketch, "E581", {"start": v(27.91, 11.29) * mm, "end": v(28.09, 11.47) * mm});
            skLineSegment(sketch, "E582", {"start": v(28.09, 11.47) * mm, "end": v(28.23, 11.61) * mm});
            skLineSegment(sketch, "E583", {"start": v(28.23, 11.61) * mm, "end": v(27.92, 12.43) * mm});
            skLineSegment(sketch, "E584", {"start": v(27.92, 12.43) * mm, "end": v(27.52, 13.2) * mm});
            skLineSegment(sketch, "E585", {"start": v(27.52, 13.2) * mm, "end": v(27.32, 13.2) * mm});
            skLineSegment(sketch, "E586", {"start": v(27.32, 13.2) * mm, "end": v(27.07, 13.2) * mm});
            skLineSegment(sketch, "E587", {"start": v(27.07, 13.2) * mm, "end": v(26.83, 13.17) * mm});
            skLineSegment(sketch, "E588", {"start": v(26.83, 13.17) * mm, "end": v(26.6, 13.15) * mm});
            skLineSegment(sketch, "E589", {"start": v(26.6, 13.15) * mm, "end": v(26.4, 13.13) * mm});
            skLineSegment(sketch, "E590", {"start": v(26.4, 13.13) * mm, "end": v(26.2, 13.1) * mm});
            skLineSegment(sketch, "E591", {"start": v(26.2, 13.1) * mm, "end": v(26.01, 13.08) * mm});
            skLineSegment(sketch, "E592", {"start": v(26.01, 13.08) * mm, "end": v(25.84, 13.05) * mm});
            skLineSegment(sketch, "E593", {"start": v(25.84, 13.05) * mm, "end": v(25.68, 13.01) * mm});
            skLineSegment(sketch, "E594", {"start": v(25.68, 13.01) * mm, "end": v(25.53, 12.98) * mm});
            skLineSegment(sketch, "E595", {"start": v(25.53, 12.98) * mm, "end": v(25.4, 12.95) * mm});
            skLineSegment(sketch, "E596", {"start": v(25.4, 12.95) * mm, "end": v(25.27, 12.92) * mm});
            skLineSegment(sketch, "E597", {"start": v(25.27, 12.92) * mm, "end": v(25.16, 12.89) * mm});
            skLineSegment(sketch, "E598", {"start": v(25.16, 12.89) * mm, "end": v(25.07, 12.86) * mm});
            skLineSegment(sketch, "E599", {"start": v(25.07, 12.86) * mm, "end": v(24.98, 12.83) * mm});
            skLineSegment(sketch, "E600", {"start": v(24.98, 12.83) * mm, "end": v(24.9, 12.8) * mm});
            skLineSegment(sketch, "E601", {"start": v(24.9, 12.8) * mm, "end": v(24.84, 12.78) * mm});
            skLineSegment(sketch, "E602", {"start": v(24.84, 12.78) * mm, "end": v(24.8, 12.76) * mm});
            skLineSegment(sketch, "E603", {"start": v(24.8, 12.76) * mm, "end": v(24.76, 12.74) * mm});
            skLineSegment(sketch, "E604", {"start": v(24.76, 12.74) * mm, "end": v(24.73, 12.73) * mm});
            skLineSegment(sketch, "E605", {"start": v(24.73, 12.73) * mm, "end": v(24.71, 12.72) * mm});
            skLineSegment(sketch, "E606", {"start": v(24.71, 12.72) * mm, "end": v(24.71, 12.72) * mm});
            skLineSegment(sketch, "E607", {"start": v(24.71, 12.72) * mm, "end": v(24.64, 12.68) * mm});
            skLineSegment(sketch, "E608", {"start": v(24.64, 12.68) * mm, "end": v(24.5, 12.6) * mm});
            skLineSegment(sketch, "E609", {"start": v(24.5, 12.6) * mm, "end": v(24.36, 12.54) * mm});
            skLineSegment(sketch, "E610", {"start": v(24.36, 12.54) * mm, "end": v(24.24, 12.5) * mm});
            skLineSegment(sketch, "E611", {"start": v(24.24, 12.5) * mm, "end": v(24.12, 12.45) * mm});
            skLineSegment(sketch, "E612", {"start": v(24.12, 12.45) * mm, "end": v(24.01, 12.42) * mm});
            skLineSegment(sketch, "E613", {"start": v(24.01, 12.42) * mm, "end": v(23.92, 12.4) * mm});
            skLineSegment(sketch, "E614", {"start": v(23.92, 12.4) * mm, "end": v(23.83, 12.4) * mm});
            skLineSegment(sketch, "E615", {"start": v(23.83, 12.4) * mm, "end": v(23.75, 12.4) * mm});
            skLineSegment(sketch, "E616", {"start": v(23.75, 12.4) * mm, "end": v(23.68, 12.4) * mm});
            skLineSegment(sketch, "E617", {"start": v(23.68, 12.4) * mm, "end": v(23.63, 12.41) * mm});
            skLineSegment(sketch, "E618", {"start": v(23.63, 12.41) * mm, "end": v(23.58, 12.43) * mm});
            skLineSegment(sketch, "E619", {"start": v(23.58, 12.43) * mm, "end": v(23.55, 12.46) * mm});
            skLineSegment(sketch, "E620", {"start": v(23.55, 12.46) * mm, "end": v(23.52, 12.5) * mm});
            skLineSegment(sketch, "E621", {"start": v(23.52, 12.5) * mm, "end": v(23.48, 12.59) * mm});
            skLineSegment(sketch, "E622", {"start": v(23.48, 12.59) * mm, "end": v(23.2, 13.08) * mm});
            skLineSegment(sketch, "E623", {"start": v(23.2, 13.08) * mm, "end": v(22.93, 13.56) * mm});
            skLineSegment(sketch, "E624", {"start": v(22.93, 13.56) * mm, "end": v(22.64, 14.04) * mm});
            skLineSegment(sketch, "E625", {"start": v(22.64, 14.04) * mm, "end": v(22.59, 14.12) * mm});
            skLineSegment(sketch, "E626", {"start": v(22.59, 14.12) * mm, "end": v(22.57, 14.16) * mm});
            skLineSegment(sketch, "E627", {"start": v(22.57, 14.16) * mm, "end": v(22.56, 14.2) * mm});
            skLineSegment(sketch, "E628", {"start": v(22.56, 14.2) * mm, "end": v(22.56, 14.25) * mm});
            skLineSegment(sketch, "E629", {"start": v(22.56, 14.25) * mm, "end": v(22.58, 14.31) * mm});
            skLineSegment(sketch, "E630", {"start": v(22.58, 14.31) * mm, "end": v(22.6, 14.37) * mm});
            skLineSegment(sketch, "E631", {"start": v(22.6, 14.37) * mm, "end": v(22.65, 14.44) * mm});
            skLineSegment(sketch, "E632", {"start": v(22.65, 14.44) * mm, "end": v(22.7, 14.5) * mm});
            skLineSegment(sketch, "E633", {"start": v(22.7, 14.5) * mm, "end": v(22.77, 14.58) * mm});
            skLineSegment(sketch, "E634", {"start": v(22.77, 14.58) * mm, "end": v(22.84, 14.66) * mm});
            skLineSegment(sketch, "E635", {"start": v(22.84, 14.66) * mm, "end": v(22.94, 14.74) * mm});
            skLineSegment(sketch, "E636", {"start": v(22.94, 14.74) * mm, "end": v(23.04, 14.83) * mm});
            skLineSegment(sketch, "E637", {"start": v(23.04, 14.83) * mm, "end": v(23.16, 14.91) * mm});
            skLineSegment(sketch, "E638", {"start": v(23.16, 14.91) * mm, "end": v(23.3, 15) * mm});
            skLineSegment(sketch, "E639", {"start": v(23.3, 15) * mm, "end": v(23.37, 15.04) * mm});
            skLineSegment(sketch, "E640", {"start": v(23.37, 15.04) * mm, "end": v(23.37, 15.04) * mm});
            skLineSegment(sketch, "E641", {"start": v(23.37, 15.04) * mm, "end": v(23.39, 15.05) * mm});
            skLineSegment(sketch, "E642", {"start": v(23.39, 15.05) * mm, "end": v(23.41, 15.07) * mm});
            skLineSegment(sketch, "E643", {"start": v(23.41, 15.07) * mm, "end": v(23.45, 15.1) * mm});
            skLineSegment(sketch, "E644", {"start": v(23.45, 15.1) * mm, "end": v(23.49, 15.13) * mm});
            skLineSegment(sketch, "E645", {"start": v(23.49, 15.13) * mm, "end": v(23.54, 15.17) * mm});
            skLineSegment(sketch, "E646", {"start": v(23.54, 15.17) * mm, "end": v(23.6, 15.22) * mm});
            skLineSegment(sketch, "E647", {"start": v(23.6, 15.22) * mm, "end": v(23.67, 15.28) * mm});
            skLineSegment(sketch, "E648", {"start": v(23.67, 15.28) * mm, "end": v(23.74, 15.35) * mm});
            skLineSegment(sketch, "E649", {"start": v(23.74, 15.35) * mm, "end": v(23.82, 15.43) * mm});
            skLineSegment(sketch, "E650", {"start": v(23.82, 15.43) * mm, "end": v(23.91, 15.52) * mm});
            skLineSegment(sketch, "E651", {"start": v(23.91, 15.52) * mm, "end": v(24, 15.62) * mm});
            skLineSegment(sketch, "E652", {"start": v(24, 15.62) * mm, "end": v(24.11, 15.73) * mm});
            skLineSegment(sketch, "E653", {"start": v(24.11, 15.73) * mm, "end": v(24.22, 15.85) * mm});
            skLineSegment(sketch, "E654", {"start": v(24.22, 15.85) * mm, "end": v(24.33, 15.99) * mm});
            skLineSegment(sketch, "E655", {"start": v(24.33, 15.99) * mm, "end": v(24.45, 16.14) * mm});
            skLineSegment(sketch, "E656", {"start": v(24.45, 16.14) * mm, "end": v(24.57, 16.3) * mm});
            skLineSegment(sketch, "E657", {"start": v(24.57, 16.3) * mm, "end": v(24.7, 16.47) * mm});
            skLineSegment(sketch, "E658", {"start": v(24.7, 16.47) * mm, "end": v(24.83, 16.65) * mm});
            skLineSegment(sketch, "E659", {"start": v(24.83, 16.65) * mm, "end": v(24.96, 16.85) * mm});
            skLineSegment(sketch, "E660", {"start": v(24.96, 16.85) * mm, "end": v(25.1, 17.05) * mm});
            skLineSegment(sketch, "E661", {"start": v(25.1, 17.05) * mm, "end": v(25.2, 17.23) * mm});
            skLineSegment(sketch, "E662", {"start": v(25.2, 17.23) * mm, "end": v(24.72, 17.96) * mm});
            skLineSegment(sketch, "E663", {"start": v(24.72, 17.96) * mm, "end": v(24.17, 18.64) * mm});
            skLineSegment(sketch, "E664", {"start": v(24.17, 18.64) * mm, "end": v(23.97, 18.6) * mm});
            skLineSegment(sketch, "E665", {"start": v(23.97, 18.6) * mm, "end": v(23.73, 18.53) * mm});
            skLineSegment(sketch, "E666", {"start": v(23.73, 18.53) * mm, "end": v(23.5, 18.47) * mm});
            skLineSegment(sketch, "E667", {"start": v(23.5, 18.47) * mm, "end": v(23.3, 18.4) * mm});
            skLineSegment(sketch, "E668", {"start": v(23.3, 18.4) * mm, "end": v(23.09, 18.33) * mm});
            skLineSegment(sketch, "E669", {"start": v(23.09, 18.33) * mm, "end": v(22.9, 18.27) * mm});
            skLineSegment(sketch, "E670", {"start": v(22.9, 18.27) * mm, "end": v(22.73, 18.2) * mm});
            skLineSegment(sketch, "E671", {"start": v(22.73, 18.2) * mm, "end": v(22.56, 18.13) * mm});
            skLineSegment(sketch, "E672", {"start": v(22.56, 18.13) * mm, "end": v(22.41, 18.07) * mm});
            skLineSegment(sketch, "E673", {"start": v(22.41, 18.07) * mm, "end": v(22.27, 18) * mm});
            skLineSegment(sketch, "E674", {"start": v(22.27, 18) * mm, "end": v(22.15, 17.95) * mm});
            skLineSegment(sketch, "E675", {"start": v(22.15, 17.95) * mm, "end": v(22.04, 17.89) * mm});
            skLineSegment(sketch, "E676", {"start": v(22.04, 17.89) * mm, "end": v(21.93, 17.84) * mm});
            skLineSegment(sketch, "E677", {"start": v(21.93, 17.84) * mm, "end": v(21.84, 17.79) * mm});
            skLineSegment(sketch, "E678", {"start": v(21.84, 17.79) * mm, "end": v(21.77, 17.74) * mm});
            skLineSegment(sketch, "E679", {"start": v(21.77, 17.74) * mm, "end": v(21.7, 17.7) * mm});
            skLineSegment(sketch, "E680", {"start": v(21.7, 17.7) * mm, "end": v(21.64, 17.66) * mm});
            skLineSegment(sketch, "E681", {"start": v(21.64, 17.66) * mm, "end": v(21.6, 17.63) * mm});
            skLineSegment(sketch, "E682", {"start": v(21.6, 17.63) * mm, "end": v(21.57, 17.6) * mm});
            skLineSegment(sketch, "E683", {"start": v(21.57, 17.6) * mm, "end": v(21.54, 17.6) * mm});
            skLineSegment(sketch, "E684", {"start": v(21.54, 17.6) * mm, "end": v(21.53, 17.58) * mm});
            skLineSegment(sketch, "E685", {"start": v(21.53, 17.58) * mm, "end": v(21.53, 17.58) * mm});
            skLineSegment(sketch, "E686", {"start": v(21.53, 17.58) * mm, "end": v(21.46, 17.52) * mm});
            skLineSegment(sketch, "E687", {"start": v(21.46, 17.52) * mm, "end": v(21.34, 17.42) * mm});
            skLineSegment(sketch, "E688", {"start": v(21.34, 17.42) * mm, "end": v(21.22, 17.33) * mm});
            skLineSegment(sketch, "E689", {"start": v(21.22, 17.33) * mm, "end": v(21.1, 17.26) * mm});
            skLineSegment(sketch, "E690", {"start": v(21.1, 17.26) * mm, "end": v(21, 17.2) * mm});
            skLineSegment(sketch, "E691", {"start": v(21, 17.2) * mm, "end": v(20.9, 17.14) * mm});
            skLineSegment(sketch, "E692", {"start": v(20.9, 17.14) * mm, "end": v(20.81, 17.1) * mm});
            skLineSegment(sketch, "E693", {"start": v(20.81, 17.1) * mm, "end": v(20.73, 17.08) * mm});
            skLineSegment(sketch, "E694", {"start": v(20.73, 17.08) * mm, "end": v(20.65, 17.06) * mm});
            skLineSegment(sketch, "E695", {"start": v(20.65, 17.06) * mm, "end": v(20.59, 17.05) * mm});
            skLineSegment(sketch, "E696", {"start": v(20.59, 17.05) * mm, "end": v(20.53, 17.05) * mm});
            skLineSegment(sketch, "E697", {"start": v(20.53, 17.05) * mm, "end": v(20.48, 17.06) * mm});
            skLineSegment(sketch, "E698", {"start": v(20.48, 17.06) * mm, "end": v(20.44, 17.09) * mm});
            skLineSegment(sketch, "E699", {"start": v(20.44, 17.09) * mm, "end": v(20.41, 17.12) * mm});
            skLineSegment(sketch, "E700", {"start": v(20.41, 17.12) * mm, "end": v(20.35, 17.2) * mm});
            skLineSegment(sketch, "E701", {"start": v(20.35, 17.2) * mm, "end": v(19.98, 17.62) * mm});
            skLineSegment(sketch, "E702", {"start": v(19.98, 17.62) * mm, "end": v(19.6, 18.03) * mm});
            skLineSegment(sketch, "E703", {"start": v(19.6, 18.03) * mm, "end": v(19.23, 18.44) * mm});
            skLineSegment(sketch, "E704", {"start": v(19.23, 18.44) * mm, "end": v(19.16, 18.51) * mm});
            skLineSegment(sketch, "E705", {"start": v(19.16, 18.51) * mm, "end": v(19.13, 18.54) * mm});
            skLineSegment(sketch, "E706", {"start": v(19.13, 18.54) * mm, "end": v(19.11, 18.58) * mm});
            skLineSegment(sketch, "E707", {"start": v(19.11, 18.58) * mm, "end": v(19.1, 18.63) * mm});
            skLineSegment(sketch, "E708", {"start": v(19.1, 18.63) * mm, "end": v(19.1, 18.7) * mm});
            skLineSegment(sketch, "E709", {"start": v(19.1, 18.7) * mm, "end": v(19.12, 18.76) * mm});
            skLineSegment(sketch, "E710", {"start": v(19.12, 18.76) * mm, "end": v(19.15, 18.83) * mm});
            skLineSegment(sketch, "E711", {"start": v(19.15, 18.83) * mm, "end": v(19.19, 18.91) * mm});
            skLineSegment(sketch, "E712", {"start": v(19.19, 18.91) * mm, "end": v(19.24, 19) * mm});
            skLineSegment(sketch, "E713", {"start": v(19.24, 19) * mm, "end": v(19.3, 19.1) * mm});
            skLineSegment(sketch, "E714", {"start": v(19.3, 19.1) * mm, "end": v(19.37, 19.19) * mm});
            skLineSegment(sketch, "E715", {"start": v(19.37, 19.19) * mm, "end": v(19.46, 19.3) * mm});
            skLineSegment(sketch, "E716", {"start": v(19.46, 19.3) * mm, "end": v(19.56, 19.4) * mm});
            skLineSegment(sketch, "E717", {"start": v(19.56, 19.4) * mm, "end": v(19.67, 19.51) * mm});
            skLineSegment(sketch, "E718", {"start": v(19.67, 19.51) * mm, "end": v(19.73, 19.57) * mm});
            skLineSegment(sketch, "E719", {"start": v(19.73, 19.57) * mm, "end": v(19.74, 19.57) * mm});
            skLineSegment(sketch, "E720", {"start": v(19.74, 19.57) * mm, "end": v(19.75, 19.59) * mm});
            skLineSegment(sketch, "E721", {"start": v(19.75, 19.59) * mm, "end": v(19.77, 19.6) * mm});
            skLineSegment(sketch, "E722", {"start": v(19.77, 19.6) * mm, "end": v(19.8, 19.64) * mm});
            skLineSegment(sketch, "E723", {"start": v(19.8, 19.64) * mm, "end": v(19.83, 19.68) * mm});
            skLineSegment(sketch, "E724", {"start": v(19.83, 19.68) * mm, "end": v(19.87, 19.73) * mm});
            skLineSegment(sketch, "E725", {"start": v(19.87, 19.73) * mm, "end": v(19.92, 19.8) * mm});
            skLineSegment(sketch, "E726", {"start": v(19.92, 19.8) * mm, "end": v(19.97, 19.87) * mm});
            skLineSegment(sketch, "E727", {"start": v(19.97, 19.87) * mm, "end": v(20.03, 19.95) * mm});
            skLineSegment(sketch, "E728", {"start": v(20.03, 19.95) * mm, "end": v(20.1, 20.04) * mm});
            skLineSegment(sketch, "E729", {"start": v(20.1, 20.04) * mm, "end": v(20.16, 20.15) * mm});
            skLineSegment(sketch, "E730", {"start": v(20.16, 20.15) * mm, "end": v(20.24, 20.27) * mm});
            skLineSegment(sketch, "E731", {"start": v(20.24, 20.27) * mm, "end": v(20.31, 20.4) * mm});
            skLineSegment(sketch, "E732", {"start": v(20.31, 20.4) * mm, "end": v(20.4, 20.54) * mm});
            skLineSegment(sketch, "E733", {"start": v(20.4, 20.54) * mm, "end": v(20.47, 20.7) * mm});
            skLineSegment(sketch, "E734", {"start": v(20.47, 20.7) * mm, "end": v(20.56, 20.87) * mm});
            skLineSegment(sketch, "E735", {"start": v(20.56, 20.87) * mm, "end": v(20.65, 21.05) * mm});
            skLineSegment(sketch, "E736", {"start": v(20.65, 21.05) * mm, "end": v(20.73, 21.24) * mm});
            skLineSegment(sketch, "E737", {"start": v(20.73, 21.24) * mm, "end": v(20.82, 21.45) * mm});
            skLineSegment(sketch, "E738", {"start": v(20.82, 21.45) * mm, "end": v(20.9, 21.67) * mm});
            skLineSegment(sketch, "E739", {"start": v(20.9, 21.67) * mm, "end": v(21, 21.9) * mm});
            skLineSegment(sketch, "E740", {"start": v(21, 21.9) * mm, "end": v(21.07, 22.1) * mm});
            skLineSegment(sketch, "E741", {"start": v(21.07, 22.1) * mm, "end": v(20.45, 22.7) * mm});
            skLineSegment(sketch, "E742", {"start": v(20.45, 22.7) * mm, "end": v(19.77, 23.26) * mm});
            skLineSegment(sketch, "E743", {"start": v(19.77, 23.26) * mm, "end": v(19.58, 23.17) * mm});
            skLineSegment(sketch, "E744", {"start": v(19.58, 23.17) * mm, "end": v(19.36, 23.06) * mm});
            skLineSegment(sketch, "E745", {"start": v(19.36, 23.06) * mm, "end": v(19.15, 22.95) * mm});
            skLineSegment(sketch, "E746", {"start": v(19.15, 22.95) * mm, "end": v(18.96, 22.84) * mm});
            skLineSegment(sketch, "E747", {"start": v(18.96, 22.84) * mm, "end": v(18.77, 22.73) * mm});
            skLineSegment(sketch, "E748", {"start": v(18.77, 22.73) * mm, "end": v(18.6, 22.63) * mm});
            skLineSegment(sketch, "E749", {"start": v(18.6, 22.63) * mm, "end": v(18.45, 22.53) * mm});
            skLineSegment(sketch, "E750", {"start": v(18.45, 22.53) * mm, "end": v(18.3, 22.43) * mm});
            skLineSegment(sketch, "E751", {"start": v(18.3, 22.43) * mm, "end": v(18.17, 22.33) * mm});
            skLineSegment(sketch, "E752", {"start": v(18.17, 22.33) * mm, "end": v(18.04, 22.24) * mm});
            skLineSegment(sketch, "E753", {"start": v(18.04, 22.24) * mm, "end": v(17.93, 22.16) * mm});
            skLineSegment(sketch, "E754", {"start": v(17.93, 22.16) * mm, "end": v(17.83, 22.08) * mm});
            skLineSegment(sketch, "E755", {"start": v(17.83, 22.08) * mm, "end": v(17.75, 22) * mm});
            skLineSegment(sketch, "E756", {"start": v(17.75, 22) * mm, "end": v(17.67, 21.94) * mm});
            skLineSegment(sketch, "E757", {"start": v(17.67, 21.94) * mm, "end": v(17.6, 21.88) * mm});
            skLineSegment(sketch, "E758", {"start": v(17.6, 21.88) * mm, "end": v(17.55, 21.82) * mm});
            skLineSegment(sketch, "E759", {"start": v(17.55, 21.82) * mm, "end": v(17.5, 21.78) * mm});
            skLineSegment(sketch, "E760", {"start": v(17.5, 21.78) * mm, "end": v(17.46, 21.74) * mm});
            skLineSegment(sketch, "E761", {"start": v(17.46, 21.74) * mm, "end": v(17.43, 21.7) * mm});
            skLineSegment(sketch, "E762", {"start": v(17.43, 21.7) * mm, "end": v(17.41, 21.69) * mm});
            skLineSegment(sketch, "E763", {"start": v(17.41, 21.69) * mm, "end": v(17.4, 21.67) * mm});
            skLineSegment(sketch, "E764", {"start": v(17.4, 21.67) * mm, "end": v(17.4, 21.67) * mm});
            skLineSegment(sketch, "E765", {"start": v(17.4, 21.67) * mm, "end": v(17.35, 21.6) * mm});
            skLineSegment(sketch, "E766", {"start": v(17.35, 21.6) * mm, "end": v(17.25, 21.48) * mm});
            skLineSegment(sketch, "E767", {"start": v(17.25, 21.48) * mm, "end": v(17.15, 21.37) * mm});
            skLineSegment(sketch, "E768", {"start": v(17.15, 21.37) * mm, "end": v(17.06, 21.27) * mm});
            skLineSegment(sketch, "E769", {"start": v(17.06, 21.27) * mm, "end": v(16.97, 21.19) * mm});
            skLineSegment(sketch, "E770", {"start": v(16.97, 21.19) * mm, "end": v(16.88, 21.12) * mm});
            skLineSegment(sketch, "E771", {"start": v(16.88, 21.12) * mm, "end": v(16.8, 21.06) * mm});
            skLineSegment(sketch, "E772", {"start": v(16.8, 21.06) * mm, "end": v(16.73, 21.01) * mm});
            skLineSegment(sketch, "E773", {"start": v(16.73, 21.01) * mm, "end": v(16.66, 20.98) * mm});
            skLineSegment(sketch, "E774", {"start": v(16.66, 20.98) * mm, "end": v(16.6, 20.96) * mm});
            skLineSegment(sketch, "E775", {"start": v(16.6, 20.96) * mm, "end": v(16.54, 20.95) * mm});
            skLineSegment(sketch, "E776", {"start": v(16.54, 20.95) * mm, "end": v(16.48, 20.95) * mm});
            skLineSegment(sketch, "E777", {"start": v(16.48, 20.95) * mm, "end": v(16.44, 20.96) * mm});
            skLineSegment(sketch, "E778", {"start": v(16.44, 20.96) * mm, "end": v(16.4, 20.99) * mm});
            skLineSegment(sketch, "E779", {"start": v(16.4, 20.99) * mm, "end": v(16.33, 21.05) * mm});
            skLineSegment(sketch, "E780", {"start": v(16.33, 21.05) * mm, "end": v(15.88, 21.39) * mm});
            skLineSegment(sketch, "E781", {"start": v(15.88, 21.39) * mm, "end": v(15.43, 21.71) * mm});
            skLineSegment(sketch, "E782", {"start": v(15.43, 21.71) * mm, "end": v(14.97, 22.03) * mm});
            skLineSegment(sketch, "E783", {"start": v(14.97, 22.03) * mm, "end": v(14.89, 22.09) * mm});
            skLineSegment(sketch, "E784", {"start": v(14.89, 22.09) * mm, "end": v(14.86, 22.11) * mm});
            skLineSegment(sketch, "E785", {"start": v(14.86, 22.11) * mm, "end": v(14.83, 22.15) * mm});
            skLineSegment(sketch, "E786", {"start": v(14.83, 22.15) * mm, "end": v(14.81, 22.2) * mm});
            skLineSegment(sketch, "E787", {"start": v(14.81, 22.2) * mm, "end": v(14.8, 22.26) * mm});
            skLineSegment(sketch, "E788", {"start": v(14.8, 22.26) * mm, "end": v(14.8, 22.32) * mm});
            skLineSegment(sketch, "E789", {"start": v(14.8, 22.32) * mm, "end": v(14.81, 22.4) * mm});
            skLineSegment(sketch, "E790", {"start": v(14.81, 22.4) * mm, "end": v(14.83, 22.49) * mm});
            skLineSegment(sketch, "E791", {"start": v(14.83, 22.49) * mm, "end": v(14.87, 22.58) * mm});
            skLineSegment(sketch, "E792", {"start": v(14.87, 22.58) * mm, "end": v(14.9, 22.69) * mm});
            skLineSegment(sketch, "E793", {"start": v(14.9, 22.69) * mm, "end": v(14.96, 22.8) * mm});
            skLineSegment(sketch, "E794", {"start": v(14.96, 22.8) * mm, "end": v(15.02, 22.92) * mm});
            skLineSegment(sketch, "E795", {"start": v(15.02, 22.92) * mm, "end": v(15.1, 23.04) * mm});
            skLineSegment(sketch, "E796", {"start": v(15.1, 23.04) * mm, "end": v(15.18, 23.18) * mm});
            skLineSegment(sketch, "E797", {"start": v(15.18, 23.18) * mm, "end": v(15.23, 23.25) * mm});
            skLineSegment(sketch, "E798", {"start": v(15.23, 23.25) * mm, "end": v(15.23, 23.25) * mm});
            skLineSegment(sketch, "E799", {"start": v(15.23, 23.25) * mm, "end": v(15.24, 23.26) * mm});
            skLineSegment(sketch, "E800", {"start": v(15.24, 23.26) * mm, "end": v(15.26, 23.29) * mm});
            skLineSegment(sketch, "E801", {"start": v(15.26, 23.29) * mm, "end": v(15.28, 23.32) * mm});
            skLineSegment(sketch, "E802", {"start": v(15.28, 23.32) * mm, "end": v(15.3, 23.37) * mm});
            skLineSegment(sketch, "E803", {"start": v(15.3, 23.37) * mm, "end": v(15.33, 23.43) * mm});
            skLineSegment(sketch, "E804", {"start": v(15.33, 23.43) * mm, "end": v(15.37, 23.5) * mm});
            skLineSegment(sketch, "E805", {"start": v(15.37, 23.5) * mm, "end": v(15.4, 23.58) * mm});
            skLineSegment(sketch, "E806", {"start": v(15.4, 23.58) * mm, "end": v(15.45, 23.68) * mm});
            skLineSegment(sketch, "E807", {"start": v(15.45, 23.68) * mm, "end": v(15.49, 23.78) * mm});
            skLineSegment(sketch, "E808", {"start": v(15.49, 23.78) * mm, "end": v(15.53, 23.9) * mm});
            skLineSegment(sketch, "E809", {"start": v(15.53, 23.9) * mm, "end": v(15.58, 24.03) * mm});
            skLineSegment(sketch, "E810", {"start": v(15.58, 24.03) * mm, "end": v(15.63, 24.18) * mm});
            skLineSegment(sketch, "E811", {"start": v(15.63, 24.18) * mm, "end": v(15.68, 24.33) * mm});
            skLineSegment(sketch, "E812", {"start": v(15.68, 24.33) * mm, "end": v(15.72, 24.5) * mm});
            skLineSegment(sketch, "E813", {"start": v(15.72, 24.5) * mm, "end": v(15.77, 24.69) * mm});
            skLineSegment(sketch, "E814", {"start": v(15.77, 24.69) * mm, "end": v(15.82, 24.88) * mm});
            skLineSegment(sketch, "E815", {"start": v(15.82, 24.88) * mm, "end": v(15.86, 25.09) * mm});
            skLineSegment(sketch, "E816", {"start": v(15.86, 25.09) * mm, "end": v(15.9, 25.3) * mm});
            skLineSegment(sketch, "E817", {"start": v(15.9, 25.3) * mm, "end": v(15.95, 25.54) * mm});
            skLineSegment(sketch, "E818", {"start": v(15.95, 25.54) * mm, "end": v(15.99, 25.79) * mm});
            skLineSegment(sketch, "E819", {"start": v(15.99, 25.79) * mm, "end": v(16.01, 25.99) * mm});
            skLineSegment(sketch, "E820", {"start": v(16.01, 25.99) * mm, "end": v(15.28, 26.46) * mm});
            skLineSegment(sketch, "E821", {"start": v(15.28, 26.46) * mm, "end": v(14.5, 26.86) * mm});
            skLineSegment(sketch, "E822", {"start": v(14.5, 26.86) * mm, "end": v(14.34, 26.74) * mm});
            skLineSegment(sketch, "E823", {"start": v(14.34, 26.74) * mm, "end": v(14.14, 26.58) * mm});
            skLineSegment(sketch, "E824", {"start": v(14.14, 26.58) * mm, "end": v(13.96, 26.43) * mm});
            skLineSegment(sketch, "E825", {"start": v(13.96, 26.43) * mm, "end": v(13.8, 26.28) * mm});
            skLineSegment(sketch, "E826", {"start": v(13.8, 26.28) * mm, "end": v(13.64, 26.14) * mm});
            skLineSegment(sketch, "E827", {"start": v(13.64, 26.14) * mm, "end": v(13.5, 26) * mm});
            skLineSegment(sketch, "E828", {"start": v(13.5, 26) * mm, "end": v(13.36, 25.87) * mm});
            skLineSegment(sketch, "E829", {"start": v(13.36, 25.87) * mm, "end": v(13.24, 25.74) * mm});
            skLineSegment(sketch, "E830", {"start": v(13.24, 25.74) * mm, "end": v(13.13, 25.62) * mm});
            skLineSegment(sketch, "E831", {"start": v(13.13, 25.62) * mm, "end": v(13.02, 25.5) * mm});
            skLineSegment(sketch, "E832", {"start": v(13.02, 25.5) * mm, "end": v(12.93, 25.4) * mm});
            skLineSegment(sketch, "E833", {"start": v(12.93, 25.4) * mm, "end": v(12.85, 25.3) * mm});
            skLineSegment(sketch, "E834", {"start": v(12.85, 25.3) * mm, "end": v(12.78, 25.22) * mm});
            skLineSegment(sketch, "E835", {"start": v(12.78, 25.22) * mm, "end": v(12.72, 25.13) * mm});
            skLineSegment(sketch, "E836", {"start": v(12.72, 25.13) * mm, "end": v(12.67, 25.06) * mm});
            skLineSegment(sketch, "E837", {"start": v(12.67, 25.06) * mm, "end": v(12.63, 25) * mm});
            skLineSegment(sketch, "E838", {"start": v(12.63, 25) * mm, "end": v(12.59, 24.94) * mm});
            skLineSegment(sketch, "E839", {"start": v(12.59, 24.94) * mm, "end": v(12.56, 24.9) * mm});
            skLineSegment(sketch, "E840", {"start": v(12.56, 24.9) * mm, "end": v(12.54, 24.86) * mm});
            skLineSegment(sketch, "E841", {"start": v(12.54, 24.86) * mm, "end": v(12.52, 24.83) * mm});
            skLineSegment(sketch, "E842", {"start": v(12.52, 24.83) * mm, "end": v(12.52, 24.82) * mm});
            skLineSegment(sketch, "E843", {"start": v(12.52, 24.82) * mm, "end": v(12.52, 24.82) * mm});
            skLineSegment(sketch, "E844", {"start": v(12.52, 24.82) * mm, "end": v(12.48, 24.74) * mm});
            skLineSegment(sketch, "E845", {"start": v(12.48, 24.74) * mm, "end": v(12.4, 24.6) * mm});
            skLineSegment(sketch, "E846", {"start": v(12.4, 24.6) * mm, "end": v(12.34, 24.47) * mm});
            skLineSegment(sketch, "E847", {"start": v(12.34, 24.47) * mm, "end": v(12.26, 24.35) * mm});
            skLineSegment(sketch, "E848", {"start": v(12.26, 24.35) * mm, "end": v(12.2, 24.25) * mm});
            skLineSegment(sketch, "E849", {"start": v(12.2, 24.25) * mm, "end": v(12.12, 24.17) * mm});
            skLineSegment(sketch, "E850", {"start": v(12.12, 24.17) * mm, "end": v(12.06, 24.1) * mm});
            skLineSegment(sketch, "E851", {"start": v(12.06, 24.1) * mm, "end": v(12, 24.03) * mm});
            skLineSegment(sketch, "E852", {"start": v(12, 24.03) * mm, "end": v(11.93, 23.98) * mm});
            skLineSegment(sketch, "E853", {"start": v(11.93, 23.98) * mm, "end": v(11.87, 23.95) * mm});
            skLineSegment(sketch, "E854", {"start": v(11.87, 23.95) * mm, "end": v(11.82, 23.93) * mm});
            skLineSegment(sketch, "E855", {"start": v(11.82, 23.93) * mm, "end": v(11.77, 23.92) * mm});
            skLineSegment(sketch, "E856", {"start": v(11.77, 23.92) * mm, "end": v(11.72, 23.92) * mm});
            skLineSegment(sketch, "E857", {"start": v(11.72, 23.92) * mm, "end": v(11.69, 23.94) * mm});
            skLineSegment(sketch, "E858", {"start": v(11.69, 23.94) * mm, "end": v(11.6, 23.98) * mm});
            skLineSegment(sketch, "E859", {"start": v(11.6, 23.98) * mm, "end": v(11.09, 24.22) * mm});
            skLineSegment(sketch, "E860", {"start": v(11.09, 24.22) * mm, "end": v(10.58, 24.45) * mm});
            skLineSegment(sketch, "E861", {"start": v(10.58, 24.45) * mm, "end": v(10.07, 24.66) * mm});
            skLineSegment(sketch, "E862", {"start": v(10.07, 24.66) * mm, "end": v(9.97, 24.7) * mm});
            skLineSegment(sketch, "E863", {"start": v(9.97, 24.7) * mm, "end": v(9.93, 24.72) * mm});
            skLineSegment(sketch, "E864", {"start": v(9.93, 24.72) * mm, "end": v(9.9, 24.75) * mm});
            skLineSegment(sketch, "E865", {"start": v(9.9, 24.75) * mm, "end": v(9.87, 24.8) * mm});
            skLineSegment(sketch, "E866", {"start": v(9.87, 24.8) * mm, "end": v(9.85, 24.85) * mm});
            skLineSegment(sketch, "E867", {"start": v(9.85, 24.85) * mm, "end": v(9.84, 24.91) * mm});
            skLineSegment(sketch, "E868", {"start": v(9.84, 24.91) * mm, "end": v(9.83, 25) * mm});
            skLineSegment(sketch, "E869", {"start": v(9.83, 25) * mm, "end": v(9.84, 25.08) * mm});
            skLineSegment(sketch, "E870", {"start": v(9.84, 25.08) * mm, "end": v(9.85, 25.18) * mm});
            skLineSegment(sketch, "E871", {"start": v(9.85, 25.18) * mm, "end": v(9.86, 25.29) * mm});
            skLineSegment(sketch, "E872", {"start": v(9.86, 25.29) * mm, "end": v(9.9, 25.4) * mm});
            skLineSegment(sketch, "E873", {"start": v(9.9, 25.4) * mm, "end": v(9.93, 25.54) * mm});
            skLineSegment(sketch, "E874", {"start": v(9.93, 25.54) * mm, "end": v(9.98, 25.68) * mm});
            skLineSegment(sketch, "E875", {"start": v(9.98, 25.68) * mm, "end": v(10.03, 25.83) * mm});
            skLineSegment(sketch, "E876", {"start": v(10.03, 25.83) * mm, "end": v(10.07, 25.9) * mm});
            skLineSegment(sketch, "E877", {"start": v(10.07, 25.9) * mm, "end": v(10.07, 25.9) * mm});
            skLineSegment(sketch, "E878", {"start": v(10.07, 25.9) * mm, "end": v(10.07, 25.92) * mm});
            skLineSegment(sketch, "E879", {"start": v(10.07, 25.92) * mm, "end": v(10.08, 25.95) * mm});
            skLineSegment(sketch, "E880", {"start": v(10.08, 25.95) * mm, "end": v(10.1, 26) * mm});
            skLineSegment(sketch, "E881", {"start": v(10.1, 26) * mm, "end": v(10.11, 26.04) * mm});
            skLineSegment(sketch, "E882", {"start": v(10.11, 26.04) * mm, "end": v(10.13, 26.1) * mm});
            skLineSegment(sketch, "E883", {"start": v(10.13, 26.1) * mm, "end": v(10.15, 26.18) * mm});
            skLineSegment(sketch, "E884", {"start": v(10.15, 26.18) * mm, "end": v(10.16, 26.27) * mm});
            skLineSegment(sketch, "E885", {"start": v(10.16, 26.27) * mm, "end": v(10.18, 26.37) * mm});
            skLineSegment(sketch, "E886", {"start": v(10.18, 26.37) * mm, "end": v(10.2, 26.49) * mm});
            skLineSegment(sketch, "E887", {"start": v(10.2, 26.49) * mm, "end": v(10.22, 26.61) * mm});
            skLineSegment(sketch, "E888", {"start": v(10.22, 26.61) * mm, "end": v(10.24, 26.75) * mm});
            skLineSegment(sketch, "E889", {"start": v(10.24, 26.75) * mm, "end": v(10.26, 26.9) * mm});
            skLineSegment(sketch, "E890", {"start": v(10.26, 26.9) * mm, "end": v(10.27, 27.06) * mm});
            skLineSegment(sketch, "E891", {"start": v(10.27, 27.06) * mm, "end": v(10.29, 27.24) * mm});
            skLineSegment(sketch, "E892", {"start": v(10.29, 27.24) * mm, "end": v(10.3, 27.42) * mm});
            skLineSegment(sketch, "E893", {"start": v(10.3, 27.42) * mm, "end": v(10.3, 27.62) * mm});
            skLineSegment(sketch, "E894", {"start": v(10.3, 27.62) * mm, "end": v(10.3, 27.84) * mm});
            skLineSegment(sketch, "E895", {"start": v(10.3, 27.84) * mm, "end": v(10.3, 28.06) * mm});
            skLineSegment(sketch, "E896", {"start": v(10.3, 28.06) * mm, "end": v(10.29, 28.3) * mm});
            skLineSegment(sketch, "E897", {"start": v(10.29, 28.3) * mm, "end": v(10.28, 28.55) * mm});
            skLineSegment(sketch, "E898", {"start": v(10.28, 28.55) * mm, "end": v(10.26, 28.75) * mm});
            skLineSegment(sketch, "E899", {"start": v(10.26, 28.75) * mm, "end": v(9.44, 29.06) * mm});
            skLineSegment(sketch, "E900", {"start": v(9.44, 29.06) * mm, "end": v(8.6, 29.29) * mm});
            skLineSegment(sketch, "E901", {"start": v(8.6, 29.29) * mm, "end": v(8.47, 29.13) * mm});
            skLineSegment(sketch, "E902", {"start": v(8.47, 29.13) * mm, "end": v(8.3, 28.94) * mm});
            skLineSegment(sketch, "E903", {"start": v(8.3, 28.94) * mm, "end": v(8.16, 28.76) * mm});
            skLineSegment(sketch, "E904", {"start": v(8.16, 28.76) * mm, "end": v(8.03, 28.58) * mm});
            skLineSegment(sketch, "E905", {"start": v(8.03, 28.58) * mm, "end": v(7.9, 28.4) * mm});
            skLineSegment(sketch, "E906", {"start": v(7.9, 28.4) * mm, "end": v(7.8, 28.24) * mm});
            skLineSegment(sketch, "E907", {"start": v(7.8, 28.24) * mm, "end": v(7.69, 28.08) * mm});
            skLineSegment(sketch, "E908", {"start": v(7.69, 28.08) * mm, "end": v(7.6, 27.93) * mm});
            skLineSegment(sketch, "E909", {"start": v(7.6, 27.93) * mm, "end": v(7.51, 27.8) * mm});
            skLineSegment(sketch, "E910", {"start": v(7.51, 27.8) * mm, "end": v(7.44, 27.66) * mm});
            skLineSegment(sketch, "E911", {"start": v(7.44, 27.66) * mm, "end": v(7.37, 27.54) * mm});
            skLineSegment(sketch, "E912", {"start": v(7.37, 27.54) * mm, "end": v(7.31, 27.43) * mm});
            skLineSegment(sketch, "E913", {"start": v(7.31, 27.43) * mm, "end": v(7.26, 27.32) * mm});
            skLineSegment(sketch, "E914", {"start": v(7.26, 27.32) * mm, "end": v(7.22, 27.23) * mm});
            skLineSegment(sketch, "E915", {"start": v(7.22, 27.23) * mm, "end": v(7.18, 27.15) * mm});
            skLineSegment(sketch, "E916", {"start": v(7.18, 27.15) * mm, "end": v(7.15, 27.07) * mm});
            skLineSegment(sketch, "E917", {"start": v(7.15, 27.07) * mm, "end": v(7.13, 27.01) * mm});
            skLineSegment(sketch, "E918", {"start": v(7.13, 27.01) * mm, "end": v(7.11, 26.96) * mm});
            skLineSegment(sketch, "E919", {"start": v(7.11, 26.96) * mm, "end": v(7.1, 26.92) * mm});
            skLineSegment(sketch, "E920", {"start": v(7.1, 26.92) * mm, "end": v(7.09, 26.9) * mm});
            skLineSegment(sketch, "E921", {"start": v(7.09, 26.9) * mm, "end": v(7.08, 26.88) * mm});
            skLineSegment(sketch, "E922", {"start": v(7.08, 26.88) * mm, "end": v(7.08, 26.88) * mm});
            skLineSegment(sketch, "E923", {"start": v(7.08, 26.88) * mm, "end": v(7.06, 26.8) * mm});
            skLineSegment(sketch, "E924", {"start": v(7.06, 26.8) * mm, "end": v(7.02, 26.64) * mm});
            skLineSegment(sketch, "E925", {"start": v(7.02, 26.64) * mm, "end": v(6.98, 26.5) * mm});
            skLineSegment(sketch, "E926", {"start": v(6.98, 26.5) * mm, "end": v(6.93, 26.37) * mm});
            skLineSegment(sketch, "E927", {"start": v(6.93, 26.37) * mm, "end": v(6.88, 26.26) * mm});
            skLineSegment(sketch, "E928", {"start": v(6.88, 26.26) * mm, "end": v(6.84, 26.16) * mm});
            skLineSegment(sketch, "E929", {"start": v(6.84, 26.16) * mm, "end": v(6.78, 26.07) * mm});
            skLineSegment(sketch, "E930", {"start": v(6.78, 26.07) * mm, "end": v(6.73, 26) * mm});
            skLineSegment(sketch, "E931", {"start": v(6.73, 26) * mm, "end": v(6.68, 25.94) * mm});
            skLineSegment(sketch, "E932", {"start": v(6.68, 25.94) * mm, "end": v(6.63, 25.9) * mm});
            skLineSegment(sketch, "E933", {"start": v(6.63, 25.9) * mm, "end": v(6.59, 25.86) * mm});
            skLineSegment(sketch, "E934", {"start": v(6.59, 25.86) * mm, "end": v(6.54, 25.84) * mm});
            skLineSegment(sketch, "E935", {"start": v(6.54, 25.84) * mm, "end": v(6.5, 25.84) * mm});
            skLineSegment(sketch, "E936", {"start": v(6.5, 25.84) * mm, "end": v(6.45, 25.85) * mm});
            skLineSegment(sketch, "E937", {"start": v(6.45, 25.85) * mm, "end": v(6.35, 25.87) * mm});
            skLineSegment(sketch, "E938", {"start": v(6.35, 25.87) * mm, "end": v(5.81, 26) * mm});
            skLineSegment(sketch, "E939", {"start": v(5.81, 26) * mm, "end": v(5.27, 26.11) * mm});
            skLineSegment(sketch, "E940", {"start": v(5.27, 26.11) * mm, "end": v(4.72, 26.22) * mm});
            skLineSegment(sketch, "E941", {"start": v(4.72, 26.22) * mm, "end": v(4.62, 26.24) * mm});
            skLineSegment(sketch, "E942", {"start": v(4.62, 26.24) * mm, "end": v(4.58, 26.25) * mm});
            skLineSegment(sketch, "E943", {"start": v(4.58, 26.25) * mm, "end": v(4.54, 26.27) * mm});
            skLineSegment(sketch, "E944", {"start": v(4.54, 26.27) * mm, "end": v(4.5, 26.3) * mm});
            skLineSegment(sketch, "E945", {"start": v(4.5, 26.3) * mm, "end": v(4.47, 26.35) * mm});
            skLineSegment(sketch, "E946", {"start": v(4.47, 26.35) * mm, "end": v(4.44, 26.42) * mm});
            skLineSegment(sketch, "E947", {"start": v(4.44, 26.42) * mm, "end": v(4.42, 26.5) * mm});
            skLineSegment(sketch, "E948", {"start": v(4.42, 26.5) * mm, "end": v(4.4, 26.58) * mm});
            skLineSegment(sketch, "E949", {"start": v(4.4, 26.58) * mm, "end": v(4.4, 26.68) * mm});
            skLineSegment(sketch, "E950", {"start": v(4.4, 26.68) * mm, "end": v(4.4, 26.79) * mm});
            skLineSegment(sketch, "E951", {"start": v(4.4, 26.79) * mm, "end": v(4.4, 26.91) * mm});
            skLineSegment(sketch, "E952", {"start": v(4.4, 26.91) * mm, "end": v(4.4, 27.05) * mm});
            skLineSegment(sketch, "E953", {"start": v(4.4, 27.05) * mm, "end": v(4.42, 27.2) * mm});
            skLineSegment(sketch, "E954", {"start": v(4.42, 27.2) * mm, "end": v(4.44, 27.35) * mm});
            skLineSegment(sketch, "E955", {"start": v(4.44, 27.35) * mm, "end": v(4.46, 27.43) * mm});
            skLineSegment(sketch, "E956", {"start": v(4.46, 27.43) * mm, "end": v(4.46, 27.44) * mm});
            skLineSegment(sketch, "E957", {"start": v(4.46, 27.44) * mm, "end": v(4.46, 27.45) * mm});
            skLineSegment(sketch, "E958", {"start": v(4.46, 27.45) * mm, "end": v(4.47, 27.48) * mm});
            skLineSegment(sketch, "E959", {"start": v(4.47, 27.48) * mm, "end": v(4.47, 27.52) * mm});
            skLineSegment(sketch, "E960", {"start": v(4.47, 27.52) * mm, "end": v(4.47, 27.58) * mm});
            skLineSegment(sketch, "E961", {"start": v(4.47, 27.58) * mm, "end": v(4.48, 27.64) * mm});
            skLineSegment(sketch, "E962", {"start": v(4.48, 27.64) * mm, "end": v(4.48, 27.72) * mm});
            skLineSegment(sketch, "E963", {"start": v(4.48, 27.72) * mm, "end": v(4.48, 27.81) * mm});
            skLineSegment(sketch, "E964", {"start": v(4.48, 27.81) * mm, "end": v(4.48, 27.91) * mm});
            skLineSegment(sketch, "E965", {"start": v(4.48, 27.91) * mm, "end": v(4.47, 28.03) * mm});
            skLineSegment(sketch, "E966", {"start": v(4.47, 28.03) * mm, "end": v(4.47, 28.15) * mm});
            skLineSegment(sketch, "E967", {"start": v(4.47, 28.15) * mm, "end": v(4.46, 28.3) * mm});
            skLineSegment(sketch, "E968", {"start": v(4.46, 28.3) * mm, "end": v(4.44, 28.44) * mm});
            skLineSegment(sketch, "E969", {"start": v(4.44, 28.44) * mm, "end": v(4.42, 28.6) * mm});
            skLineSegment(sketch, "E970", {"start": v(4.42, 28.6) * mm, "end": v(4.4, 28.78) * mm});
            skLineSegment(sketch, "E971", {"start": v(4.4, 28.78) * mm, "end": v(4.37, 28.97) * mm});
            skLineSegment(sketch, "E972", {"start": v(4.37, 28.97) * mm, "end": v(4.33, 29.16) * mm});
            skLineSegment(sketch, "E973", {"start": v(4.33, 29.16) * mm, "end": v(4.29, 29.37) * mm});
            skLineSegment(sketch, "E974", {"start": v(4.29, 29.37) * mm, "end": v(4.24, 29.59) * mm});
            skLineSegment(sketch, "E975", {"start": v(4.24, 29.59) * mm, "end": v(4.18, 29.82) * mm});
            skLineSegment(sketch, "E976", {"start": v(4.18, 29.82) * mm, "end": v(4.12, 30.06) * mm});
            skLineSegment(sketch, "E977", {"start": v(4.12, 30.06) * mm, "end": v(4.06, 30.25) * mm});
            skLineSegment(sketch, "E978", {"start": v(4.06, 30.25) * mm, "end": v(3.2, 30.4) * mm});
            skLineSegment(sketch, "E979", {"start": v(3.2, 30.4) * mm, "end": v(2.32, 30.44) * mm});
            skLineSegment(sketch, "E980", {"start": v(2.32, 30.44) * mm, "end": v(2.22, 30.26) * mm});
            skLineSegment(sketch, "E981", {"start": v(2.22, 30.26) * mm, "end": v(2.11, 30.04) * mm});
            skLineSegment(sketch, "E982", {"start": v(2.11, 30.04) * mm, "end": v(2, 29.82) * mm});
            skLineSegment(sketch, "E983", {"start": v(2, 29.82) * mm, "end": v(1.91, 29.62) * mm});
            skLineSegment(sketch, "E984", {"start": v(1.91, 29.62) * mm, "end": v(1.83, 29.43) * mm});
            skLineSegment(sketch, "E985", {"start": v(1.83, 29.43) * mm, "end": v(1.75, 29.24) * mm});
            skLineSegment(sketch, "E986", {"start": v(1.75, 29.24) * mm, "end": v(1.68, 29.07) * mm});
            skLineSegment(sketch, "E987", {"start": v(1.68, 29.07) * mm, "end": v(1.62, 28.9) * mm});
            skLineSegment(sketch, "E988", {"start": v(1.62, 28.9) * mm, "end": v(1.57, 28.75) * mm});
            skLineSegment(sketch, "E989", {"start": v(1.57, 28.75) * mm, "end": v(1.52, 28.6) * mm});
            skLineSegment(sketch, "E990", {"start": v(1.52, 28.6) * mm, "end": v(1.48, 28.47) * mm});
            skLineSegment(sketch, "E991", {"start": v(1.48, 28.47) * mm, "end": v(1.45, 28.35) * mm});
            skLineSegment(sketch, "E992", {"start": v(1.45, 28.35) * mm, "end": v(1.42, 28.23) * mm});
            skLineSegment(sketch, "E993", {"start": v(1.42, 28.23) * mm, "end": v(1.4, 28.13) * mm});
            skLineSegment(sketch, "E994", {"start": v(1.4, 28.13) * mm, "end": v(1.38, 28.05) * mm});
            skLineSegment(sketch, "E995", {"start": v(1.38, 28.05) * mm, "end": v(1.37, 27.97) * mm});
            skLineSegment(sketch, "E996", {"start": v(1.37, 27.97) * mm, "end": v(1.36, 27.9) * mm});
            skLineSegment(sketch, "E997", {"start": v(1.36, 27.9) * mm, "end": v(1.35, 27.85) * mm});
            skLineSegment(sketch, "E998", {"start": v(1.35, 27.85) * mm, "end": v(1.34, 27.8) * mm});
            skLineSegment(sketch, "E999", {"start": v(1.34, 27.8) * mm, "end": v(1.34, 27.78) * mm});
            skLineSegment(sketch, "E1000", {"start": v(1.34, 27.78) * mm, "end": v(1.34, 27.76) * mm});
            skLineSegment(sketch, "E1001", {"start": v(1.34, 27.76) * mm, "end": v(1.34, 27.76) * mm});
            skLineSegment(sketch, "E1002", {"start": v(1.34, 27.76) * mm, "end": v(1.34, 27.67) * mm});
            skLineSegment(sketch, "E1003", {"start": v(1.34, 27.67) * mm, "end": v(1.33, 27.52) * mm});
            skLineSegment(sketch, "E1004", {"start": v(1.33, 27.52) * mm, "end": v(1.32, 27.37) * mm});
            skLineSegment(sketch, "E1005", {"start": v(1.32, 27.37) * mm, "end": v(1.3, 27.24) * mm});
            skLineSegment(sketch, "E1006", {"start": v(1.3, 27.24) * mm, "end": v(1.28, 27.12) * mm});
            skLineSegment(sketch, "E1007", {"start": v(1.28, 27.12) * mm, "end": v(1.25, 27) * mm});
            skLineSegment(sketch, "E1008", {"start": v(1.25, 27) * mm, "end": v(1.22, 26.91) * mm});
            skLineSegment(sketch, "E1009", {"start": v(1.22, 26.91) * mm, "end": v(1.18, 26.83) * mm});
            skLineSegment(sketch, "E1010", {"start": v(1.18, 26.83) * mm, "end": v(1.14, 26.76) * mm});
            skLineSegment(sketch, "E1011", {"start": v(1.14, 26.76) * mm, "end": v(1.1, 26.7) * mm});
            skLineSegment(sketch, "E1012", {"start": v(1.1, 26.7) * mm, "end": v(1.06, 26.67) * mm});
            skLineSegment(sketch, "E1013", {"start": v(1.06, 26.67) * mm, "end": v(1.02, 26.64) * mm});
            skLineSegment(sketch, "E1014", {"start": v(1.02, 26.64) * mm, "end": v(0.98, 26.62) * mm});
            skLineSegment(sketch, "E1015", {"start": v(0.98, 26.62) * mm, "end": v(0.94, 26.62) * mm});
            skLineSegment(sketch, "E1016", {"start": v(0.94, 26.62) * mm, "end": v(0.84, 26.63) * mm});
            skLineSegment(sketch, "E1017", {"start": v(0.84, 26.63) * mm, "end": v(0.28, 26.64) * mm});
            skLineSegment(sketch, "E1018", {"start": v(0.28, 26.64) * mm, "end": v(-0.28, 26.64) * mm});
            skLineSegment(sketch, "E1019", {"start": v(-0.28, 26.64) * mm, "end": v(-0.84, 26.63) * mm});
            skLineSegment(sketch, "E1020", {"start": v(-0.84, 26.63) * mm, "end": v(-0.94, 26.62) * mm});
            skLineSegment(sketch, "E1021", {"start": v(-0.94, 26.62) * mm, "end": v(-0.98, 26.62) * mm});
            skLineSegment(sketch, "E1022", {"start": v(-0.98, 26.62) * mm, "end": v(-1.02, 26.64) * mm});
            skLineSegment(sketch, "E1023", {"start": v(-1.02, 26.64) * mm, "end": v(-1.06, 26.67) * mm});
            skLineSegment(sketch, "E1024", {"start": v(-1.06, 26.67) * mm, "end": v(-1.1, 26.7) * mm});
            skLineSegment(sketch, "E1025", {"start": v(-1.1, 26.7) * mm, "end": v(-1.14, 26.76) * mm});
            skLineSegment(sketch, "E1026", {"start": v(-1.14, 26.76) * mm, "end": v(-1.18, 26.83) * mm});
            skLineSegment(sketch, "E1027", {"start": v(-1.18, 26.83) * mm, "end": v(-1.22, 26.91) * mm});
            skLineSegment(sketch, "E1028", {"start": v(-1.22, 26.91) * mm, "end": v(-1.25, 27) * mm});
            skLineSegment(sketch, "E1029", {"start": v(-1.25, 27) * mm, "end": v(-1.28, 27.12) * mm});
            skLineSegment(sketch, "E1030", {"start": v(-1.28, 27.12) * mm, "end": v(-1.3, 27.24) * mm});
            skLineSegment(sketch, "E1031", {"start": v(-1.3, 27.24) * mm, "end": v(-1.32, 27.37) * mm});
            skLineSegment(sketch, "E1032", {"start": v(-1.32, 27.37) * mm, "end": v(-1.33, 27.52) * mm});
            skLineSegment(sketch, "E1033", {"start": v(-1.33, 27.52) * mm, "end": v(-1.34, 27.67) * mm});
            skLineSegment(sketch, "E1034", {"start": v(-1.34, 27.67) * mm, "end": v(-1.34, 27.76) * mm});
            skLineSegment(sketch, "E1035", {"start": v(-1.34, 27.76) * mm, "end": v(-1.34, 27.76) * mm});
            skLineSegment(sketch, "E1036", {"start": v(-1.34, 27.76) * mm, "end": v(-1.34, 27.78) * mm});
            skLineSegment(sketch, "E1037", {"start": v(-1.34, 27.78) * mm, "end": v(-1.34, 27.8) * mm});
            skLineSegment(sketch, "E1038", {"start": v(-1.34, 27.8) * mm, "end": v(-1.35, 27.85) * mm});
            skLineSegment(sketch, "E1039", {"start": v(-1.35, 27.85) * mm, "end": v(-1.36, 27.9) * mm});
            skLineSegment(sketch, "E1040", {"start": v(-1.36, 27.9) * mm, "end": v(-1.37, 27.97) * mm});
            skLineSegment(sketch, "E1041", {"start": v(-1.37, 27.97) * mm, "end": v(-1.38, 28.05) * mm});
            skLineSegment(sketch, "E1042", {"start": v(-1.38, 28.05) * mm, "end": v(-1.4, 28.13) * mm});
            skLineSegment(sketch, "E1043", {"start": v(-1.4, 28.13) * mm, "end": v(-1.42, 28.23) * mm});
            skLineSegment(sketch, "E1044", {"start": v(-1.42, 28.23) * mm, "end": v(-1.45, 28.35) * mm});
            skLineSegment(sketch, "E1045", {"start": v(-1.45, 28.35) * mm, "end": v(-1.48, 28.47) * mm});
            skLineSegment(sketch, "E1046", {"start": v(-1.48, 28.47) * mm, "end": v(-1.52, 28.6) * mm});
            skLineSegment(sketch, "E1047", {"start": v(-1.52, 28.6) * mm, "end": v(-1.57, 28.75) * mm});
            skLineSegment(sketch, "E1048", {"start": v(-1.57, 28.75) * mm, "end": v(-1.62, 28.9) * mm});
            skLineSegment(sketch, "E1049", {"start": v(-1.62, 28.9) * mm, "end": v(-1.68, 29.07) * mm});
            skLineSegment(sketch, "E1050", {"start": v(-1.68, 29.07) * mm, "end": v(-1.75, 29.24) * mm});
            skLineSegment(sketch, "E1051", {"start": v(-1.75, 29.24) * mm, "end": v(-1.83, 29.43) * mm});
            skLineSegment(sketch, "E1052", {"start": v(-1.83, 29.43) * mm, "end": v(-1.91, 29.62) * mm});
            skLineSegment(sketch, "E1053", {"start": v(-1.91, 29.62) * mm, "end": v(-2, 29.82) * mm});
            skLineSegment(sketch, "E1054", {"start": v(-2, 29.82) * mm, "end": v(-2.11, 30.04) * mm});
            skLineSegment(sketch, "E1055", {"start": v(-2.11, 30.04) * mm, "end": v(-2.22, 30.26) * mm});
            skLineSegment(sketch, "E1056", {"start": v(-2.22, 30.26) * mm, "end": v(-2.32, 30.44) * mm});
            skLineSegment(sketch, "E1057", {"start": v(-2.32, 30.44) * mm, "end": v(-3.2, 30.4) * mm});
            skLineSegment(sketch, "E1058", {"start": v(-3.2, 30.4) * mm, "end": v(-4.06, 30.25) * mm});
            skLineSegment(sketch, "E1059", {"start": v(-4.06, 30.25) * mm, "end": v(-4.12, 30.06) * mm});
            skLineSegment(sketch, "E1060", {"start": v(-4.12, 30.06) * mm, "end": v(-4.18, 29.82) * mm});
            skLineSegment(sketch, "E1061", {"start": v(-4.18, 29.82) * mm, "end": v(-4.24, 29.59) * mm});
            skLineSegment(sketch, "E1062", {"start": v(-4.24, 29.59) * mm, "end": v(-4.29, 29.37) * mm});
            skLineSegment(sketch, "E1063", {"start": v(-4.29, 29.37) * mm, "end": v(-4.33, 29.16) * mm});
            skLineSegment(sketch, "E1064", {"start": v(-4.33, 29.16) * mm, "end": v(-4.37, 28.97) * mm});
            skLineSegment(sketch, "E1065", {"start": v(-4.37, 28.97) * mm, "end": v(-4.4, 28.78) * mm});
            skLineSegment(sketch, "E1066", {"start": v(-4.4, 28.78) * mm, "end": v(-4.42, 28.6) * mm});
            skLineSegment(sketch, "E1067", {"start": v(-4.42, 28.6) * mm, "end": v(-4.44, 28.44) * mm});
            skLineSegment(sketch, "E1068", {"start": v(-4.44, 28.44) * mm, "end": v(-4.46, 28.3) * mm});
            skLineSegment(sketch, "E1069", {"start": v(-4.46, 28.3) * mm, "end": v(-4.47, 28.15) * mm});
            skLineSegment(sketch, "E1070", {"start": v(-4.47, 28.15) * mm, "end": v(-4.47, 28.03) * mm});
            skLineSegment(sketch, "E1071", {"start": v(-4.47, 28.03) * mm, "end": v(-4.48, 27.91) * mm});
            skLineSegment(sketch, "E1072", {"start": v(-4.48, 27.91) * mm, "end": v(-4.48, 27.81) * mm});
            skLineSegment(sketch, "E1073", {"start": v(-4.48, 27.81) * mm, "end": v(-4.48, 27.72) * mm});
            skLineSegment(sketch, "E1074", {"start": v(-4.48, 27.72) * mm, "end": v(-4.48, 27.64) * mm});
            skLineSegment(sketch, "E1075", {"start": v(-4.48, 27.64) * mm, "end": v(-4.47, 27.58) * mm});
            skLineSegment(sketch, "E1076", {"start": v(-4.47, 27.58) * mm, "end": v(-4.47, 27.52) * mm});
            skLineSegment(sketch, "E1077", {"start": v(-4.47, 27.52) * mm, "end": v(-4.47, 27.48) * mm});
            skLineSegment(sketch, "E1078", {"start": v(-4.47, 27.48) * mm, "end": v(-4.46, 27.45) * mm});
            skLineSegment(sketch, "E1079", {"start": v(-4.46, 27.45) * mm, "end": v(-4.46, 27.44) * mm});
            skLineSegment(sketch, "E1080", {"start": v(-4.46, 27.44) * mm, "end": v(-4.46, 27.43) * mm});
            skLineSegment(sketch, "E1081", {"start": v(-4.46, 27.43) * mm, "end": v(-4.44, 27.35) * mm});
            skLineSegment(sketch, "E1082", {"start": v(-4.44, 27.35) * mm, "end": v(-4.42, 27.2) * mm});
            skLineSegment(sketch, "E1083", {"start": v(-4.42, 27.2) * mm, "end": v(-4.4, 27.05) * mm});
            skLineSegment(sketch, "E1084", {"start": v(-4.4, 27.05) * mm, "end": v(-4.4, 26.91) * mm});
            skLineSegment(sketch, "E1085", {"start": v(-4.4, 26.91) * mm, "end": v(-4.4, 26.79) * mm});
            skLineSegment(sketch, "E1086", {"start": v(-4.4, 26.79) * mm, "end": v(-4.4, 26.68) * mm});
            skLineSegment(sketch, "E1087", {"start": v(-4.4, 26.68) * mm, "end": v(-4.4, 26.58) * mm});
            skLineSegment(sketch, "E1088", {"start": v(-4.4, 26.58) * mm, "end": v(-4.42, 26.5) * mm});
            skLineSegment(sketch, "E1089", {"start": v(-4.42, 26.5) * mm, "end": v(-4.44, 26.42) * mm});
            skLineSegment(sketch, "E1090", {"start": v(-4.44, 26.42) * mm, "end": v(-4.47, 26.35) * mm});
            skLineSegment(sketch, "E1091", {"start": v(-4.47, 26.35) * mm, "end": v(-4.5, 26.3) * mm});
            skLineSegment(sketch, "E1092", {"start": v(-4.5, 26.3) * mm, "end": v(-4.54, 26.27) * mm});
            skLineSegment(sketch, "E1093", {"start": v(-4.54, 26.27) * mm, "end": v(-4.58, 26.25) * mm});
            skLineSegment(sketch, "E1094", {"start": v(-4.58, 26.25) * mm, "end": v(-4.62, 26.24) * mm});
            skLineSegment(sketch, "E1095", {"start": v(-4.62, 26.24) * mm, "end": v(-4.72, 26.22) * mm});
            skLineSegment(sketch, "E1096", {"start": v(-4.72, 26.22) * mm, "end": v(-5.27, 26.11) * mm});
            skLineSegment(sketch, "E1097", {"start": v(-5.27, 26.11) * mm, "end": v(-5.81, 26) * mm});
            skLineSegment(sketch, "E1098", {"start": v(-5.81, 26) * mm, "end": v(-6.35, 25.87) * mm});
            skLineSegment(sketch, "E1099", {"start": v(-6.35, 25.87) * mm, "end": v(-6.45, 25.85) * mm});
            skLineSegment(sketch, "E1100", {"start": v(-6.45, 25.85) * mm, "end": v(-6.5, 25.84) * mm});
            skLineSegment(sketch, "E1101", {"start": v(-6.5, 25.84) * mm, "end": v(-6.54, 25.84) * mm});
            skLineSegment(sketch, "E1102", {"start": v(-6.54, 25.84) * mm, "end": v(-6.59, 25.86) * mm});
            skLineSegment(sketch, "E1103", {"start": v(-6.59, 25.86) * mm, "end": v(-6.63, 25.9) * mm});
            skLineSegment(sketch, "E1104", {"start": v(-6.63, 25.9) * mm, "end": v(-6.68, 25.94) * mm});
            skLineSegment(sketch, "E1105", {"start": v(-6.68, 25.94) * mm, "end": v(-6.73, 26) * mm});
            skLineSegment(sketch, "E1106", {"start": v(-6.73, 26) * mm, "end": v(-6.78, 26.07) * mm});
            skLineSegment(sketch, "E1107", {"start": v(-6.78, 26.07) * mm, "end": v(-6.84, 26.16) * mm});
            skLineSegment(sketch, "E1108", {"start": v(-6.84, 26.16) * mm, "end": v(-6.88, 26.26) * mm});
            skLineSegment(sketch, "E1109", {"start": v(-6.88, 26.26) * mm, "end": v(-6.93, 26.37) * mm});
            skLineSegment(sketch, "E1110", {"start": v(-6.93, 26.37) * mm, "end": v(-6.98, 26.5) * mm});
            skLineSegment(sketch, "E1111", {"start": v(-6.98, 26.5) * mm, "end": v(-7.02, 26.64) * mm});
            skLineSegment(sketch, "E1112", {"start": v(-7.02, 26.64) * mm, "end": v(-7.06, 26.8) * mm});
            skLineSegment(sketch, "E1113", {"start": v(-7.06, 26.8) * mm, "end": v(-7.08, 26.88) * mm});
            skLineSegment(sketch, "E1114", {"start": v(-7.08, 26.88) * mm, "end": v(-7.08, 26.88) * mm});
            skLineSegment(sketch, "E1115", {"start": v(-7.08, 26.88) * mm, "end": v(-7.09, 26.9) * mm});
            skLineSegment(sketch, "E1116", {"start": v(-7.09, 26.9) * mm, "end": v(-7.1, 26.92) * mm});
            skLineSegment(sketch, "E1117", {"start": v(-7.1, 26.92) * mm, "end": v(-7.11, 26.96) * mm});
            skLineSegment(sketch, "E1118", {"start": v(-7.11, 26.96) * mm, "end": v(-7.13, 27.01) * mm});
            skLineSegment(sketch, "E1119", {"start": v(-7.13, 27.01) * mm, "end": v(-7.15, 27.07) * mm});
            skLineSegment(sketch, "E1120", {"start": v(-7.15, 27.07) * mm, "end": v(-7.18, 27.15) * mm});
            skLineSegment(sketch, "E1121", {"start": v(-7.18, 27.15) * mm, "end": v(-7.22, 27.23) * mm});
            skLineSegment(sketch, "E1122", {"start": v(-7.22, 27.23) * mm, "end": v(-7.26, 27.32) * mm});
            skLineSegment(sketch, "E1123", {"start": v(-7.26, 27.32) * mm, "end": v(-7.31, 27.43) * mm});
            skLineSegment(sketch, "E1124", {"start": v(-7.31, 27.43) * mm, "end": v(-7.37, 27.54) * mm});
            skLineSegment(sketch, "E1125", {"start": v(-7.37, 27.54) * mm, "end": v(-7.44, 27.66) * mm});
            skLineSegment(sketch, "E1126", {"start": v(-7.44, 27.66) * mm, "end": v(-7.51, 27.8) * mm});
            skLineSegment(sketch, "E1127", {"start": v(-7.51, 27.8) * mm, "end": v(-7.6, 27.93) * mm});
            skLineSegment(sketch, "E1128", {"start": v(-7.6, 27.93) * mm, "end": v(-7.69, 28.08) * mm});
            skLineSegment(sketch, "E1129", {"start": v(-7.69, 28.08) * mm, "end": v(-7.8, 28.24) * mm});
            skLineSegment(sketch, "E1130", {"start": v(-7.8, 28.24) * mm, "end": v(-7.9, 28.4) * mm});
            skLineSegment(sketch, "E1131", {"start": v(-7.9, 28.4) * mm, "end": v(-8.03, 28.58) * mm});
            skLineSegment(sketch, "E1132", {"start": v(-8.03, 28.58) * mm, "end": v(-8.16, 28.76) * mm});
            skLineSegment(sketch, "E1133", {"start": v(-8.16, 28.76) * mm, "end": v(-8.3, 28.94) * mm});
            skLineSegment(sketch, "E1134", {"start": v(-8.3, 28.94) * mm, "end": v(-8.47, 29.13) * mm});
            skLineSegment(sketch, "E1135", {"start": v(-8.47, 29.13) * mm, "end": v(-8.6, 29.29) * mm});
            skLineSegment(sketch, "E1136", {"start": v(-8.6, 29.29) * mm, "end": v(-9.44, 29.06) * mm});
            skLineSegment(sketch, "E1137", {"start": v(-9.44, 29.06) * mm, "end": v(-10.26, 28.75) * mm});
            skLineSegment(sketch, "E1138", {"start": v(-10.26, 28.75) * mm, "end": v(-10.28, 28.55) * mm});
            skLineSegment(sketch, "E1139", {"start": v(-10.28, 28.55) * mm, "end": v(-10.29, 28.3) * mm});
            skLineSegment(sketch, "E1140", {"start": v(-10.29, 28.3) * mm, "end": v(-10.3, 28.06) * mm});
            skLineSegment(sketch, "E1141", {"start": v(-10.3, 28.06) * mm, "end": v(-10.3, 27.84) * mm});
            skLineSegment(sketch, "E1142", {"start": v(-10.3, 27.84) * mm, "end": v(-10.3, 27.62) * mm});
            skLineSegment(sketch, "E1143", {"start": v(-10.3, 27.62) * mm, "end": v(-10.3, 27.42) * mm});
            skLineSegment(sketch, "E1144", {"start": v(-10.3, 27.42) * mm, "end": v(-10.29, 27.24) * mm});
            skLineSegment(sketch, "E1145", {"start": v(-10.29, 27.24) * mm, "end": v(-10.27, 27.06) * mm});
            skLineSegment(sketch, "E1146", {"start": v(-10.27, 27.06) * mm, "end": v(-10.26, 26.9) * mm});
            skLineSegment(sketch, "E1147", {"start": v(-10.26, 26.9) * mm, "end": v(-10.24, 26.75) * mm});
            skLineSegment(sketch, "E1148", {"start": v(-10.24, 26.75) * mm, "end": v(-10.22, 26.61) * mm});
            skLineSegment(sketch, "E1149", {"start": v(-10.22, 26.61) * mm, "end": v(-10.2, 26.49) * mm});
            skLineSegment(sketch, "E1150", {"start": v(-10.2, 26.49) * mm, "end": v(-10.18, 26.37) * mm});
            skLineSegment(sketch, "E1151", {"start": v(-10.18, 26.37) * mm, "end": v(-10.16, 26.27) * mm});
            skLineSegment(sketch, "E1152", {"start": v(-10.16, 26.27) * mm, "end": v(-10.15, 26.18) * mm});
            skLineSegment(sketch, "E1153", {"start": v(-10.15, 26.18) * mm, "end": v(-10.13, 26.1) * mm});
            skLineSegment(sketch, "E1154", {"start": v(-10.13, 26.1) * mm, "end": v(-10.11, 26.04) * mm});
            skLineSegment(sketch, "E1155", {"start": v(-10.11, 26.04) * mm, "end": v(-10.1, 26) * mm});
            skLineSegment(sketch, "E1156", {"start": v(-10.1, 26) * mm, "end": v(-10.08, 25.95) * mm});
            skLineSegment(sketch, "E1157", {"start": v(-10.08, 25.95) * mm, "end": v(-10.07, 25.92) * mm});
            skLineSegment(sketch, "E1158", {"start": v(-10.07, 25.92) * mm, "end": v(-10.07, 25.9) * mm});
            skLineSegment(sketch, "E1159", {"start": v(-10.07, 25.9) * mm, "end": v(-10.07, 25.9) * mm});
            skLineSegment(sketch, "E1160", {"start": v(-10.07, 25.9) * mm, "end": v(-10.03, 25.83) * mm});
            skLineSegment(sketch, "E1161", {"start": v(-10.03, 25.83) * mm, "end": v(-9.98, 25.68) * mm});
            skLineSegment(sketch, "E1162", {"start": v(-9.98, 25.68) * mm, "end": v(-9.93, 25.54) * mm});
            skLineSegment(sketch, "E1163", {"start": v(-9.93, 25.54) * mm, "end": v(-9.9, 25.4) * mm});
            skLineSegment(sketch, "E1164", {"start": v(-9.9, 25.4) * mm, "end": v(-9.86, 25.29) * mm});
            skLineSegment(sketch, "E1165", {"start": v(-9.86, 25.29) * mm, "end": v(-9.85, 25.18) * mm});
            skLineSegment(sketch, "E1166", {"start": v(-9.85, 25.18) * mm, "end": v(-9.84, 25.08) * mm});
            skLineSegment(sketch, "E1167", {"start": v(-9.84, 25.08) * mm, "end": v(-9.83, 25) * mm});
            skLineSegment(sketch, "E1168", {"start": v(-9.83, 25) * mm, "end": v(-9.84, 24.91) * mm});
            skLineSegment(sketch, "E1169", {"start": v(-9.84, 24.91) * mm, "end": v(-9.85, 24.85) * mm});
            skLineSegment(sketch, "E1170", {"start": v(-9.85, 24.85) * mm, "end": v(-9.87, 24.8) * mm});
            skLineSegment(sketch, "E1171", {"start": v(-9.87, 24.8) * mm, "end": v(-9.9, 24.75) * mm});
            skLineSegment(sketch, "E1172", {"start": v(-9.9, 24.75) * mm, "end": v(-9.93, 24.72) * mm});
            skLineSegment(sketch, "E1173", {"start": v(-9.93, 24.72) * mm, "end": v(-9.97, 24.7) * mm});
            skLineSegment(sketch, "E1174", {"start": v(-9.97, 24.7) * mm, "end": v(-10.07, 24.66) * mm});
            skLineSegment(sketch, "E1175", {"start": v(-10.07, 24.66) * mm, "end": v(-10.58, 24.45) * mm});
            skLineSegment(sketch, "E1176", {"start": v(-10.58, 24.45) * mm, "end": v(-11.09, 24.22) * mm});
            skLineSegment(sketch, "E1177", {"start": v(-11.09, 24.22) * mm, "end": v(-11.6, 23.98) * mm});
            skLineSegment(sketch, "E1178", {"start": v(-11.6, 23.98) * mm, "end": v(-11.69, 23.94) * mm});
            skLineSegment(sketch, "E1179", {"start": v(-11.69, 23.94) * mm, "end": v(-11.72, 23.92) * mm});
            skLineSegment(sketch, "E1180", {"start": v(-11.72, 23.92) * mm, "end": v(-11.77, 23.92) * mm});
            skLineSegment(sketch, "E1181", {"start": v(-11.77, 23.92) * mm, "end": v(-11.82, 23.93) * mm});
            skLineSegment(sketch, "E1182", {"start": v(-11.82, 23.93) * mm, "end": v(-11.87, 23.95) * mm});
            skLineSegment(sketch, "E1183", {"start": v(-11.87, 23.95) * mm, "end": v(-11.93, 23.98) * mm});
            skLineSegment(sketch, "E1184", {"start": v(-11.93, 23.98) * mm, "end": v(-12, 24.03) * mm});
            skLineSegment(sketch, "E1185", {"start": v(-12, 24.03) * mm, "end": v(-12.06, 24.1) * mm});
            skLineSegment(sketch, "E1186", {"start": v(-12.06, 24.1) * mm, "end": v(-12.12, 24.17) * mm});
            skLineSegment(sketch, "E1187", {"start": v(-12.12, 24.17) * mm, "end": v(-12.2, 24.25) * mm});
            skLineSegment(sketch, "E1188", {"start": v(-12.2, 24.25) * mm, "end": v(-12.26, 24.35) * mm});
            skLineSegment(sketch, "E1189", {"start": v(-12.26, 24.35) * mm, "end": v(-12.34, 24.47) * mm});
            skLineSegment(sketch, "E1190", {"start": v(-12.34, 24.47) * mm, "end": v(-12.4, 24.6) * mm});
            skLineSegment(sketch, "E1191", {"start": v(-12.4, 24.6) * mm, "end": v(-12.48, 24.74) * mm});
            skLineSegment(sketch, "E1192", {"start": v(-12.48, 24.74) * mm, "end": v(-12.52, 24.82) * mm});
            skLineSegment(sketch, "E1193", {"start": v(-12.52, 24.82) * mm, "end": v(-12.52, 24.82) * mm});
            skLineSegment(sketch, "E1194", {"start": v(-12.52, 24.82) * mm, "end": v(-12.52, 24.83) * mm});
            skLineSegment(sketch, "E1195", {"start": v(-12.52, 24.83) * mm, "end": v(-12.54, 24.86) * mm});
            skLineSegment(sketch, "E1196", {"start": v(-12.54, 24.86) * mm, "end": v(-12.56, 24.9) * mm});
            skLineSegment(sketch, "E1197", {"start": v(-12.56, 24.9) * mm, "end": v(-12.59, 24.94) * mm});
            skLineSegment(sketch, "E1198", {"start": v(-12.59, 24.94) * mm, "end": v(-12.63, 25) * mm});
            skLineSegment(sketch, "E1199", {"start": v(-12.63, 25) * mm, "end": v(-12.67, 25.06) * mm});
            skLineSegment(sketch, "E1200", {"start": v(-12.67, 25.06) * mm, "end": v(-12.72, 25.13) * mm});
            skLineSegment(sketch, "E1201", {"start": v(-12.72, 25.13) * mm, "end": v(-12.78, 25.22) * mm});
            skLineSegment(sketch, "E1202", {"start": v(-12.78, 25.22) * mm, "end": v(-12.85, 25.3) * mm});
            skLineSegment(sketch, "E1203", {"start": v(-12.85, 25.3) * mm, "end": v(-12.93, 25.4) * mm});
            skLineSegment(sketch, "E1204", {"start": v(-12.93, 25.4) * mm, "end": v(-13.02, 25.5) * mm});
            skLineSegment(sketch, "E1205", {"start": v(-13.02, 25.5) * mm, "end": v(-13.13, 25.62) * mm});
            skLineSegment(sketch, "E1206", {"start": v(-13.13, 25.62) * mm, "end": v(-13.24, 25.74) * mm});
            skLineSegment(sketch, "E1207", {"start": v(-13.24, 25.74) * mm, "end": v(-13.36, 25.87) * mm});
            skLineSegment(sketch, "E1208", {"start": v(-13.36, 25.87) * mm, "end": v(-13.5, 26) * mm});
            skLineSegment(sketch, "E1209", {"start": v(-13.5, 26) * mm, "end": v(-13.64, 26.14) * mm});
            skLineSegment(sketch, "E1210", {"start": v(-13.64, 26.14) * mm, "end": v(-13.8, 26.28) * mm});
            skLineSegment(sketch, "E1211", {"start": v(-13.8, 26.28) * mm, "end": v(-13.96, 26.43) * mm});
            skLineSegment(sketch, "E1212", {"start": v(-13.96, 26.43) * mm, "end": v(-14.14, 26.58) * mm});
            skLineSegment(sketch, "E1213", {"start": v(-14.14, 26.58) * mm, "end": v(-14.34, 26.74) * mm});
            skLineSegment(sketch, "E1214", {"start": v(-14.34, 26.74) * mm, "end": v(-14.5, 26.86) * mm});
            skLineSegment(sketch, "E1215", {"start": v(-14.5, 26.86) * mm, "end": v(-15.28, 26.46) * mm});
            skLineSegment(sketch, "E1216", {"start": v(-15.28, 26.46) * mm, "end": v(-16.01, 25.99) * mm});
            skLineSegment(sketch, "E1217", {"start": v(-16.01, 25.99) * mm, "end": v(-15.99, 25.79) * mm});
            skLineSegment(sketch, "E1218", {"start": v(-15.99, 25.79) * mm, "end": v(-15.95, 25.54) * mm});
            skLineSegment(sketch, "E1219", {"start": v(-15.95, 25.54) * mm, "end": v(-15.9, 25.3) * mm});
            skLineSegment(sketch, "E1220", {"start": v(-15.9, 25.3) * mm, "end": v(-15.86, 25.09) * mm});
            skLineSegment(sketch, "E1221", {"start": v(-15.86, 25.09) * mm, "end": v(-15.82, 24.88) * mm});
            skLineSegment(sketch, "E1222", {"start": v(-15.82, 24.88) * mm, "end": v(-15.77, 24.69) * mm});
            skLineSegment(sketch, "E1223", {"start": v(-15.77, 24.69) * mm, "end": v(-15.72, 24.5) * mm});
            skLineSegment(sketch, "E1224", {"start": v(-15.72, 24.5) * mm, "end": v(-15.68, 24.33) * mm});
            skLineSegment(sketch, "E1225", {"start": v(-15.68, 24.33) * mm, "end": v(-15.63, 24.18) * mm});
            skLineSegment(sketch, "E1226", {"start": v(-15.63, 24.18) * mm, "end": v(-15.58, 24.03) * mm});
            skLineSegment(sketch, "E1227", {"start": v(-15.58, 24.03) * mm, "end": v(-15.53, 23.9) * mm});
            skLineSegment(sketch, "E1228", {"start": v(-15.53, 23.9) * mm, "end": v(-15.49, 23.78) * mm});
            skLineSegment(sketch, "E1229", {"start": v(-15.49, 23.78) * mm, "end": v(-15.45, 23.68) * mm});
            skLineSegment(sketch, "E1230", {"start": v(-15.45, 23.68) * mm, "end": v(-15.4, 23.58) * mm});
            skLineSegment(sketch, "E1231", {"start": v(-15.4, 23.58) * mm, "end": v(-15.37, 23.5) * mm});
            skLineSegment(sketch, "E1232", {"start": v(-15.37, 23.5) * mm, "end": v(-15.33, 23.43) * mm});
            skLineSegment(sketch, "E1233", {"start": v(-15.33, 23.43) * mm, "end": v(-15.3, 23.37) * mm});
            skLineSegment(sketch, "E1234", {"start": v(-15.3, 23.37) * mm, "end": v(-15.28, 23.32) * mm});
            skLineSegment(sketch, "E1235", {"start": v(-15.28, 23.32) * mm, "end": v(-15.26, 23.29) * mm});
            skLineSegment(sketch, "E1236", {"start": v(-15.26, 23.29) * mm, "end": v(-15.24, 23.26) * mm});
            skLineSegment(sketch, "E1237", {"start": v(-15.24, 23.26) * mm, "end": v(-15.23, 23.25) * mm});
            skLineSegment(sketch, "E1238", {"start": v(-15.23, 23.25) * mm, "end": v(-15.23, 23.25) * mm});
            skLineSegment(sketch, "E1239", {"start": v(-15.23, 23.25) * mm, "end": v(-15.18, 23.18) * mm});
            skLineSegment(sketch, "E1240", {"start": v(-15.18, 23.18) * mm, "end": v(-15.1, 23.04) * mm});
            skLineSegment(sketch, "E1241", {"start": v(-15.1, 23.04) * mm, "end": v(-15.02, 22.92) * mm});
            skLineSegment(sketch, "E1242", {"start": v(-15.02, 22.92) * mm, "end": v(-14.96, 22.8) * mm});
            skLineSegment(sketch, "E1243", {"start": v(-14.96, 22.8) * mm, "end": v(-14.9, 22.69) * mm});
            skLineSegment(sketch, "E1244", {"start": v(-14.9, 22.69) * mm, "end": v(-14.87, 22.58) * mm});
            skLineSegment(sketch, "E1245", {"start": v(-14.87, 22.58) * mm, "end": v(-14.83, 22.49) * mm});
            skLineSegment(sketch, "E1246", {"start": v(-14.83, 22.49) * mm, "end": v(-14.81, 22.4) * mm});
            skLineSegment(sketch, "E1247", {"start": v(-14.81, 22.4) * mm, "end": v(-14.8, 22.32) * mm});
            skLineSegment(sketch, "E1248", {"start": v(-14.8, 22.32) * mm, "end": v(-14.8, 22.26) * mm});
            skLineSegment(sketch, "E1249", {"start": v(-14.8, 22.26) * mm, "end": v(-14.81, 22.2) * mm});
            skLineSegment(sketch, "E1250", {"start": v(-14.81, 22.2) * mm, "end": v(-14.83, 22.15) * mm});
            skLineSegment(sketch, "E1251", {"start": v(-14.83, 22.15) * mm, "end": v(-14.86, 22.11) * mm});
            skLineSegment(sketch, "E1252", {"start": v(-14.86, 22.11) * mm, "end": v(-14.89, 22.09) * mm});
            skLineSegment(sketch, "E1253", {"start": v(-14.89, 22.09) * mm, "end": v(-14.97, 22.03) * mm});
            skLineSegment(sketch, "E1254", {"start": v(-14.97, 22.03) * mm, "end": v(-15.43, 21.71) * mm});
            skLineSegment(sketch, "E1255", {"start": v(-15.43, 21.71) * mm, "end": v(-15.88, 21.39) * mm});
            skLineSegment(sketch, "E1256", {"start": v(-15.88, 21.39) * mm, "end": v(-16.33, 21.05) * mm});
            skLineSegment(sketch, "E1257", {"start": v(-16.33, 21.05) * mm, "end": v(-16.4, 20.99) * mm});
            skLineSegment(sketch, "E1258", {"start": v(-16.4, 20.99) * mm, "end": v(-16.44, 20.96) * mm});
            skLineSegment(sketch, "E1259", {"start": v(-16.44, 20.96) * mm, "end": v(-16.48, 20.95) * mm});
            skLineSegment(sketch, "E1260", {"start": v(-16.48, 20.95) * mm, "end": v(-16.54, 20.95) * mm});
            skLineSegment(sketch, "E1261", {"start": v(-16.54, 20.95) * mm, "end": v(-16.6, 20.96) * mm});
            skLineSegment(sketch, "E1262", {"start": v(-16.6, 20.96) * mm, "end": v(-16.66, 20.98) * mm});
            skLineSegment(sketch, "E1263", {"start": v(-16.66, 20.98) * mm, "end": v(-16.73, 21.01) * mm});
            skLineSegment(sketch, "E1264", {"start": v(-16.73, 21.01) * mm, "end": v(-16.8, 21.06) * mm});
            skLineSegment(sketch, "E1265", {"start": v(-16.8, 21.06) * mm, "end": v(-16.88, 21.12) * mm});
            skLineSegment(sketch, "E1266", {"start": v(-16.88, 21.12) * mm, "end": v(-16.97, 21.19) * mm});
            skLineSegment(sketch, "E1267", {"start": v(-16.97, 21.19) * mm, "end": v(-17.06, 21.27) * mm});
            skLineSegment(sketch, "E1268", {"start": v(-17.06, 21.27) * mm, "end": v(-17.15, 21.37) * mm});
            skLineSegment(sketch, "E1269", {"start": v(-17.15, 21.37) * mm, "end": v(-17.25, 21.48) * mm});
            skLineSegment(sketch, "E1270", {"start": v(-17.25, 21.48) * mm, "end": v(-17.35, 21.6) * mm});
            skLineSegment(sketch, "E1271", {"start": v(-17.35, 21.6) * mm, "end": v(-17.4, 21.67) * mm});
            skLineSegment(sketch, "E1272", {"start": v(-17.4, 21.67) * mm, "end": v(-17.4, 21.67) * mm});
            skLineSegment(sketch, "E1273", {"start": v(-17.4, 21.67) * mm, "end": v(-17.41, 21.69) * mm});
            skLineSegment(sketch, "E1274", {"start": v(-17.41, 21.69) * mm, "end": v(-17.43, 21.7) * mm});
            skLineSegment(sketch, "E1275", {"start": v(-17.43, 21.7) * mm, "end": v(-17.46, 21.74) * mm});
            skLineSegment(sketch, "E1276", {"start": v(-17.46, 21.74) * mm, "end": v(-17.5, 21.78) * mm});
            skLineSegment(sketch, "E1277", {"start": v(-17.5, 21.78) * mm, "end": v(-17.55, 21.82) * mm});
            skLineSegment(sketch, "E1278", {"start": v(-17.55, 21.82) * mm, "end": v(-17.6, 21.88) * mm});
            skLineSegment(sketch, "E1279", {"start": v(-17.6, 21.88) * mm, "end": v(-17.67, 21.94) * mm});
            skLineSegment(sketch, "E1280", {"start": v(-17.67, 21.94) * mm, "end": v(-17.75, 22) * mm});
            skLineSegment(sketch, "E1281", {"start": v(-17.75, 22) * mm, "end": v(-17.83, 22.08) * mm});
            skLineSegment(sketch, "E1282", {"start": v(-17.83, 22.08) * mm, "end": v(-17.93, 22.16) * mm});
            skLineSegment(sketch, "E1283", {"start": v(-17.93, 22.16) * mm, "end": v(-18.04, 22.24) * mm});
            skLineSegment(sketch, "E1284", {"start": v(-18.04, 22.24) * mm, "end": v(-18.17, 22.33) * mm});
            skLineSegment(sketch, "E1285", {"start": v(-18.17, 22.33) * mm, "end": v(-18.3, 22.43) * mm});
            skLineSegment(sketch, "E1286", {"start": v(-18.3, 22.43) * mm, "end": v(-18.45, 22.53) * mm});
            skLineSegment(sketch, "E1287", {"start": v(-18.45, 22.53) * mm, "end": v(-18.6, 22.63) * mm});
            skLineSegment(sketch, "E1288", {"start": v(-18.6, 22.63) * mm, "end": v(-18.77, 22.73) * mm});
            skLineSegment(sketch, "E1289", {"start": v(-18.77, 22.73) * mm, "end": v(-18.96, 22.84) * mm});
            skLineSegment(sketch, "E1290", {"start": v(-18.96, 22.84) * mm, "end": v(-19.15, 22.95) * mm});
            skLineSegment(sketch, "E1291", {"start": v(-19.15, 22.95) * mm, "end": v(-19.36, 23.06) * mm});
            skLineSegment(sketch, "E1292", {"start": v(-19.36, 23.06) * mm, "end": v(-19.58, 23.17) * mm});
            skLineSegment(sketch, "E1293", {"start": v(-19.58, 23.17) * mm, "end": v(-19.77, 23.26) * mm});
            skLineSegment(sketch, "E1294", {"start": v(-19.77, 23.26) * mm, "end": v(-20.45, 22.7) * mm});
            skLineSegment(sketch, "E1295", {"start": v(-20.45, 22.7) * mm, "end": v(-21.07, 22.1) * mm});
            skLineSegment(sketch, "E1296", {"start": v(-21.07, 22.1) * mm, "end": v(-21, 21.9) * mm});
            skLineSegment(sketch, "E1297", {"start": v(-21, 21.9) * mm, "end": v(-20.9, 21.67) * mm});
            skLineSegment(sketch, "E1298", {"start": v(-20.9, 21.67) * mm, "end": v(-20.82, 21.45) * mm});
            skLineSegment(sketch, "E1299", {"start": v(-20.82, 21.45) * mm, "end": v(-20.73, 21.24) * mm});
            skLineSegment(sketch, "E1300", {"start": v(-20.73, 21.24) * mm, "end": v(-20.65, 21.05) * mm});
            skLineSegment(sketch, "E1301", {"start": v(-20.65, 21.05) * mm, "end": v(-20.56, 20.87) * mm});
            skLineSegment(sketch, "E1302", {"start": v(-20.56, 20.87) * mm, "end": v(-20.47, 20.7) * mm});
            skLineSegment(sketch, "E1303", {"start": v(-20.47, 20.7) * mm, "end": v(-20.4, 20.54) * mm});
            skLineSegment(sketch, "E1304", {"start": v(-20.4, 20.54) * mm, "end": v(-20.31, 20.4) * mm});
            skLineSegment(sketch, "E1305", {"start": v(-20.31, 20.4) * mm, "end": v(-20.24, 20.27) * mm});
            skLineSegment(sketch, "E1306", {"start": v(-20.24, 20.27) * mm, "end": v(-20.16, 20.15) * mm});
            skLineSegment(sketch, "E1307", {"start": v(-20.16, 20.15) * mm, "end": v(-20.1, 20.04) * mm});
            skLineSegment(sketch, "E1308", {"start": v(-20.1, 20.04) * mm, "end": v(-20.03, 19.95) * mm});
            skLineSegment(sketch, "E1309", {"start": v(-20.03, 19.95) * mm, "end": v(-19.97, 19.87) * mm});
            skLineSegment(sketch, "E1310", {"start": v(-19.97, 19.87) * mm, "end": v(-19.92, 19.8) * mm});
            skLineSegment(sketch, "E1311", {"start": v(-19.92, 19.8) * mm, "end": v(-19.87, 19.73) * mm});
            skLineSegment(sketch, "E1312", {"start": v(-19.87, 19.73) * mm, "end": v(-19.83, 19.68) * mm});
            skLineSegment(sketch, "E1313", {"start": v(-19.83, 19.68) * mm, "end": v(-19.8, 19.64) * mm});
            skLineSegment(sketch, "E1314", {"start": v(-19.8, 19.64) * mm, "end": v(-19.77, 19.6) * mm});
            skLineSegment(sketch, "E1315", {"start": v(-19.77, 19.6) * mm, "end": v(-19.75, 19.59) * mm});
            skLineSegment(sketch, "E1316", {"start": v(-19.75, 19.59) * mm, "end": v(-19.74, 19.57) * mm});
            skLineSegment(sketch, "E1317", {"start": v(-19.74, 19.57) * mm, "end": v(-19.73, 19.57) * mm});
            skLineSegment(sketch, "E1318", {"start": v(-19.73, 19.57) * mm, "end": v(-19.67, 19.51) * mm});
            skLineSegment(sketch, "E1319", {"start": v(-19.67, 19.51) * mm, "end": v(-19.56, 19.4) * mm});
            skLineSegment(sketch, "E1320", {"start": v(-19.56, 19.4) * mm, "end": v(-19.46, 19.3) * mm});
            skLineSegment(sketch, "E1321", {"start": v(-19.46, 19.3) * mm, "end": v(-19.37, 19.19) * mm});
            skLineSegment(sketch, "E1322", {"start": v(-19.37, 19.19) * mm, "end": v(-19.3, 19.1) * mm});
            skLineSegment(sketch, "E1323", {"start": v(-19.3, 19.1) * mm, "end": v(-19.24, 19) * mm});
            skLineSegment(sketch, "E1324", {"start": v(-19.24, 19) * mm, "end": v(-19.19, 18.91) * mm});
            skLineSegment(sketch, "E1325", {"start": v(-19.19, 18.91) * mm, "end": v(-19.15, 18.83) * mm});
            skLineSegment(sketch, "E1326", {"start": v(-19.15, 18.83) * mm, "end": v(-19.12, 18.76) * mm});
            skLineSegment(sketch, "E1327", {"start": v(-19.12, 18.76) * mm, "end": v(-19.1, 18.7) * mm});
            skLineSegment(sketch, "E1328", {"start": v(-19.1, 18.7) * mm, "end": v(-19.1, 18.63) * mm});
            skLineSegment(sketch, "E1329", {"start": v(-19.1, 18.63) * mm, "end": v(-19.11, 18.58) * mm});
            skLineSegment(sketch, "E1330", {"start": v(-19.11, 18.58) * mm, "end": v(-19.13, 18.54) * mm});
            skLineSegment(sketch, "E1331", {"start": v(-19.13, 18.54) * mm, "end": v(-19.16, 18.51) * mm});
            skLineSegment(sketch, "E1332", {"start": v(-19.16, 18.51) * mm, "end": v(-19.23, 18.44) * mm});
            skLineSegment(sketch, "E1333", {"start": v(-19.23, 18.44) * mm, "end": v(-19.6, 18.03) * mm});
            skLineSegment(sketch, "E1334", {"start": v(-19.6, 18.03) * mm, "end": v(-19.98, 17.62) * mm});
            skLineSegment(sketch, "E1335", {"start": v(-19.98, 17.62) * mm, "end": v(-20.35, 17.2) * mm});
            skLineSegment(sketch, "E1336", {"start": v(-20.35, 17.2) * mm, "end": v(-20.41, 17.12) * mm});
            skLineSegment(sketch, "E1337", {"start": v(-20.41, 17.12) * mm, "end": v(-20.44, 17.09) * mm});
            skLineSegment(sketch, "E1338", {"start": v(-20.44, 17.09) * mm, "end": v(-20.48, 17.06) * mm});
            skLineSegment(sketch, "E1339", {"start": v(-20.48, 17.06) * mm, "end": v(-20.53, 17.05) * mm});
            skLineSegment(sketch, "E1340", {"start": v(-20.53, 17.05) * mm, "end": v(-20.59, 17.05) * mm});
            skLineSegment(sketch, "E1341", {"start": v(-20.59, 17.05) * mm, "end": v(-20.65, 17.06) * mm});
            skLineSegment(sketch, "E1342", {"start": v(-20.65, 17.06) * mm, "end": v(-20.73, 17.08) * mm});
            skLineSegment(sketch, "E1343", {"start": v(-20.73, 17.08) * mm, "end": v(-20.81, 17.1) * mm});
            skLineSegment(sketch, "E1344", {"start": v(-20.81, 17.1) * mm, "end": v(-20.9, 17.14) * mm});
            skLineSegment(sketch, "E1345", {"start": v(-20.9, 17.14) * mm, "end": v(-21, 17.2) * mm});
            skLineSegment(sketch, "E1346", {"start": v(-21, 17.2) * mm, "end": v(-21.1, 17.26) * mm});
            skLineSegment(sketch, "E1347", {"start": v(-21.1, 17.26) * mm, "end": v(-21.22, 17.33) * mm});
            skLineSegment(sketch, "E1348", {"start": v(-21.22, 17.33) * mm, "end": v(-21.34, 17.42) * mm});
            skLineSegment(sketch, "E1349", {"start": v(-21.34, 17.42) * mm, "end": v(-21.46, 17.52) * mm});
            skLineSegment(sketch, "E1350", {"start": v(-21.46, 17.52) * mm, "end": v(-21.53, 17.58) * mm});
            skLineSegment(sketch, "E1351", {"start": v(-21.53, 17.58) * mm, "end": v(-21.53, 17.58) * mm});
            skLineSegment(sketch, "E1352", {"start": v(-21.53, 17.58) * mm, "end": v(-21.54, 17.6) * mm});
            skLineSegment(sketch, "E1353", {"start": v(-21.54, 17.6) * mm, "end": v(-21.57, 17.6) * mm});
            skLineSegment(sketch, "E1354", {"start": v(-21.57, 17.6) * mm, "end": v(-21.6, 17.63) * mm});
            skLineSegment(sketch, "E1355", {"start": v(-21.6, 17.63) * mm, "end": v(-21.64, 17.66) * mm});
            skLineSegment(sketch, "E1356", {"start": v(-21.64, 17.66) * mm, "end": v(-21.7, 17.7) * mm});
            skLineSegment(sketch, "E1357", {"start": v(-21.7, 17.7) * mm, "end": v(-21.77, 17.74) * mm});
            skLineSegment(sketch, "E1358", {"start": v(-21.77, 17.74) * mm, "end": v(-21.84, 17.79) * mm});
            skLineSegment(sketch, "E1359", {"start": v(-21.84, 17.79) * mm, "end": v(-21.93, 17.84) * mm});
            skLineSegment(sketch, "E1360", {"start": v(-21.93, 17.84) * mm, "end": v(-22.04, 17.89) * mm});
            skLineSegment(sketch, "E1361", {"start": v(-22.04, 17.89) * mm, "end": v(-22.15, 17.95) * mm});
            skLineSegment(sketch, "E1362", {"start": v(-22.15, 17.95) * mm, "end": v(-22.27, 18) * mm});
            skLineSegment(sketch, "E1363", {"start": v(-22.27, 18) * mm, "end": v(-22.41, 18.07) * mm});
            skLineSegment(sketch, "E1364", {"start": v(-22.41, 18.07) * mm, "end": v(-22.56, 18.13) * mm});
            skLineSegment(sketch, "E1365", {"start": v(-22.56, 18.13) * mm, "end": v(-22.73, 18.2) * mm});
            skLineSegment(sketch, "E1366", {"start": v(-22.73, 18.2) * mm, "end": v(-22.9, 18.27) * mm});
            skLineSegment(sketch, "E1367", {"start": v(-22.9, 18.27) * mm, "end": v(-23.09, 18.33) * mm});
            skLineSegment(sketch, "E1368", {"start": v(-23.09, 18.33) * mm, "end": v(-23.3, 18.4) * mm});
            skLineSegment(sketch, "E1369", {"start": v(-23.3, 18.4) * mm, "end": v(-23.5, 18.47) * mm});
            skLineSegment(sketch, "E1370", {"start": v(-23.5, 18.47) * mm, "end": v(-23.73, 18.53) * mm});
            skLineSegment(sketch, "E1371", {"start": v(-23.73, 18.53) * mm, "end": v(-23.97, 18.6) * mm});
            skLineSegment(sketch, "E1372", {"start": v(-23.97, 18.6) * mm, "end": v(-24.17, 18.64) * mm});
            skLineSegment(sketch, "E1373", {"start": v(-24.17, 18.64) * mm, "end": v(-24.72, 17.96) * mm});
            skLineSegment(sketch, "E1374", {"start": v(-24.72, 17.96) * mm, "end": v(-25.2, 17.23) * mm});
            skLineSegment(sketch, "E1375", {"start": v(-25.2, 17.23) * mm, "end": v(-25.1, 17.05) * mm});
            skLineSegment(sketch, "E1376", {"start": v(-25.1, 17.05) * mm, "end": v(-24.96, 16.85) * mm});
            skLineSegment(sketch, "E1377", {"start": v(-24.96, 16.85) * mm, "end": v(-24.83, 16.65) * mm});
            skLineSegment(sketch, "E1378", {"start": v(-24.83, 16.65) * mm, "end": v(-24.7, 16.47) * mm});
            skLineSegment(sketch, "E1379", {"start": v(-24.7, 16.47) * mm, "end": v(-24.57, 16.3) * mm});
            skLineSegment(sketch, "E1380", {"start": v(-24.57, 16.3) * mm, "end": v(-24.45, 16.14) * mm});
            skLineSegment(sketch, "E1381", {"start": v(-24.45, 16.14) * mm, "end": v(-24.33, 15.99) * mm});
            skLineSegment(sketch, "E1382", {"start": v(-24.33, 15.99) * mm, "end": v(-24.22, 15.85) * mm});
            skLineSegment(sketch, "E1383", {"start": v(-24.22, 15.85) * mm, "end": v(-24.11, 15.73) * mm});
            skLineSegment(sketch, "E1384", {"start": v(-24.11, 15.73) * mm, "end": v(-24, 15.62) * mm});
            skLineSegment(sketch, "E1385", {"start": v(-24, 15.62) * mm, "end": v(-23.91, 15.52) * mm});
            skLineSegment(sketch, "E1386", {"start": v(-23.91, 15.52) * mm, "end": v(-23.82, 15.43) * mm});
            skLineSegment(sketch, "E1387", {"start": v(-23.82, 15.43) * mm, "end": v(-23.74, 15.35) * mm});
            skLineSegment(sketch, "E1388", {"start": v(-23.74, 15.35) * mm, "end": v(-23.67, 15.28) * mm});
            skLineSegment(sketch, "E1389", {"start": v(-23.67, 15.28) * mm, "end": v(-23.6, 15.22) * mm});
            skLineSegment(sketch, "E1390", {"start": v(-23.6, 15.22) * mm, "end": v(-23.54, 15.17) * mm});
            skLineSegment(sketch, "E1391", {"start": v(-23.54, 15.17) * mm, "end": v(-23.49, 15.13) * mm});
            skLineSegment(sketch, "E1392", {"start": v(-23.49, 15.13) * mm, "end": v(-23.45, 15.1) * mm});
            skLineSegment(sketch, "E1393", {"start": v(-23.45, 15.1) * mm, "end": v(-23.41, 15.07) * mm});
            skLineSegment(sketch, "E1394", {"start": v(-23.41, 15.07) * mm, "end": v(-23.39, 15.05) * mm});
            skLineSegment(sketch, "E1395", {"start": v(-23.39, 15.05) * mm, "end": v(-23.37, 15.04) * mm});
            skLineSegment(sketch, "E1396", {"start": v(-23.37, 15.04) * mm, "end": v(-23.37, 15.04) * mm});
            skLineSegment(sketch, "E1397", {"start": v(-23.37, 15.04) * mm, "end": v(-23.3, 15) * mm});
            skLineSegment(sketch, "E1398", {"start": v(-23.3, 15) * mm, "end": v(-23.16, 14.91) * mm});
            skLineSegment(sketch, "E1399", {"start": v(-23.16, 14.91) * mm, "end": v(-23.04, 14.83) * mm});
            skLineSegment(sketch, "E1400", {"start": v(-23.04, 14.83) * mm, "end": v(-22.94, 14.74) * mm});
            skLineSegment(sketch, "E1401", {"start": v(-22.94, 14.74) * mm, "end": v(-22.84, 14.66) * mm});
            skLineSegment(sketch, "E1402", {"start": v(-22.84, 14.66) * mm, "end": v(-22.77, 14.58) * mm});
            skLineSegment(sketch, "E1403", {"start": v(-22.77, 14.58) * mm, "end": v(-22.7, 14.5) * mm});
            skLineSegment(sketch, "E1404", {"start": v(-22.7, 14.5) * mm, "end": v(-22.65, 14.44) * mm});
            skLineSegment(sketch, "E1405", {"start": v(-22.65, 14.44) * mm, "end": v(-22.6, 14.37) * mm});
            skLineSegment(sketch, "E1406", {"start": v(-22.6, 14.37) * mm, "end": v(-22.58, 14.31) * mm});
            skLineSegment(sketch, "E1407", {"start": v(-22.58, 14.31) * mm, "end": v(-22.56, 14.25) * mm});
            skLineSegment(sketch, "E1408", {"start": v(-22.56, 14.25) * mm, "end": v(-22.56, 14.2) * mm});
            skLineSegment(sketch, "E1409", {"start": v(-22.56, 14.2) * mm, "end": v(-22.57, 14.16) * mm});
            skLineSegment(sketch, "E1410", {"start": v(-22.57, 14.16) * mm, "end": v(-22.59, 14.12) * mm});
            skLineSegment(sketch, "E1411", {"start": v(-22.59, 14.12) * mm, "end": v(-22.64, 14.04) * mm});
            skLineSegment(sketch, "E1412", {"start": v(-22.64, 14.04) * mm, "end": v(-22.93, 13.56) * mm});
            skLineSegment(sketch, "E1413", {"start": v(-22.93, 13.56) * mm, "end": v(-23.2, 13.08) * mm});
            skLineSegment(sketch, "E1414", {"start": v(-23.2, 13.08) * mm, "end": v(-23.48, 12.59) * mm});
            skLineSegment(sketch, "E1415", {"start": v(-23.48, 12.59) * mm, "end": v(-23.52, 12.5) * mm});
            skLineSegment(sketch, "E1416", {"start": v(-23.52, 12.5) * mm, "end": v(-23.55, 12.46) * mm});
            skLineSegment(sketch, "E1417", {"start": v(-23.55, 12.46) * mm, "end": v(-23.58, 12.43) * mm});
            skLineSegment(sketch, "E1418", {"start": v(-23.58, 12.43) * mm, "end": v(-23.63, 12.41) * mm});
            skLineSegment(sketch, "E1419", {"start": v(-23.63, 12.41) * mm, "end": v(-23.68, 12.4) * mm});
            skLineSegment(sketch, "E1420", {"start": v(-23.68, 12.4) * mm, "end": v(-23.75, 12.4) * mm});
            skLineSegment(sketch, "E1421", {"start": v(-23.75, 12.4) * mm, "end": v(-23.83, 12.4) * mm});
            skLineSegment(sketch, "E1422", {"start": v(-23.83, 12.4) * mm, "end": v(-23.92, 12.4) * mm});
            skLineSegment(sketch, "E1423", {"start": v(-23.92, 12.4) * mm, "end": v(-24.01, 12.42) * mm});
            skLineSegment(sketch, "E1424", {"start": v(-24.01, 12.42) * mm, "end": v(-24.12, 12.45) * mm});
            skLineSegment(sketch, "E1425", {"start": v(-24.12, 12.45) * mm, "end": v(-24.24, 12.5) * mm});
            skLineSegment(sketch, "E1426", {"start": v(-24.24, 12.5) * mm, "end": v(-24.36, 12.54) * mm});
            skLineSegment(sketch, "E1427", {"start": v(-24.36, 12.54) * mm, "end": v(-24.5, 12.6) * mm});
            skLineSegment(sketch, "E1428", {"start": v(-24.5, 12.6) * mm, "end": v(-24.64, 12.68) * mm});
            skLineSegment(sketch, "E1429", {"start": v(-24.64, 12.68) * mm, "end": v(-24.71, 12.72) * mm});
            skLineSegment(sketch, "E1430", {"start": v(-24.71, 12.72) * mm, "end": v(-24.71, 12.72) * mm});
            skLineSegment(sketch, "E1431", {"start": v(-24.71, 12.72) * mm, "end": v(-24.73, 12.73) * mm});
            skLineSegment(sketch, "E1432", {"start": v(-24.73, 12.73) * mm, "end": v(-24.76, 12.74) * mm});
            skLineSegment(sketch, "E1433", {"start": v(-24.76, 12.74) * mm, "end": v(-24.8, 12.76) * mm});
            skLineSegment(sketch, "E1434", {"start": v(-24.8, 12.76) * mm, "end": v(-24.84, 12.78) * mm});
            skLineSegment(sketch, "E1435", {"start": v(-24.84, 12.78) * mm, "end": v(-24.9, 12.8) * mm});
            skLineSegment(sketch, "E1436", {"start": v(-24.9, 12.8) * mm, "end": v(-24.98, 12.83) * mm});
            skLineSegment(sketch, "E1437", {"start": v(-24.98, 12.83) * mm, "end": v(-25.07, 12.86) * mm});
            skLineSegment(sketch, "E1438", {"start": v(-25.07, 12.86) * mm, "end": v(-25.16, 12.89) * mm});
            skLineSegment(sketch, "E1439", {"start": v(-25.16, 12.89) * mm, "end": v(-25.27, 12.92) * mm});
            skLineSegment(sketch, "E1440", {"start": v(-25.27, 12.92) * mm, "end": v(-25.4, 12.95) * mm});
            skLineSegment(sketch, "E1441", {"start": v(-25.4, 12.95) * mm, "end": v(-25.53, 12.98) * mm});
            skLineSegment(sketch, "E1442", {"start": v(-25.53, 12.98) * mm, "end": v(-25.68, 13.01) * mm});
            skLineSegment(sketch, "E1443", {"start": v(-25.68, 13.01) * mm, "end": v(-25.84, 13.05) * mm});
            skLineSegment(sketch, "E1444", {"start": v(-25.84, 13.05) * mm, "end": v(-26.01, 13.08) * mm});
            skLineSegment(sketch, "E1445", {"start": v(-26.01, 13.08) * mm, "end": v(-26.2, 13.1) * mm});
            skLineSegment(sketch, "E1446", {"start": v(-26.2, 13.1) * mm, "end": v(-26.4, 13.13) * mm});
            skLineSegment(sketch, "E1447", {"start": v(-26.4, 13.13) * mm, "end": v(-26.6, 13.15) * mm});
            skLineSegment(sketch, "E1448", {"start": v(-26.6, 13.15) * mm, "end": v(-26.83, 13.17) * mm});
            skLineSegment(sketch, "E1449", {"start": v(-26.83, 13.17) * mm, "end": v(-27.07, 13.2) * mm});
            skLineSegment(sketch, "E1450", {"start": v(-27.07, 13.2) * mm, "end": v(-27.32, 13.2) * mm});
            skLineSegment(sketch, "E1451", {"start": v(-27.32, 13.2) * mm, "end": v(-27.52, 13.2) * mm});
            skLineSegment(sketch, "E1452", {"start": v(-27.52, 13.2) * mm, "end": v(-27.92, 12.43) * mm});
            skLineSegment(sketch, "E1453", {"start": v(-27.92, 12.43) * mm, "end": v(-28.23, 11.61) * mm});
            skLineSegment(sketch, "E1454", {"start": v(-28.23, 11.61) * mm, "end": v(-28.09, 11.47) * mm});
            skLineSegment(sketch, "E1455", {"start": v(-28.09, 11.47) * mm, "end": v(-27.91, 11.29) * mm});
            skLineSegment(sketch, "E1456", {"start": v(-27.91, 11.29) * mm, "end": v(-27.74, 11.12) * mm});
            skLineSegment(sketch, "E1457", {"start": v(-27.74, 11.12) * mm, "end": v(-27.58, 10.97) * mm});
            skLineSegment(sketch, "E1458", {"start": v(-27.58, 10.97) * mm, "end": v(-27.42, 10.83) * mm});
            skLineSegment(sketch, "E1459", {"start": v(-27.42, 10.83) * mm, "end": v(-27.27, 10.7) * mm});
            skLineSegment(sketch, "E1460", {"start": v(-27.27, 10.7) * mm, "end": v(-27.12, 10.58) * mm});
            skLineSegment(sketch, "E1461", {"start": v(-27.12, 10.58) * mm, "end": v(-26.99, 10.47) * mm});
            skLineSegment(sketch, "E1462", {"start": v(-26.99, 10.47) * mm, "end": v(-26.85, 10.38) * mm});
            skLineSegment(sketch, "E1463", {"start": v(-26.85, 10.38) * mm, "end": v(-26.73, 10.29) * mm});
            skLineSegment(sketch, "E1464", {"start": v(-26.73, 10.29) * mm, "end": v(-26.62, 10.2) * mm});
            skLineSegment(sketch, "E1465", {"start": v(-26.62, 10.2) * mm, "end": v(-26.51, 10.14) * mm});
            skLineSegment(sketch, "E1466", {"start": v(-26.51, 10.14) * mm, "end": v(-26.41, 10.08) * mm});
            skLineSegment(sketch, "E1467", {"start": v(-26.41, 10.08) * mm, "end": v(-26.33, 10.03) * mm});
            skLineSegment(sketch, "E1468", {"start": v(-26.33, 10.03) * mm, "end": v(-26.25, 9.98) * mm});
            skLineSegment(sketch, "E1469", {"start": v(-26.25, 9.98) * mm, "end": v(-26.18, 9.94) * mm});
            skLineSegment(sketch, "E1470", {"start": v(-26.18, 9.94) * mm, "end": v(-26.12, 9.91) * mm});
            skLineSegment(sketch, "E1471", {"start": v(-26.12, 9.91) * mm, "end": v(-26.07, 9.89) * mm});
            skLineSegment(sketch, "E1472", {"start": v(-26.07, 9.89) * mm, "end": v(-26.03, 9.87) * mm});
            skLineSegment(sketch, "E1473", {"start": v(-26.03, 9.87) * mm, "end": v(-26, 9.86) * mm});
            skLineSegment(sketch, "E1474", {"start": v(-26, 9.86) * mm, "end": v(-26, 9.85) * mm});
            skLineSegment(sketch, "E1475", {"start": v(-26, 9.85) * mm, "end": v(-25.99, 9.85) * mm});
            skLineSegment(sketch, "E1476", {"start": v(-25.99, 9.85) * mm, "end": v(-25.9, 9.82) * mm});
            skLineSegment(sketch, "E1477", {"start": v(-25.9, 9.82) * mm, "end": v(-25.76, 9.77) * mm});
            skLineSegment(sketch, "E1478", {"start": v(-25.76, 9.77) * mm, "end": v(-25.62, 9.71) * mm});
            skLineSegment(sketch, "E1479", {"start": v(-25.62, 9.71) * mm, "end": v(-25.5, 9.65) * mm});
            skLineSegment(sketch, "E1480", {"start": v(-25.5, 9.65) * mm, "end": v(-25.4, 9.6) * mm});
            skLineSegment(sketch, "E1481", {"start": v(-25.4, 9.6) * mm, "end": v(-25.3, 9.53) * mm});
            skLineSegment(sketch, "E1482", {"start": v(-25.3, 9.53) * mm, "end": v(-25.22, 9.47) * mm});
            skLineSegment(sketch, "E1483", {"start": v(-25.22, 9.47) * mm, "end": v(-25.15, 9.41) * mm});
            skLineSegment(sketch, "E1484", {"start": v(-25.15, 9.41) * mm, "end": v(-25.1, 9.36) * mm});
            skLineSegment(sketch, "E1485", {"start": v(-25.1, 9.36) * mm, "end": v(-25.06, 9.3) * mm});
            skLineSegment(sketch, "E1486", {"start": v(-25.06, 9.3) * mm, "end": v(-25.03, 9.25) * mm});
            skLineSegment(sketch, "E1487", {"start": v(-25.03, 9.25) * mm, "end": v(-25.02, 9.2) * mm});
            skLineSegment(sketch, "E1488", {"start": v(-25.02, 9.2) * mm, "end": v(-25.02, 9.16) * mm});
            skLineSegment(sketch, "E1489", {"start": v(-25.02, 9.16) * mm, "end": v(-25.03, 9.12) * mm});
            skLineSegment(sketch, "E1490", {"start": v(-25.03, 9.12) * mm, "end": v(-25.06, 9.02) * mm});
            skLineSegment(sketch, "E1491", {"start": v(-25.06, 9.02) * mm, "end": v(-25.25, 8.5) * mm});
            skLineSegment(sketch, "E1492", {"start": v(-25.25, 8.5) * mm, "end": v(-25.42, 7.97) * mm});
            skLineSegment(sketch, "E1493", {"start": v(-25.42, 7.97) * mm, "end": v(-25.58, 7.43) * mm});
            skLineSegment(sketch, "E1494", {"start": v(-25.58, 7.43) * mm, "end": v(-25.6, 7.33) * mm});
            skLineSegment(sketch, "E1495", {"start": v(-25.6, 7.33) * mm, "end": v(-25.62, 7.3) * mm});
            skLineSegment(sketch, "E1496", {"start": v(-25.62, 7.3) * mm, "end": v(-25.65, 7.26) * mm});
            skLineSegment(sketch, "E1497", {"start": v(-25.65, 7.26) * mm, "end": v(-25.69, 7.23) * mm});
            skLineSegment(sketch, "E1498", {"start": v(-25.69, 7.23) * mm, "end": v(-25.74, 7.2) * mm});
            skLineSegment(sketch, "E1499", {"start": v(-25.74, 7.2) * mm, "end": v(-25.8, 7.18) * mm});
            skLineSegment(sketch, "E1500", {"start": v(-25.8, 7.18) * mm, "end": v(-25.88, 7.17) * mm});
            skLineSegment(sketch, "E1501", {"start": v(-25.88, 7.17) * mm, "end": v(-25.97, 7.16) * mm});
            skLineSegment(sketch, "E1502", {"start": v(-25.97, 7.16) * mm, "end": v(-26.07, 7.16) * mm});
            skLineSegment(sketch, "E1503", {"start": v(-26.07, 7.16) * mm, "end": v(-26.18, 7.17) * mm});
            skLineSegment(sketch, "E1504", {"start": v(-26.18, 7.17) * mm, "end": v(-26.3, 7.18) * mm});
            skLineSegment(sketch, "E1505", {"start": v(-26.3, 7.18) * mm, "end": v(-26.44, 7.2) * mm});
            skLineSegment(sketch, "E1506", {"start": v(-26.44, 7.2) * mm, "end": v(-26.58, 7.24) * mm});
            skLineSegment(sketch, "E1507", {"start": v(-26.58, 7.24) * mm, "end": v(-26.73, 7.28) * mm});
            skLineSegment(sketch, "E1508", {"start": v(-26.73, 7.28) * mm, "end": v(-26.82, 7.3) * mm});
            skLineSegment(sketch, "E1509", {"start": v(-26.82, 7.3) * mm, "end": v(-26.82, 7.3) * mm});
            skLineSegment(sketch, "E1510", {"start": v(-26.82, 7.3) * mm, "end": v(-26.84, 7.3) * mm});
            skLineSegment(sketch, "E1511", {"start": v(-26.84, 7.3) * mm, "end": v(-26.86, 7.32) * mm});
            skLineSegment(sketch, "E1512", {"start": v(-26.86, 7.32) * mm, "end": v(-26.9, 7.32) * mm});
            skLineSegment(sketch, "E1513", {"start": v(-26.9, 7.32) * mm, "end": v(-26.96, 7.33) * mm});
            skLineSegment(sketch, "E1514", {"start": v(-26.96, 7.33) * mm, "end": v(-27.02, 7.34) * mm});
            skLineSegment(sketch, "E1515", {"start": v(-27.02, 7.34) * mm, "end": v(-27.1, 7.35) * mm});
            skLineSegment(sketch, "E1516", {"start": v(-27.1, 7.35) * mm, "end": v(-27.2, 7.36) * mm});
            skLineSegment(sketch, "E1517", {"start": v(-27.2, 7.36) * mm, "end": v(-27.3, 7.37) * mm});
            skLineSegment(sketch, "E1518", {"start": v(-27.3, 7.37) * mm, "end": v(-27.4, 7.38) * mm});
            skLineSegment(sketch, "E1519", {"start": v(-27.4, 7.38) * mm, "end": v(-27.53, 7.39) * mm});
            skLineSegment(sketch, "E1520", {"start": v(-27.53, 7.39) * mm, "end": v(-27.67, 7.39) * mm});
            skLineSegment(sketch, "E1521", {"start": v(-27.67, 7.39) * mm, "end": v(-27.82, 7.4) * mm});
            skLineSegment(sketch, "E1522", {"start": v(-27.82, 7.4) * mm, "end": v(-27.99, 7.39) * mm});
            skLineSegment(sketch, "E1523", {"start": v(-27.99, 7.39) * mm, "end": v(-28.16, 7.38) * mm});
            skLineSegment(sketch, "E1524", {"start": v(-28.16, 7.38) * mm, "end": v(-28.35, 7.37) * mm});
            skLineSegment(sketch, "E1525", {"start": v(-28.35, 7.37) * mm, "end": v(-28.55, 7.36) * mm});
            skLineSegment(sketch, "E1526", {"start": v(-28.55, 7.36) * mm, "end": v(-28.76, 7.33) * mm});
            skLineSegment(sketch, "E1527", {"start": v(-28.76, 7.33) * mm, "end": v(-28.98, 7.3) * mm});
            skLineSegment(sketch, "E1528", {"start": v(-28.98, 7.3) * mm, "end": v(-29.22, 7.28) * mm});
            skLineSegment(sketch, "E1529", {"start": v(-29.22, 7.28) * mm, "end": v(-29.46, 7.23) * mm});
            skLineSegment(sketch, "E1530", {"start": v(-29.46, 7.23) * mm, "end": v(-29.66, 7.2) * mm});
            skLineSegment(sketch, "E1531", {"start": v(-29.66, 7.2) * mm, "end": v(-29.89, 6.35) * mm});
            skLineSegment(sketch, "E1532", {"start": v(-29.89, 6.35) * mm, "end": v(-30.03, 5.49) * mm});
            skLineSegment(sketch, "E1533", {"start": v(-30.03, 5.49) * mm, "end": v(-29.86, 5.37) * mm});
            skLineSegment(sketch, "E1534", {"start": v(-29.86, 5.37) * mm, "end": v(-29.65, 5.24) * mm});
            skLineSegment(sketch, "E1535", {"start": v(-29.65, 5.24) * mm, "end": v(-29.45, 5.11) * mm});
            skLineSegment(sketch, "E1536", {"start": v(-29.45, 5.11) * mm, "end": v(-29.26, 5) * mm});
            skLineSegment(sketch, "E1537", {"start": v(-29.26, 5) * mm, "end": v(-29.07, 4.9) * mm});
            skLineSegment(sketch, "E1538", {"start": v(-29.07, 4.9) * mm, "end": v(-28.9, 4.8) * mm});
            skLineSegment(sketch, "E1539", {"start": v(-28.9, 4.8) * mm, "end": v(-28.73, 4.71) * mm});
            skLineSegment(sketch, "E1540", {"start": v(-28.73, 4.71) * mm, "end": v(-28.57, 4.63) * mm});
            skLineSegment(sketch, "E1541", {"start": v(-28.57, 4.63) * mm, "end": v(-28.42, 4.57) * mm});
            skLineSegment(sketch, "E1542", {"start": v(-28.42, 4.57) * mm, "end": v(-28.29, 4.5) * mm});
            skLineSegment(sketch, "E1543", {"start": v(-28.29, 4.5) * mm, "end": v(-28.16, 4.45) * mm});
            skLineSegment(sketch, "E1544", {"start": v(-28.16, 4.45) * mm, "end": v(-28.04, 4.4) * mm});
            skLineSegment(sketch, "E1545", {"start": v(-28.04, 4.4) * mm, "end": v(-27.93, 4.37) * mm});
            skLineSegment(sketch, "E1546", {"start": v(-27.93, 4.37) * mm, "end": v(-27.83, 4.33) * mm});
            skLineSegment(sketch, "E1547", {"start": v(-27.83, 4.33) * mm, "end": v(-27.75, 4.3) * mm});
            skLineSegment(sketch, "E1548", {"start": v(-27.75, 4.3) * mm, "end": v(-27.67, 4.28) * mm});
            skLineSegment(sketch, "E1549", {"start": v(-27.67, 4.28) * mm, "end": v(-27.6, 4.27) * mm});
            skLineSegment(sketch, "E1550", {"start": v(-27.6, 4.27) * mm, "end": v(-27.56, 4.25) * mm});
            skLineSegment(sketch, "E1551", {"start": v(-27.56, 4.25) * mm, "end": v(-27.52, 4.24) * mm});
            skLineSegment(sketch, "E1552", {"start": v(-27.52, 4.24) * mm, "end": v(-27.49, 4.24) * mm});
            skLineSegment(sketch, "E1553", {"start": v(-27.49, 4.24) * mm, "end": v(-27.47, 4.23) * mm});
            skLineSegment(sketch, "E1554", {"start": v(-27.47, 4.23) * mm, "end": v(-27.47, 4.23) * mm});
            skLineSegment(sketch, "E1555", {"start": v(-27.47, 4.23) * mm, "end": v(-27.38, 4.22) * mm});
            skLineSegment(sketch, "E1556", {"start": v(-27.38, 4.22) * mm, "end": v(-27.23, 4.2) * mm});
            skLineSegment(sketch, "E1557", {"start": v(-27.23, 4.2) * mm, "end": v(-27.08, 4.17) * mm});
            skLineSegment(sketch, "E1558", {"start": v(-27.08, 4.17) * mm, "end": v(-26.95, 4.14) * mm});
            skLineSegment(sketch, "E1559", {"start": v(-26.95, 4.14) * mm, "end": v(-26.83, 4.1) * mm});
            skLineSegment(sketch, "E1560", {"start": v(-26.83, 4.1) * mm, "end": v(-26.73, 4.06) * mm});
            skLineSegment(sketch, "E1561", {"start": v(-26.73, 4.06) * mm, "end": v(-26.64, 4.02) * mm});
            skLineSegment(sketch, "E1562", {"start": v(-26.64, 4.02) * mm, "end": v(-26.56, 3.98) * mm});
            skLineSegment(sketch, "E1563", {"start": v(-26.56, 3.98) * mm, "end": v(-26.5, 3.94) * mm});
            skLineSegment(sketch, "E1564", {"start": v(-26.5, 3.94) * mm, "end": v(-26.45, 3.9) * mm});
            skLineSegment(sketch, "E1565", {"start": v(-26.45, 3.9) * mm, "end": v(-26.4, 3.85) * mm});
            skLineSegment(sketch, "E1566", {"start": v(-26.4, 3.85) * mm, "end": v(-26.39, 3.8) * mm});
            skLineSegment(sketch, "E1567", {"start": v(-26.39, 3.8) * mm, "end": v(-26.38, 3.76) * mm});
            skLineSegment(sketch, "E1568", {"start": v(-26.38, 3.76) * mm, "end": v(-26.38, 3.72) * mm});
            skLineSegment(sketch, "E1569", {"start": v(-26.38, 3.72) * mm, "end": v(-26.4, 3.62) * mm});
            skLineSegment(sketch, "E1570", {"start": v(-26.4, 3.62) * mm, "end": v(-26.46, 3.06) * mm});
            skLineSegment(sketch, "E1571", {"start": v(-26.46, 3.06) * mm, "end": v(-26.52, 2.5) * mm});
            skLineSegment(sketch, "E1572", {"start": v(-26.52, 2.5) * mm, "end": v(-26.57, 1.95) * mm});
            skLineSegment(sketch, "E1573", {"start": v(-26.57, 1.95) * mm, "end": v(-26.57, 1.85) * mm});
            skLineSegment(sketch, "E1574", {"start": v(-26.57, 1.85) * mm, "end": v(-26.58, 1.8) * mm});
            skLineSegment(sketch, "E1575", {"start": v(-26.58, 1.8) * mm, "end": v(-26.6, 1.77) * mm});
            skLineSegment(sketch, "E1576", {"start": v(-26.6, 1.77) * mm, "end": v(-26.63, 1.73) * mm});
            skLineSegment(sketch, "E1577", {"start": v(-26.63, 1.73) * mm, "end": v(-26.68, 1.7) * mm});
            skLineSegment(sketch, "E1578", {"start": v(-26.68, 1.7) * mm, "end": v(-26.74, 1.66) * mm});
            skLineSegment(sketch, "E1579", {"start": v(-26.74, 1.66) * mm, "end": v(-26.8, 1.63) * mm});
            skLineSegment(sketch, "E1580", {"start": v(-26.8, 1.63) * mm, "end": v(-26.9, 1.6) * mm});
            skLineSegment(sketch, "E1581", {"start": v(-26.9, 1.6) * mm, "end": v(-26.99, 1.58) * mm});
            skLineSegment(sketch, "E1582", {"start": v(-26.99, 1.58) * mm, "end": v(-27.1, 1.57) * mm});
            skLineSegment(sketch, "E1583", {"start": v(-27.1, 1.57) * mm, "end": v(-27.22, 1.56) * mm});
            skLineSegment(sketch, "E1584", {"start": v(-27.22, 1.56) * mm, "end": v(-27.36, 1.55) * mm});
            skLineSegment(sketch, "E1585", {"start": v(-27.36, 1.55) * mm, "end": v(-27.5, 1.55) * mm});
            skLineSegment(sketch, "E1586", {"start": v(-27.5, 1.55) * mm, "end": v(-27.66, 1.56) * mm});
            skLineSegment(sketch, "E1587", {"start": v(-27.66, 1.56) * mm, "end": v(-27.75, 1.57) * mm});
            skLineSegment(sketch, "E1588", {"start": v(-27.75, 1.57) * mm, "end": v(-27.75, 1.57) * mm});
            skLineSegment(sketch, "E1589", {"start": v(-27.75, 1.57) * mm, "end": v(-27.77, 1.57) * mm});
            skLineSegment(sketch, "E1590", {"start": v(-27.77, 1.57) * mm, "end": v(-27.8, 1.57) * mm});
            skLineSegment(sketch, "E1591", {"start": v(-27.8, 1.57) * mm, "end": v(-27.84, 1.57) * mm});
            skLineSegment(sketch, "E1592", {"start": v(-27.84, 1.57) * mm, "end": v(-27.9, 1.57) * mm});
            skLineSegment(sketch, "E1593", {"start": v(-27.9, 1.57) * mm, "end": v(-27.96, 1.56) * mm});
            skLineSegment(sketch, "E1594", {"start": v(-27.96, 1.56) * mm, "end": v(-28.04, 1.56) * mm});
            skLineSegment(sketch, "E1595", {"start": v(-28.04, 1.56) * mm, "end": v(-28.13, 1.55) * mm});
            skLineSegment(sketch, "E1596", {"start": v(-28.13, 1.55) * mm, "end": v(-28.23, 1.54) * mm});
            skLineSegment(sketch, "E1597", {"start": v(-28.23, 1.54) * mm, "end": v(-28.34, 1.52) * mm});
            skLineSegment(sketch, "E1598", {"start": v(-28.34, 1.52) * mm, "end": v(-28.47, 1.5) * mm});
            skLineSegment(sketch, "E1599", {"start": v(-28.47, 1.5) * mm, "end": v(-28.6, 1.48) * mm});
            skLineSegment(sketch, "E1600", {"start": v(-28.6, 1.48) * mm, "end": v(-28.75, 1.44) * mm});
            skLineSegment(sketch, "E1601", {"start": v(-28.75, 1.44) * mm, "end": v(-28.91, 1.4) * mm});
            skLineSegment(sketch, "E1602", {"start": v(-28.91, 1.4) * mm, "end": v(-29.08, 1.37) * mm});
            skLineSegment(sketch, "E1603", {"start": v(-29.08, 1.37) * mm, "end": v(-29.26, 1.32) * mm});
            skLineSegment(sketch, "E1604", {"start": v(-29.26, 1.32) * mm, "end": v(-29.46, 1.26) * mm});
            skLineSegment(sketch, "E1605", {"start": v(-29.46, 1.26) * mm, "end": v(-29.66, 1.2) * mm});
            skLineSegment(sketch, "E1606", {"start": v(-29.66, 1.2) * mm, "end": v(-29.87, 1.12) * mm});
            skLineSegment(sketch, "E1607", {"start": v(-29.87, 1.12) * mm, "end": v(-30.1, 1.04) * mm});
            skLineSegment(sketch, "E1608", {"start": v(-30.1, 1.04) * mm, "end": v(-30.32, 0.95) * mm});
            skLineSegment(sketch, "E1609", {"start": v(-30.32, 0.95) * mm, "end": v(-30.51, 0.87) * mm});
            skLineSegment(sketch, "E1610", {"start": v(-30.51, 0.87) * mm, "end": v(-30.56, 0) * mm});
            skLineSegment(sketch, "E1611", {"start": v(-30.56, 0) * mm, "end": v(-30.51, -0.87) * mm});
            skLineSegment(sketch, "E1612", {"start": v(-30.51, -0.87) * mm, "end": v(-30.32, -0.95) * mm});
            skLineSegment(sketch, "E1613", {"start": v(-30.32, -0.95) * mm, "end": v(-30.1, -1.04) * mm});
            skLineSegment(sketch, "E1614", {"start": v(-30.1, -1.04) * mm, "end": v(-29.87, -1.12) * mm});
            skLineSegment(sketch, "E1615", {"start": v(-29.87, -1.12) * mm, "end": v(-29.66, -1.2) * mm});
            skLineSegment(sketch, "E1616", {"start": v(-29.66, -1.2) * mm, "end": v(-29.46, -1.26) * mm});
            skLineSegment(sketch, "E1617", {"start": v(-29.46, -1.26) * mm, "end": v(-29.26, -1.32) * mm});
            skLineSegment(sketch, "E1618", {"start": v(-29.26, -1.32) * mm, "end": v(-29.08, -1.37) * mm});
            skLineSegment(sketch, "E1619", {"start": v(-29.08, -1.37) * mm, "end": v(-28.91, -1.4) * mm});
            skLineSegment(sketch, "E1620", {"start": v(-28.91, -1.4) * mm, "end": v(-28.75, -1.44) * mm});
            skLineSegment(sketch, "E1621", {"start": v(-28.75, -1.44) * mm, "end": v(-28.6, -1.48) * mm});
            skLineSegment(sketch, "E1622", {"start": v(-28.6, -1.48) * mm, "end": v(-28.47, -1.5) * mm});
            skLineSegment(sketch, "E1623", {"start": v(-28.47, -1.5) * mm, "end": v(-28.34, -1.52) * mm});
            skLineSegment(sketch, "E1624", {"start": v(-28.34, -1.52) * mm, "end": v(-28.23, -1.54) * mm});
            skLineSegment(sketch, "E1625", {"start": v(-28.23, -1.54) * mm, "end": v(-28.13, -1.55) * mm});
            skLineSegment(sketch, "E1626", {"start": v(-28.13, -1.55) * mm, "end": v(-28.04, -1.56) * mm});
            skLineSegment(sketch, "E1627", {"start": v(-28.04, -1.56) * mm, "end": v(-27.96, -1.56) * mm});
            skLineSegment(sketch, "E1628", {"start": v(-27.96, -1.56) * mm, "end": v(-27.9, -1.57) * mm});
            skLineSegment(sketch, "E1629", {"start": v(-27.9, -1.57) * mm, "end": v(-27.84, -1.57) * mm});
            skLineSegment(sketch, "E1630", {"start": v(-27.84, -1.57) * mm, "end": v(-27.8, -1.57) * mm});
            skLineSegment(sketch, "E1631", {"start": v(-27.8, -1.57) * mm, "end": v(-27.77, -1.57) * mm});
            skLineSegment(sketch, "E1632", {"start": v(-27.77, -1.57) * mm, "end": v(-27.75, -1.57) * mm});
            skLineSegment(sketch, "E1633", {"start": v(-27.75, -1.57) * mm, "end": v(-27.75, -1.57) * mm});
            skLineSegment(sketch, "E1634", {"start": v(-27.75, -1.57) * mm, "end": v(-27.66, -1.56) * mm});
            skLineSegment(sketch, "E1635", {"start": v(-27.66, -1.56) * mm, "end": v(-27.5, -1.55) * mm});
            skLineSegment(sketch, "E1636", {"start": v(-27.5, -1.55) * mm, "end": v(-27.36, -1.55) * mm});
            skLineSegment(sketch, "E1637", {"start": v(-27.36, -1.55) * mm, "end": v(-27.22, -1.56) * mm});
            skLineSegment(sketch, "E1638", {"start": v(-27.22, -1.56) * mm, "end": v(-27.1, -1.57) * mm});
            skLineSegment(sketch, "E1639", {"start": v(-27.1, -1.57) * mm, "end": v(-26.99, -1.58) * mm});
            skLineSegment(sketch, "E1640", {"start": v(-26.99, -1.58) * mm, "end": v(-26.9, -1.6) * mm});
            skLineSegment(sketch, "E1641", {"start": v(-26.9, -1.6) * mm, "end": v(-26.8, -1.63) * mm});
            skLineSegment(sketch, "E1642", {"start": v(-26.8, -1.63) * mm, "end": v(-26.74, -1.66) * mm});
            skLineSegment(sketch, "E1643", {"start": v(-26.74, -1.66) * mm, "end": v(-26.68, -1.7) * mm});
            skLineSegment(sketch, "E1644", {"start": v(-26.68, -1.7) * mm, "end": v(-26.63, -1.73) * mm});
            skLineSegment(sketch, "E1645", {"start": v(-26.63, -1.73) * mm, "end": v(-26.6, -1.77) * mm});
            skLineSegment(sketch, "E1646", {"start": v(-26.6, -1.77) * mm, "end": v(-26.58, -1.8) * mm});
            skLineSegment(sketch, "E1647", {"start": v(-26.58, -1.8) * mm, "end": v(-26.57, -1.85) * mm});
            skLineSegment(sketch, "E1648", {"start": v(-26.57, -1.85) * mm, "end": v(-26.57, -1.95) * mm});
            skLineSegment(sketch, "E1649", {"start": v(-26.57, -1.95) * mm, "end": v(-26.52, -2.5) * mm});
            skLineSegment(sketch, "E1650", {"start": v(-26.52, -2.5) * mm, "end": v(-26.46, -3.06) * mm});
            skLineSegment(sketch, "E1651", {"start": v(-26.46, -3.06) * mm, "end": v(-26.4, -3.62) * mm});
            skLineSegment(sketch, "E1652", {"start": v(-26.4, -3.62) * mm, "end": v(-26.38, -3.72) * mm});
            skLineSegment(sketch, "E1653", {"start": v(-26.38, -3.72) * mm, "end": v(-26.38, -3.76) * mm});
            skLineSegment(sketch, "E1654", {"start": v(-26.38, -3.76) * mm, "end": v(-26.39, -3.8) * mm});
            skLineSegment(sketch, "E1655", {"start": v(-26.39, -3.8) * mm, "end": v(-26.4, -3.85) * mm});
            skLineSegment(sketch, "E1656", {"start": v(-26.4, -3.85) * mm, "end": v(-26.45, -3.9) * mm});
            skLineSegment(sketch, "E1657", {"start": v(-26.45, -3.9) * mm, "end": v(-26.5, -3.94) * mm});
            skLineSegment(sketch, "E1658", {"start": v(-26.5, -3.94) * mm, "end": v(-26.56, -3.98) * mm});
            skLineSegment(sketch, "E1659", {"start": v(-26.56, -3.98) * mm, "end": v(-26.64, -4.02) * mm});
            skLineSegment(sketch, "E1660", {"start": v(-26.64, -4.02) * mm, "end": v(-26.73, -4.06) * mm});
            skLineSegment(sketch, "E1661", {"start": v(-26.73, -4.06) * mm, "end": v(-26.83, -4.1) * mm});
            skLineSegment(sketch, "E1662", {"start": v(-26.83, -4.1) * mm, "end": v(-26.95, -4.14) * mm});
            skLineSegment(sketch, "E1663", {"start": v(-26.95, -4.14) * mm, "end": v(-27.08, -4.17) * mm});
            skLineSegment(sketch, "E1664", {"start": v(-27.08, -4.17) * mm, "end": v(-27.23, -4.2) * mm});
            skLineSegment(sketch, "E1665", {"start": v(-27.23, -4.2) * mm, "end": v(-27.38, -4.22) * mm});
            skLineSegment(sketch, "E1666", {"start": v(-27.38, -4.22) * mm, "end": v(-27.47, -4.23) * mm});
            skLineSegment(sketch, "E1667", {"start": v(-27.47, -4.23) * mm, "end": v(-27.47, -4.23) * mm});
            skLineSegment(sketch, "E1668", {"start": v(-27.47, -4.23) * mm, "end": v(-27.49, -4.24) * mm});
            skLineSegment(sketch, "E1669", {"start": v(-27.49, -4.24) * mm, "end": v(-27.52, -4.24) * mm});
            skLineSegment(sketch, "E1670", {"start": v(-27.52, -4.24) * mm, "end": v(-27.56, -4.25) * mm});
            skLineSegment(sketch, "E1671", {"start": v(-27.56, -4.25) * mm, "end": v(-27.6, -4.27) * mm});
            skLineSegment(sketch, "E1672", {"start": v(-27.6, -4.27) * mm, "end": v(-27.67, -4.28) * mm});
            skLineSegment(sketch, "E1673", {"start": v(-27.67, -4.28) * mm, "end": v(-27.75, -4.3) * mm});
            skLineSegment(sketch, "E1674", {"start": v(-27.75, -4.3) * mm, "end": v(-27.83, -4.33) * mm});
            skLineSegment(sketch, "E1675", {"start": v(-27.83, -4.33) * mm, "end": v(-27.93, -4.37) * mm});
            skLineSegment(sketch, "E1676", {"start": v(-27.93, -4.37) * mm, "end": v(-28.04, -4.4) * mm});
            skLineSegment(sketch, "E1677", {"start": v(-28.04, -4.4) * mm, "end": v(-28.16, -4.45) * mm});
            skLineSegment(sketch, "E1678", {"start": v(-28.16, -4.45) * mm, "end": v(-28.29, -4.5) * mm});
            skLineSegment(sketch, "E1679", {"start": v(-28.29, -4.5) * mm, "end": v(-28.42, -4.57) * mm});
            skLineSegment(sketch, "E1680", {"start": v(-28.42, -4.57) * mm, "end": v(-28.57, -4.63) * mm});
            skLineSegment(sketch, "E1681", {"start": v(-28.57, -4.63) * mm, "end": v(-28.73, -4.71) * mm});
            skLineSegment(sketch, "E1682", {"start": v(-28.73, -4.71) * mm, "end": v(-28.9, -4.8) * mm});
            skLineSegment(sketch, "E1683", {"start": v(-28.9, -4.8) * mm, "end": v(-29.07, -4.9) * mm});
            skLineSegment(sketch, "E1684", {"start": v(-29.07, -4.9) * mm, "end": v(-29.26, -5) * mm});
            skLineSegment(sketch, "E1685", {"start": v(-29.26, -5) * mm, "end": v(-29.45, -5.11) * mm});
            skLineSegment(sketch, "E1686", {"start": v(-29.45, -5.11) * mm, "end": v(-29.65, -5.24) * mm});
            skLineSegment(sketch, "E1687", {"start": v(-29.65, -5.24) * mm, "end": v(-29.86, -5.37) * mm});
            skLineSegment(sketch, "E1688", {"start": v(-29.86, -5.37) * mm, "end": v(-30.03, -5.49) * mm});
            skLineSegment(sketch, "E1689", {"start": v(-30.03, -5.49) * mm, "end": v(-29.89, -6.35) * mm});
            skLineSegment(sketch, "E1690", {"start": v(-29.89, -6.35) * mm, "end": v(-29.66, -7.2) * mm});
            skLineSegment(sketch, "E1691", {"start": v(-29.66, -7.2) * mm, "end": v(-29.46, -7.23) * mm});
            skLineSegment(sketch, "E1692", {"start": v(-29.46, -7.23) * mm, "end": v(-29.22, -7.28) * mm});
            skLineSegment(sketch, "E1693", {"start": v(-29.22, -7.28) * mm, "end": v(-28.98, -7.3) * mm});
            skLineSegment(sketch, "E1694", {"start": v(-28.98, -7.3) * mm, "end": v(-28.76, -7.33) * mm});
            skLineSegment(sketch, "E1695", {"start": v(-28.76, -7.33) * mm, "end": v(-28.55, -7.36) * mm});
            skLineSegment(sketch, "E1696", {"start": v(-28.55, -7.36) * mm, "end": v(-28.35, -7.37) * mm});
            skLineSegment(sketch, "E1697", {"start": v(-28.35, -7.37) * mm, "end": v(-28.16, -7.38) * mm});
            skLineSegment(sketch, "E1698", {"start": v(-28.16, -7.38) * mm, "end": v(-27.99, -7.39) * mm});
            skLineSegment(sketch, "E1699", {"start": v(-27.99, -7.39) * mm, "end": v(-27.82, -7.4) * mm});
            skLineSegment(sketch, "E1700", {"start": v(-27.82, -7.4) * mm, "end": v(-27.67, -7.39) * mm});
            skLineSegment(sketch, "E1701", {"start": v(-27.67, -7.39) * mm, "end": v(-27.53, -7.39) * mm});
            skLineSegment(sketch, "E1702", {"start": v(-27.53, -7.39) * mm, "end": v(-27.4, -7.38) * mm});
            skLineSegment(sketch, "E1703", {"start": v(-27.4, -7.38) * mm, "end": v(-27.3, -7.37) * mm});
            skLineSegment(sketch, "E1704", {"start": v(-27.3, -7.37) * mm, "end": v(-27.2, -7.36) * mm});
            skLineSegment(sketch, "E1705", {"start": v(-27.2, -7.36) * mm, "end": v(-27.1, -7.35) * mm});
            skLineSegment(sketch, "E1706", {"start": v(-27.1, -7.35) * mm, "end": v(-27.02, -7.34) * mm});
            skLineSegment(sketch, "E1707", {"start": v(-27.02, -7.34) * mm, "end": v(-26.96, -7.33) * mm});
            skLineSegment(sketch, "E1708", {"start": v(-26.96, -7.33) * mm, "end": v(-26.9, -7.32) * mm});
            skLineSegment(sketch, "E1709", {"start": v(-26.9, -7.32) * mm, "end": v(-26.86, -7.32) * mm});
            skLineSegment(sketch, "E1710", {"start": v(-26.86, -7.32) * mm, "end": v(-26.84, -7.3) * mm});
            skLineSegment(sketch, "E1711", {"start": v(-26.84, -7.3) * mm, "end": v(-26.82, -7.3) * mm});
            skLineSegment(sketch, "E1712", {"start": v(-26.82, -7.3) * mm, "end": v(-26.82, -7.3) * mm});
            skLineSegment(sketch, "E1713", {"start": v(-26.82, -7.3) * mm, "end": v(-26.73, -7.28) * mm});
            skLineSegment(sketch, "E1714", {"start": v(-26.73, -7.28) * mm, "end": v(-26.58, -7.24) * mm});
            skLineSegment(sketch, "E1715", {"start": v(-26.58, -7.24) * mm, "end": v(-26.44, -7.2) * mm});
            skLineSegment(sketch, "E1716", {"start": v(-26.44, -7.2) * mm, "end": v(-26.3, -7.18) * mm});
            skLineSegment(sketch, "E1717", {"start": v(-26.3, -7.18) * mm, "end": v(-26.18, -7.17) * mm});
            skLineSegment(sketch, "E1718", {"start": v(-26.18, -7.17) * mm, "end": v(-26.07, -7.16) * mm});
            skLineSegment(sketch, "E1719", {"start": v(-26.07, -7.16) * mm, "end": v(-25.97, -7.16) * mm});
            skLineSegment(sketch, "E1720", {"start": v(-25.97, -7.16) * mm, "end": v(-25.88, -7.17) * mm});
            skLineSegment(sketch, "E1721", {"start": v(-25.88, -7.17) * mm, "end": v(-25.8, -7.18) * mm});
            skLineSegment(sketch, "E1722", {"start": v(-25.8, -7.18) * mm, "end": v(-25.74, -7.2) * mm});
            skLineSegment(sketch, "E1723", {"start": v(-25.74, -7.2) * mm, "end": v(-25.69, -7.23) * mm});
            skLineSegment(sketch, "E1724", {"start": v(-25.69, -7.23) * mm, "end": v(-25.65, -7.26) * mm});
            skLineSegment(sketch, "E1725", {"start": v(-25.65, -7.26) * mm, "end": v(-25.62, -7.3) * mm});
            skLineSegment(sketch, "E1726", {"start": v(-25.62, -7.3) * mm, "end": v(-25.6, -7.33) * mm});
            skLineSegment(sketch, "E1727", {"start": v(-25.6, -7.33) * mm, "end": v(-25.58, -7.43) * mm});
            skLineSegment(sketch, "E1728", {"start": v(-25.58, -7.43) * mm, "end": v(-25.42, -7.97) * mm});
            skLineSegment(sketch, "E1729", {"start": v(-25.42, -7.97) * mm, "end": v(-25.25, -8.5) * mm});
            skLineSegment(sketch, "E1730", {"start": v(-25.25, -8.5) * mm, "end": v(-25.06, -9.02) * mm});
            skLineSegment(sketch, "E1731", {"start": v(-25.06, -9.02) * mm, "end": v(-25.03, -9.12) * mm});
            skLineSegment(sketch, "E1732", {"start": v(-25.03, -9.12) * mm, "end": v(-25.02, -9.16) * mm});
            skLineSegment(sketch, "E1733", {"start": v(-25.02, -9.16) * mm, "end": v(-25.02, -9.2) * mm});
            skLineSegment(sketch, "E1734", {"start": v(-25.02, -9.2) * mm, "end": v(-25.03, -9.25) * mm});
            skLineSegment(sketch, "E1735", {"start": v(-25.03, -9.25) * mm, "end": v(-25.06, -9.3) * mm});
            skLineSegment(sketch, "E1736", {"start": v(-25.06, -9.3) * mm, "end": v(-25.1, -9.36) * mm});
            skLineSegment(sketch, "E1737", {"start": v(-25.1, -9.36) * mm, "end": v(-25.15, -9.41) * mm});
            skLineSegment(sketch, "E1738", {"start": v(-25.15, -9.41) * mm, "end": v(-25.22, -9.47) * mm});
            skLineSegment(sketch, "E1739", {"start": v(-25.22, -9.47) * mm, "end": v(-25.3, -9.53) * mm});
            skLineSegment(sketch, "E1740", {"start": v(-25.3, -9.53) * mm, "end": v(-25.4, -9.6) * mm});
            skLineSegment(sketch, "E1741", {"start": v(-25.4, -9.6) * mm, "end": v(-25.5, -9.65) * mm});
            skLineSegment(sketch, "E1742", {"start": v(-25.5, -9.65) * mm, "end": v(-25.62, -9.71) * mm});
            skLineSegment(sketch, "E1743", {"start": v(-25.62, -9.71) * mm, "end": v(-25.76, -9.77) * mm});
            skLineSegment(sketch, "E1744", {"start": v(-25.76, -9.77) * mm, "end": v(-25.9, -9.82) * mm});
            skLineSegment(sketch, "E1745", {"start": v(-25.9, -9.82) * mm, "end": v(-25.99, -9.85) * mm});
            skLineSegment(sketch, "E1746", {"start": v(-25.99, -9.85) * mm, "end": v(-26, -9.85) * mm});
            skLineSegment(sketch, "E1747", {"start": v(-26, -9.85) * mm, "end": v(-26, -9.86) * mm});
            skLineSegment(sketch, "E1748", {"start": v(-26, -9.86) * mm, "end": v(-26.03, -9.87) * mm});
            skLineSegment(sketch, "E1749", {"start": v(-26.03, -9.87) * mm, "end": v(-26.07, -9.89) * mm});
            skLineSegment(sketch, "E1750", {"start": v(-26.07, -9.89) * mm, "end": v(-26.12, -9.91) * mm});
            skLineSegment(sketch, "E1751", {"start": v(-26.12, -9.91) * mm, "end": v(-26.18, -9.94) * mm});
            skLineSegment(sketch, "E1752", {"start": v(-26.18, -9.94) * mm, "end": v(-26.25, -9.98) * mm});
            skLineSegment(sketch, "E1753", {"start": v(-26.25, -9.98) * mm, "end": v(-26.33, -10.03) * mm});
            skLineSegment(sketch, "E1754", {"start": v(-26.33, -10.03) * mm, "end": v(-26.41, -10.08) * mm});
            skLineSegment(sketch, "E1755", {"start": v(-26.41, -10.08) * mm, "end": v(-26.51, -10.14) * mm});
            skLineSegment(sketch, "E1756", {"start": v(-26.51, -10.14) * mm, "end": v(-26.62, -10.2) * mm});
            skLineSegment(sketch, "E1757", {"start": v(-26.62, -10.2) * mm, "end": v(-26.73, -10.29) * mm});
            skLineSegment(sketch, "E1758", {"start": v(-26.73, -10.29) * mm, "end": v(-26.85, -10.38) * mm});
            skLineSegment(sketch, "E1759", {"start": v(-26.85, -10.38) * mm, "end": v(-26.99, -10.47) * mm});
            skLineSegment(sketch, "E1760", {"start": v(-26.99, -10.47) * mm, "end": v(-27.12, -10.58) * mm});
            skLineSegment(sketch, "E1761", {"start": v(-27.12, -10.58) * mm, "end": v(-27.27, -10.7) * mm});
            skLineSegment(sketch, "E1762", {"start": v(-27.27, -10.7) * mm, "end": v(-27.42, -10.83) * mm});
            skLineSegment(sketch, "E1763", {"start": v(-27.42, -10.83) * mm, "end": v(-27.58, -10.97) * mm});
            skLineSegment(sketch, "E1764", {"start": v(-27.58, -10.97) * mm, "end": v(-27.74, -11.12) * mm});
            skLineSegment(sketch, "E1765", {"start": v(-27.74, -11.12) * mm, "end": v(-27.91, -11.29) * mm});
            skLineSegment(sketch, "E1766", {"start": v(-27.91, -11.29) * mm, "end": v(-28.09, -11.47) * mm});
            skLineSegment(sketch, "E1767", {"start": v(-28.09, -11.47) * mm, "end": v(-28.23, -11.61) * mm});
            skLineSegment(sketch, "E1768", {"start": v(-28.23, -11.61) * mm, "end": v(-27.92, -12.43) * mm});
            skLineSegment(sketch, "E1769", {"start": v(-27.92, -12.43) * mm, "end": v(-27.52, -13.2) * mm});
            skLineSegment(sketch, "E1770", {"start": v(-27.52, -13.2) * mm, "end": v(-27.32, -13.2) * mm});
            skLineSegment(sketch, "E1771", {"start": v(-27.32, -13.2) * mm, "end": v(-27.07, -13.2) * mm});
            skLineSegment(sketch, "E1772", {"start": v(-27.07, -13.2) * mm, "end": v(-26.83, -13.17) * mm});
            skLineSegment(sketch, "E1773", {"start": v(-26.83, -13.17) * mm, "end": v(-26.6, -13.15) * mm});
            skLineSegment(sketch, "E1774", {"start": v(-26.6, -13.15) * mm, "end": v(-26.4, -13.13) * mm});
            skLineSegment(sketch, "E1775", {"start": v(-26.4, -13.13) * mm, "end": v(-26.2, -13.1) * mm});
            skLineSegment(sketch, "E1776", {"start": v(-26.2, -13.1) * mm, "end": v(-26.01, -13.08) * mm});
            skLineSegment(sketch, "E1777", {"start": v(-26.01, -13.08) * mm, "end": v(-25.84, -13.05) * mm});
            skLineSegment(sketch, "E1778", {"start": v(-25.84, -13.05) * mm, "end": v(-25.68, -13.01) * mm});
            skLineSegment(sketch, "E1779", {"start": v(-25.68, -13.01) * mm, "end": v(-25.53, -12.98) * mm});
            skLineSegment(sketch, "E1780", {"start": v(-25.53, -12.98) * mm, "end": v(-25.4, -12.95) * mm});
            skLineSegment(sketch, "E1781", {"start": v(-25.4, -12.95) * mm, "end": v(-25.27, -12.92) * mm});
            skLineSegment(sketch, "E1782", {"start": v(-25.27, -12.92) * mm, "end": v(-25.16, -12.89) * mm});
            skLineSegment(sketch, "E1783", {"start": v(-25.16, -12.89) * mm, "end": v(-25.07, -12.86) * mm});
            skLineSegment(sketch, "E1784", {"start": v(-25.07, -12.86) * mm, "end": v(-24.98, -12.83) * mm});
            skLineSegment(sketch, "E1785", {"start": v(-24.98, -12.83) * mm, "end": v(-24.9, -12.8) * mm});
            skLineSegment(sketch, "E1786", {"start": v(-24.9, -12.8) * mm, "end": v(-24.84, -12.78) * mm});
            skLineSegment(sketch, "E1787", {"start": v(-24.84, -12.78) * mm, "end": v(-24.8, -12.76) * mm});
            skLineSegment(sketch, "E1788", {"start": v(-24.8, -12.76) * mm, "end": v(-24.76, -12.74) * mm});
            skLineSegment(sketch, "E1789", {"start": v(-24.76, -12.74) * mm, "end": v(-24.73, -12.73) * mm});
            skLineSegment(sketch, "E1790", {"start": v(-24.73, -12.73) * mm, "end": v(-24.71, -12.72) * mm});
            skLineSegment(sketch, "E1791", {"start": v(-24.71, -12.72) * mm, "end": v(-24.71, -12.72) * mm});
            skLineSegment(sketch, "E1792", {"start": v(-24.71, -12.72) * mm, "end": v(-24.64, -12.68) * mm});
            skLineSegment(sketch, "E1793", {"start": v(-24.64, -12.68) * mm, "end": v(-24.5, -12.6) * mm});
            skLineSegment(sketch, "E1794", {"start": v(-24.5, -12.6) * mm, "end": v(-24.36, -12.54) * mm});
            skLineSegment(sketch, "E1795", {"start": v(-24.36, -12.54) * mm, "end": v(-24.24, -12.5) * mm});
            skLineSegment(sketch, "E1796", {"start": v(-24.24, -12.5) * mm, "end": v(-24.12, -12.45) * mm});
            skLineSegment(sketch, "E1797", {"start": v(-24.12, -12.45) * mm, "end": v(-24.01, -12.42) * mm});
            skLineSegment(sketch, "E1798", {"start": v(-24.01, -12.42) * mm, "end": v(-23.92, -12.4) * mm});
            skLineSegment(sketch, "E1799", {"start": v(-23.92, -12.4) * mm, "end": v(-23.83, -12.4) * mm});
            skLineSegment(sketch, "E1800", {"start": v(-23.83, -12.4) * mm, "end": v(-23.75, -12.4) * mm});
            skLineSegment(sketch, "E1801", {"start": v(-23.75, -12.4) * mm, "end": v(-23.68, -12.4) * mm});
            skLineSegment(sketch, "E1802", {"start": v(-23.68, -12.4) * mm, "end": v(-23.63, -12.41) * mm});
            skLineSegment(sketch, "E1803", {"start": v(-23.63, -12.41) * mm, "end": v(-23.58, -12.43) * mm});
            skLineSegment(sketch, "E1804", {"start": v(-23.58, -12.43) * mm, "end": v(-23.55, -12.46) * mm});
            skLineSegment(sketch, "E1805", {"start": v(-23.55, -12.46) * mm, "end": v(-23.52, -12.5) * mm});
            skLineSegment(sketch, "E1806", {"start": v(-23.52, -12.5) * mm, "end": v(-23.48, -12.59) * mm});
            skLineSegment(sketch, "E1807", {"start": v(-23.48, -12.59) * mm, "end": v(-23.2, -13.08) * mm});
            skLineSegment(sketch, "E1808", {"start": v(-23.2, -13.08) * mm, "end": v(-22.93, -13.56) * mm});
            skLineSegment(sketch, "E1809", {"start": v(-22.93, -13.56) * mm, "end": v(-22.64, -14.04) * mm});
            skLineSegment(sketch, "E1810", {"start": v(-22.64, -14.04) * mm, "end": v(-22.59, -14.12) * mm});
            skLineSegment(sketch, "E1811", {"start": v(-22.59, -14.12) * mm, "end": v(-22.57, -14.16) * mm});
            skLineSegment(sketch, "E1812", {"start": v(-22.57, -14.16) * mm, "end": v(-22.56, -14.2) * mm});
            skLineSegment(sketch, "E1813", {"start": v(-22.56, -14.2) * mm, "end": v(-22.56, -14.25) * mm});
            skLineSegment(sketch, "E1814", {"start": v(-22.56, -14.25) * mm, "end": v(-22.58, -14.31) * mm});
            skLineSegment(sketch, "E1815", {"start": v(-22.58, -14.31) * mm, "end": v(-22.6, -14.37) * mm});
            skLineSegment(sketch, "E1816", {"start": v(-22.6, -14.37) * mm, "end": v(-22.65, -14.44) * mm});
            skLineSegment(sketch, "E1817", {"start": v(-22.65, -14.44) * mm, "end": v(-22.7, -14.5) * mm});
            skLineSegment(sketch, "E1818", {"start": v(-22.7, -14.5) * mm, "end": v(-22.77, -14.58) * mm});
            skLineSegment(sketch, "E1819", {"start": v(-22.77, -14.58) * mm, "end": v(-22.84, -14.66) * mm});
            skLineSegment(sketch, "E1820", {"start": v(-22.84, -14.66) * mm, "end": v(-22.94, -14.74) * mm});
            skLineSegment(sketch, "E1821", {"start": v(-22.94, -14.74) * mm, "end": v(-23.04, -14.83) * mm});
            skLineSegment(sketch, "E1822", {"start": v(-23.04, -14.83) * mm, "end": v(-23.16, -14.91) * mm});
            skLineSegment(sketch, "E1823", {"start": v(-23.16, -14.91) * mm, "end": v(-23.3, -15) * mm});
            skLineSegment(sketch, "E1824", {"start": v(-23.3, -15) * mm, "end": v(-23.37, -15.04) * mm});
            skLineSegment(sketch, "E1825", {"start": v(-23.37, -15.04) * mm, "end": v(-23.37, -15.04) * mm});
            skLineSegment(sketch, "E1826", {"start": v(-23.37, -15.04) * mm, "end": v(-23.39, -15.05) * mm});
            skLineSegment(sketch, "E1827", {"start": v(-23.39, -15.05) * mm, "end": v(-23.41, -15.07) * mm});
            skLineSegment(sketch, "E1828", {"start": v(-23.41, -15.07) * mm, "end": v(-23.45, -15.1) * mm});
            skLineSegment(sketch, "E1829", {"start": v(-23.45, -15.1) * mm, "end": v(-23.49, -15.13) * mm});
            skLineSegment(sketch, "E1830", {"start": v(-23.49, -15.13) * mm, "end": v(-23.54, -15.17) * mm});
            skLineSegment(sketch, "E1831", {"start": v(-23.54, -15.17) * mm, "end": v(-23.6, -15.22) * mm});
            skLineSegment(sketch, "E1832", {"start": v(-23.6, -15.22) * mm, "end": v(-23.67, -15.28) * mm});
            skLineSegment(sketch, "E1833", {"start": v(-23.67, -15.28) * mm, "end": v(-23.74, -15.35) * mm});
            skLineSegment(sketch, "E1834", {"start": v(-23.74, -15.35) * mm, "end": v(-23.82, -15.43) * mm});
            skLineSegment(sketch, "E1835", {"start": v(-23.82, -15.43) * mm, "end": v(-23.91, -15.52) * mm});
            skLineSegment(sketch, "E1836", {"start": v(-23.91, -15.52) * mm, "end": v(-24, -15.62) * mm});
            skLineSegment(sketch, "E1837", {"start": v(-24, -15.62) * mm, "end": v(-24.11, -15.73) * mm});
            skLineSegment(sketch, "E1838", {"start": v(-24.11, -15.73) * mm, "end": v(-24.22, -15.85) * mm});
            skLineSegment(sketch, "E1839", {"start": v(-24.22, -15.85) * mm, "end": v(-24.33, -15.99) * mm});
            skLineSegment(sketch, "E1840", {"start": v(-24.33, -15.99) * mm, "end": v(-24.45, -16.14) * mm});
            skLineSegment(sketch, "E1841", {"start": v(-24.45, -16.14) * mm, "end": v(-24.57, -16.3) * mm});
            skLineSegment(sketch, "E1842", {"start": v(-24.57, -16.3) * mm, "end": v(-24.7, -16.47) * mm});
            skLineSegment(sketch, "E1843", {"start": v(-24.7, -16.47) * mm, "end": v(-24.83, -16.65) * mm});
            skLineSegment(sketch, "E1844", {"start": v(-24.83, -16.65) * mm, "end": v(-24.96, -16.85) * mm});
            skLineSegment(sketch, "E1845", {"start": v(-24.96, -16.85) * mm, "end": v(-25.1, -17.05) * mm});
            skLineSegment(sketch, "E1846", {"start": v(-25.1, -17.05) * mm, "end": v(-25.2, -17.23) * mm});
            skLineSegment(sketch, "E1847", {"start": v(-25.2, -17.23) * mm, "end": v(-24.72, -17.96) * mm});
            skLineSegment(sketch, "E1848", {"start": v(-24.72, -17.96) * mm, "end": v(-24.17, -18.64) * mm});
            skLineSegment(sketch, "E1849", {"start": v(-24.17, -18.64) * mm, "end": v(-23.97, -18.6) * mm});
            skLineSegment(sketch, "E1850", {"start": v(-23.97, -18.6) * mm, "end": v(-23.73, -18.53) * mm});
            skLineSegment(sketch, "E1851", {"start": v(-23.73, -18.53) * mm, "end": v(-23.5, -18.47) * mm});
            skLineSegment(sketch, "E1852", {"start": v(-23.5, -18.47) * mm, "end": v(-23.3, -18.4) * mm});
            skLineSegment(sketch, "E1853", {"start": v(-23.3, -18.4) * mm, "end": v(-23.09, -18.33) * mm});
            skLineSegment(sketch, "E1854", {"start": v(-23.09, -18.33) * mm, "end": v(-22.9, -18.27) * mm});
            skLineSegment(sketch, "E1855", {"start": v(-22.9, -18.27) * mm, "end": v(-22.73, -18.2) * mm});
            skLineSegment(sketch, "E1856", {"start": v(-22.73, -18.2) * mm, "end": v(-22.56, -18.13) * mm});
            skLineSegment(sketch, "E1857", {"start": v(-22.56, -18.13) * mm, "end": v(-22.41, -18.07) * mm});
            skLineSegment(sketch, "E1858", {"start": v(-22.41, -18.07) * mm, "end": v(-22.27, -18) * mm});
            skLineSegment(sketch, "E1859", {"start": v(-22.27, -18) * mm, "end": v(-22.15, -17.95) * mm});
            skLineSegment(sketch, "E1860", {"start": v(-22.15, -17.95) * mm, "end": v(-22.04, -17.89) * mm});
            skLineSegment(sketch, "E1861", {"start": v(-22.04, -17.89) * mm, "end": v(-21.93, -17.84) * mm});
            skLineSegment(sketch, "E1862", {"start": v(-21.93, -17.84) * mm, "end": v(-21.84, -17.79) * mm});
            skLineSegment(sketch, "E1863", {"start": v(-21.84, -17.79) * mm, "end": v(-21.77, -17.74) * mm});
            skLineSegment(sketch, "E1864", {"start": v(-21.77, -17.74) * mm, "end": v(-21.7, -17.7) * mm});
            skLineSegment(sketch, "E1865", {"start": v(-21.7, -17.7) * mm, "end": v(-21.64, -17.66) * mm});
            skLineSegment(sketch, "E1866", {"start": v(-21.64, -17.66) * mm, "end": v(-21.6, -17.63) * mm});
            skLineSegment(sketch, "E1867", {"start": v(-21.6, -17.63) * mm, "end": v(-21.57, -17.6) * mm});
            skLineSegment(sketch, "E1868", {"start": v(-21.57, -17.6) * mm, "end": v(-21.54, -17.6) * mm});
            skLineSegment(sketch, "E1869", {"start": v(-21.54, -17.6) * mm, "end": v(-21.53, -17.58) * mm});
            skLineSegment(sketch, "E1870", {"start": v(-21.53, -17.58) * mm, "end": v(-21.53, -17.58) * mm});
            skLineSegment(sketch, "E1871", {"start": v(-21.53, -17.58) * mm, "end": v(-21.46, -17.52) * mm});
            skLineSegment(sketch, "E1872", {"start": v(-21.46, -17.52) * mm, "end": v(-21.34, -17.42) * mm});
            skLineSegment(sketch, "E1873", {"start": v(-21.34, -17.42) * mm, "end": v(-21.22, -17.33) * mm});
            skLineSegment(sketch, "E1874", {"start": v(-21.22, -17.33) * mm, "end": v(-21.1, -17.26) * mm});
            skLineSegment(sketch, "E1875", {"start": v(-21.1, -17.26) * mm, "end": v(-21, -17.2) * mm});
            skLineSegment(sketch, "E1876", {"start": v(-21, -17.2) * mm, "end": v(-20.9, -17.14) * mm});
            skLineSegment(sketch, "E1877", {"start": v(-20.9, -17.14) * mm, "end": v(-20.81, -17.1) * mm});
            skLineSegment(sketch, "E1878", {"start": v(-20.81, -17.1) * mm, "end": v(-20.73, -17.08) * mm});
            skLineSegment(sketch, "E1879", {"start": v(-20.73, -17.08) * mm, "end": v(-20.65, -17.06) * mm});
            skLineSegment(sketch, "E1880", {"start": v(-20.65, -17.06) * mm, "end": v(-20.59, -17.05) * mm});
            skLineSegment(sketch, "E1881", {"start": v(-20.59, -17.05) * mm, "end": v(-20.53, -17.05) * mm});
            skLineSegment(sketch, "E1882", {"start": v(-20.53, -17.05) * mm, "end": v(-20.48, -17.06) * mm});
            skLineSegment(sketch, "E1883", {"start": v(-20.48, -17.06) * mm, "end": v(-20.44, -17.09) * mm});
            skLineSegment(sketch, "E1884", {"start": v(-20.44, -17.09) * mm, "end": v(-20.41, -17.12) * mm});
            skLineSegment(sketch, "E1885", {"start": v(-20.41, -17.12) * mm, "end": v(-20.35, -17.2) * mm});
            skLineSegment(sketch, "E1886", {"start": v(-20.35, -17.2) * mm, "end": v(-19.98, -17.62) * mm});
            skLineSegment(sketch, "E1887", {"start": v(-19.98, -17.62) * mm, "end": v(-19.6, -18.03) * mm});
            skLineSegment(sketch, "E1888", {"start": v(-19.6, -18.03) * mm, "end": v(-19.23, -18.44) * mm});
            skLineSegment(sketch, "E1889", {"start": v(-19.23, -18.44) * mm, "end": v(-19.16, -18.51) * mm});
            skLineSegment(sketch, "E1890", {"start": v(-19.16, -18.51) * mm, "end": v(-19.13, -18.54) * mm});
            skLineSegment(sketch, "E1891", {"start": v(-19.13, -18.54) * mm, "end": v(-19.11, -18.58) * mm});
            skLineSegment(sketch, "E1892", {"start": v(-19.11, -18.58) * mm, "end": v(-19.1, -18.63) * mm});
            skLineSegment(sketch, "E1893", {"start": v(-19.1, -18.63) * mm, "end": v(-19.1, -18.7) * mm});
            skLineSegment(sketch, "E1894", {"start": v(-19.1, -18.7) * mm, "end": v(-19.12, -18.76) * mm});
            skLineSegment(sketch, "E1895", {"start": v(-19.12, -18.76) * mm, "end": v(-19.15, -18.83) * mm});
            skLineSegment(sketch, "E1896", {"start": v(-19.15, -18.83) * mm, "end": v(-19.19, -18.91) * mm});
            skLineSegment(sketch, "E1897", {"start": v(-19.19, -18.91) * mm, "end": v(-19.24, -19) * mm});
            skLineSegment(sketch, "E1898", {"start": v(-19.24, -19) * mm, "end": v(-19.3, -19.1) * mm});
            skLineSegment(sketch, "E1899", {"start": v(-19.3, -19.1) * mm, "end": v(-19.37, -19.19) * mm});
            skLineSegment(sketch, "E1900", {"start": v(-19.37, -19.19) * mm, "end": v(-19.46, -19.3) * mm});
            skLineSegment(sketch, "E1901", {"start": v(-19.46, -19.3) * mm, "end": v(-19.56, -19.4) * mm});
            skLineSegment(sketch, "E1902", {"start": v(-19.56, -19.4) * mm, "end": v(-19.67, -19.51) * mm});
            skLineSegment(sketch, "E1903", {"start": v(-19.67, -19.51) * mm, "end": v(-19.73, -19.57) * mm});
            skLineSegment(sketch, "E1904", {"start": v(-19.73, -19.57) * mm, "end": v(-19.74, -19.57) * mm});
            skLineSegment(sketch, "E1905", {"start": v(-19.74, -19.57) * mm, "end": v(-19.75, -19.59) * mm});
            skLineSegment(sketch, "E1906", {"start": v(-19.75, -19.59) * mm, "end": v(-19.77, -19.6) * mm});
            skLineSegment(sketch, "E1907", {"start": v(-19.77, -19.6) * mm, "end": v(-19.8, -19.64) * mm});
            skLineSegment(sketch, "E1908", {"start": v(-19.8, -19.64) * mm, "end": v(-19.83, -19.68) * mm});
            skLineSegment(sketch, "E1909", {"start": v(-19.83, -19.68) * mm, "end": v(-19.87, -19.73) * mm});
            skLineSegment(sketch, "E1910", {"start": v(-19.87, -19.73) * mm, "end": v(-19.92, -19.8) * mm});
            skLineSegment(sketch, "E1911", {"start": v(-19.92, -19.8) * mm, "end": v(-19.97, -19.87) * mm});
            skLineSegment(sketch, "E1912", {"start": v(-19.97, -19.87) * mm, "end": v(-20.03, -19.95) * mm});
            skLineSegment(sketch, "E1913", {"start": v(-20.03, -19.95) * mm, "end": v(-20.1, -20.04) * mm});
            skLineSegment(sketch, "E1914", {"start": v(-20.1, -20.04) * mm, "end": v(-20.16, -20.15) * mm});
            skLineSegment(sketch, "E1915", {"start": v(-20.16, -20.15) * mm, "end": v(-20.24, -20.27) * mm});
            skLineSegment(sketch, "E1916", {"start": v(-20.24, -20.27) * mm, "end": v(-20.31, -20.4) * mm});
            skLineSegment(sketch, "E1917", {"start": v(-20.31, -20.4) * mm, "end": v(-20.4, -20.54) * mm});
            skLineSegment(sketch, "E1918", {"start": v(-20.4, -20.54) * mm, "end": v(-20.47, -20.7) * mm});
            skLineSegment(sketch, "E1919", {"start": v(-20.47, -20.7) * mm, "end": v(-20.56, -20.87) * mm});
            skLineSegment(sketch, "E1920", {"start": v(-20.56, -20.87) * mm, "end": v(-20.65, -21.05) * mm});
            skLineSegment(sketch, "E1921", {"start": v(-20.65, -21.05) * mm, "end": v(-20.73, -21.24) * mm});
            skLineSegment(sketch, "E1922", {"start": v(-20.73, -21.24) * mm, "end": v(-20.82, -21.45) * mm});
            skLineSegment(sketch, "E1923", {"start": v(-20.82, -21.45) * mm, "end": v(-20.9, -21.67) * mm});
            skLineSegment(sketch, "E1924", {"start": v(-20.9, -21.67) * mm, "end": v(-21, -21.9) * mm});
            skLineSegment(sketch, "E1925", {"start": v(-21, -21.9) * mm, "end": v(-21.07, -22.1) * mm});
            skLineSegment(sketch, "E1926", {"start": v(-21.07, -22.1) * mm, "end": v(-20.45, -22.7) * mm});
            skLineSegment(sketch, "E1927", {"start": v(-20.45, -22.7) * mm, "end": v(-19.77, -23.26) * mm});
            skLineSegment(sketch, "E1928", {"start": v(-19.77, -23.26) * mm, "end": v(-19.58, -23.17) * mm});
            skLineSegment(sketch, "E1929", {"start": v(-19.58, -23.17) * mm, "end": v(-19.36, -23.06) * mm});
            skLineSegment(sketch, "E1930", {"start": v(-19.36, -23.06) * mm, "end": v(-19.15, -22.95) * mm});
            skLineSegment(sketch, "E1931", {"start": v(-19.15, -22.95) * mm, "end": v(-18.96, -22.84) * mm});
            skLineSegment(sketch, "E1932", {"start": v(-18.96, -22.84) * mm, "end": v(-18.77, -22.73) * mm});
            skLineSegment(sketch, "E1933", {"start": v(-18.77, -22.73) * mm, "end": v(-18.6, -22.63) * mm});
            skLineSegment(sketch, "E1934", {"start": v(-18.6, -22.63) * mm, "end": v(-18.45, -22.53) * mm});
            skLineSegment(sketch, "E1935", {"start": v(-18.45, -22.53) * mm, "end": v(-18.3, -22.43) * mm});
            skLineSegment(sketch, "E1936", {"start": v(-18.3, -22.43) * mm, "end": v(-18.17, -22.33) * mm});
            skLineSegment(sketch, "E1937", {"start": v(-18.17, -22.33) * mm, "end": v(-18.04, -22.24) * mm});
            skLineSegment(sketch, "E1938", {"start": v(-18.04, -22.24) * mm, "end": v(-17.93, -22.16) * mm});
            skLineSegment(sketch, "E1939", {"start": v(-17.93, -22.16) * mm, "end": v(-17.83, -22.08) * mm});
            skLineSegment(sketch, "E1940", {"start": v(-17.83, -22.08) * mm, "end": v(-17.75, -22) * mm});
            skLineSegment(sketch, "E1941", {"start": v(-17.75, -22) * mm, "end": v(-17.67, -21.94) * mm});
            skLineSegment(sketch, "E1942", {"start": v(-17.67, -21.94) * mm, "end": v(-17.6, -21.88) * mm});
            skLineSegment(sketch, "E1943", {"start": v(-17.6, -21.88) * mm, "end": v(-17.55, -21.82) * mm});
            skLineSegment(sketch, "E1944", {"start": v(-17.55, -21.82) * mm, "end": v(-17.5, -21.78) * mm});
            skLineSegment(sketch, "E1945", {"start": v(-17.5, -21.78) * mm, "end": v(-17.46, -21.74) * mm});
            skLineSegment(sketch, "E1946", {"start": v(-17.46, -21.74) * mm, "end": v(-17.43, -21.7) * mm});
            skLineSegment(sketch, "E1947", {"start": v(-17.43, -21.7) * mm, "end": v(-17.41, -21.69) * mm});
            skLineSegment(sketch, "E1948", {"start": v(-17.41, -21.69) * mm, "end": v(-17.4, -21.67) * mm});
            skLineSegment(sketch, "E1949", {"start": v(-17.4, -21.67) * mm, "end": v(-17.4, -21.67) * mm});
            skLineSegment(sketch, "E1950", {"start": v(-17.4, -21.67) * mm, "end": v(-17.35, -21.6) * mm});
            skLineSegment(sketch, "E1951", {"start": v(-17.35, -21.6) * mm, "end": v(-17.25, -21.48) * mm});
            skLineSegment(sketch, "E1952", {"start": v(-17.25, -21.48) * mm, "end": v(-17.15, -21.37) * mm});
            skLineSegment(sketch, "E1953", {"start": v(-17.15, -21.37) * mm, "end": v(-17.06, -21.27) * mm});
            skLineSegment(sketch, "E1954", {"start": v(-17.06, -21.27) * mm, "end": v(-16.97, -21.19) * mm});
            skLineSegment(sketch, "E1955", {"start": v(-16.97, -21.19) * mm, "end": v(-16.88, -21.12) * mm});
            skLineSegment(sketch, "E1956", {"start": v(-16.88, -21.12) * mm, "end": v(-16.8, -21.06) * mm});
            skLineSegment(sketch, "E1957", {"start": v(-16.8, -21.06) * mm, "end": v(-16.73, -21.01) * mm});
            skLineSegment(sketch, "E1958", {"start": v(-16.73, -21.01) * mm, "end": v(-16.66, -20.98) * mm});
            skLineSegment(sketch, "E1959", {"start": v(-16.66, -20.98) * mm, "end": v(-16.6, -20.96) * mm});
            skLineSegment(sketch, "E1960", {"start": v(-16.6, -20.96) * mm, "end": v(-16.54, -20.95) * mm});
            skLineSegment(sketch, "E1961", {"start": v(-16.54, -20.95) * mm, "end": v(-16.48, -20.95) * mm});
            skLineSegment(sketch, "E1962", {"start": v(-16.48, -20.95) * mm, "end": v(-16.44, -20.96) * mm});
            skLineSegment(sketch, "E1963", {"start": v(-16.44, -20.96) * mm, "end": v(-16.4, -20.99) * mm});
            skLineSegment(sketch, "E1964", {"start": v(-16.4, -20.99) * mm, "end": v(-16.33, -21.05) * mm});
            skLineSegment(sketch, "E1965", {"start": v(-16.33, -21.05) * mm, "end": v(-15.88, -21.39) * mm});
            skLineSegment(sketch, "E1966", {"start": v(-15.88, -21.39) * mm, "end": v(-15.43, -21.71) * mm});
            skLineSegment(sketch, "E1967", {"start": v(-15.43, -21.71) * mm, "end": v(-14.97, -22.03) * mm});
            skLineSegment(sketch, "E1968", {"start": v(-14.97, -22.03) * mm, "end": v(-14.89, -22.09) * mm});
            skLineSegment(sketch, "E1969", {"start": v(-14.89, -22.09) * mm, "end": v(-14.86, -22.11) * mm});
            skLineSegment(sketch, "E1970", {"start": v(-14.86, -22.11) * mm, "end": v(-14.83, -22.15) * mm});
            skLineSegment(sketch, "E1971", {"start": v(-14.83, -22.15) * mm, "end": v(-14.81, -22.2) * mm});
            skLineSegment(sketch, "E1972", {"start": v(-14.81, -22.2) * mm, "end": v(-14.8, -22.26) * mm});
            skLineSegment(sketch, "E1973", {"start": v(-14.8, -22.26) * mm, "end": v(-14.8, -22.32) * mm});
            skLineSegment(sketch, "E1974", {"start": v(-14.8, -22.32) * mm, "end": v(-14.81, -22.4) * mm});
            skLineSegment(sketch, "E1975", {"start": v(-14.81, -22.4) * mm, "end": v(-14.83, -22.49) * mm});
            skLineSegment(sketch, "E1976", {"start": v(-14.83, -22.49) * mm, "end": v(-14.87, -22.58) * mm});
            skLineSegment(sketch, "E1977", {"start": v(-14.87, -22.58) * mm, "end": v(-14.9, -22.69) * mm});
            skLineSegment(sketch, "E1978", {"start": v(-14.9, -22.69) * mm, "end": v(-14.96, -22.8) * mm});
            skLineSegment(sketch, "E1979", {"start": v(-14.96, -22.8) * mm, "end": v(-15.02, -22.92) * mm});
            skLineSegment(sketch, "E1980", {"start": v(-15.02, -22.92) * mm, "end": v(-15.1, -23.04) * mm});
            skLineSegment(sketch, "E1981", {"start": v(-15.1, -23.04) * mm, "end": v(-15.18, -23.18) * mm});
            skLineSegment(sketch, "E1982", {"start": v(-15.18, -23.18) * mm, "end": v(-15.23, -23.25) * mm});
            skLineSegment(sketch, "E1983", {"start": v(-15.23, -23.25) * mm, "end": v(-15.23, -23.25) * mm});
            skLineSegment(sketch, "E1984", {"start": v(-15.23, -23.25) * mm, "end": v(-15.24, -23.26) * mm});
            skLineSegment(sketch, "E1985", {"start": v(-15.24, -23.26) * mm, "end": v(-15.26, -23.29) * mm});
            skLineSegment(sketch, "E1986", {"start": v(-15.26, -23.29) * mm, "end": v(-15.28, -23.32) * mm});
            skLineSegment(sketch, "E1987", {"start": v(-15.28, -23.32) * mm, "end": v(-15.3, -23.37) * mm});
            skLineSegment(sketch, "E1988", {"start": v(-15.3, -23.37) * mm, "end": v(-15.33, -23.43) * mm});
            skLineSegment(sketch, "E1989", {"start": v(-15.33, -23.43) * mm, "end": v(-15.37, -23.5) * mm});
            skLineSegment(sketch, "E1990", {"start": v(-15.37, -23.5) * mm, "end": v(-15.4, -23.58) * mm});
            skLineSegment(sketch, "E1991", {"start": v(-15.4, -23.58) * mm, "end": v(-15.45, -23.68) * mm});
            skLineSegment(sketch, "E1992", {"start": v(-15.45, -23.68) * mm, "end": v(-15.49, -23.78) * mm});
            skLineSegment(sketch, "E1993", {"start": v(-15.49, -23.78) * mm, "end": v(-15.53, -23.9) * mm});
            skLineSegment(sketch, "E1994", {"start": v(-15.53, -23.9) * mm, "end": v(-15.58, -24.03) * mm});
            skLineSegment(sketch, "E1995", {"start": v(-15.58, -24.03) * mm, "end": v(-15.63, -24.18) * mm});
            skLineSegment(sketch, "E1996", {"start": v(-15.63, -24.18) * mm, "end": v(-15.68, -24.33) * mm});
            skLineSegment(sketch, "E1997", {"start": v(-15.68, -24.33) * mm, "end": v(-15.72, -24.5) * mm});
            skLineSegment(sketch, "E1998", {"start": v(-15.72, -24.5) * mm, "end": v(-15.77, -24.69) * mm});
            skLineSegment(sketch, "E1999", {"start": v(-15.77, -24.69) * mm, "end": v(-15.82, -24.88) * mm});
            skLineSegment(sketch, "E2000", {"start": v(-15.82, -24.88) * mm, "end": v(-15.86, -25.09) * mm});
            skLineSegment(sketch, "E2001", {"start": v(-15.86, -25.09) * mm, "end": v(-15.9, -25.3) * mm});
            skLineSegment(sketch, "E2002", {"start": v(-15.9, -25.3) * mm, "end": v(-15.95, -25.54) * mm});
            skLineSegment(sketch, "E2003", {"start": v(-15.95, -25.54) * mm, "end": v(-15.99, -25.79) * mm});
            skLineSegment(sketch, "E2004", {"start": v(-15.99, -25.79) * mm, "end": v(-16.01, -25.99) * mm});
            skLineSegment(sketch, "E2005", {"start": v(-16.01, -25.99) * mm, "end": v(-15.28, -26.46) * mm});
            skLineSegment(sketch, "E2006", {"start": v(-15.28, -26.46) * mm, "end": v(-14.5, -26.86) * mm});
            skLineSegment(sketch, "E2007", {"start": v(-14.5, -26.86) * mm, "end": v(-14.34, -26.74) * mm});
            skLineSegment(sketch, "E2008", {"start": v(-14.34, -26.74) * mm, "end": v(-14.14, -26.58) * mm});
            skLineSegment(sketch, "E2009", {"start": v(-14.14, -26.58) * mm, "end": v(-13.96, -26.43) * mm});
            skLineSegment(sketch, "E2010", {"start": v(-13.96, -26.43) * mm, "end": v(-13.8, -26.28) * mm});
            skLineSegment(sketch, "E2011", {"start": v(-13.8, -26.28) * mm, "end": v(-13.64, -26.14) * mm});
            skLineSegment(sketch, "E2012", {"start": v(-13.64, -26.14) * mm, "end": v(-13.5, -26) * mm});
            skLineSegment(sketch, "E2013", {"start": v(-13.5, -26) * mm, "end": v(-13.36, -25.87) * mm});
            skLineSegment(sketch, "E2014", {"start": v(-13.36, -25.87) * mm, "end": v(-13.24, -25.74) * mm});
            skLineSegment(sketch, "E2015", {"start": v(-13.24, -25.74) * mm, "end": v(-13.13, -25.62) * mm});
            skLineSegment(sketch, "E2016", {"start": v(-13.13, -25.62) * mm, "end": v(-13.02, -25.5) * mm});
            skLineSegment(sketch, "E2017", {"start": v(-13.02, -25.5) * mm, "end": v(-12.93, -25.4) * mm});
            skLineSegment(sketch, "E2018", {"start": v(-12.93, -25.4) * mm, "end": v(-12.85, -25.3) * mm});
            skLineSegment(sketch, "E2019", {"start": v(-12.85, -25.3) * mm, "end": v(-12.78, -25.22) * mm});
            skLineSegment(sketch, "E2020", {"start": v(-12.78, -25.22) * mm, "end": v(-12.72, -25.13) * mm});
            skLineSegment(sketch, "E2021", {"start": v(-12.72, -25.13) * mm, "end": v(-12.67, -25.06) * mm});
            skLineSegment(sketch, "E2022", {"start": v(-12.67, -25.06) * mm, "end": v(-12.63, -25) * mm});
            skLineSegment(sketch, "E2023", {"start": v(-12.63, -25) * mm, "end": v(-12.59, -24.94) * mm});
            skLineSegment(sketch, "E2024", {"start": v(-12.59, -24.94) * mm, "end": v(-12.56, -24.9) * mm});
            skLineSegment(sketch, "E2025", {"start": v(-12.56, -24.9) * mm, "end": v(-12.54, -24.86) * mm});
            skLineSegment(sketch, "E2026", {"start": v(-12.54, -24.86) * mm, "end": v(-12.52, -24.83) * mm});
            skLineSegment(sketch, "E2027", {"start": v(-12.52, -24.83) * mm, "end": v(-12.52, -24.82) * mm});
            skLineSegment(sketch, "E2028", {"start": v(-12.52, -24.82) * mm, "end": v(-12.52, -24.82) * mm});
            skLineSegment(sketch, "E2029", {"start": v(-12.52, -24.82) * mm, "end": v(-12.48, -24.74) * mm});
            skLineSegment(sketch, "E2030", {"start": v(-12.48, -24.74) * mm, "end": v(-12.4, -24.6) * mm});
            skLineSegment(sketch, "E2031", {"start": v(-12.4, -24.6) * mm, "end": v(-12.34, -24.47) * mm});
            skLineSegment(sketch, "E2032", {"start": v(-12.34, -24.47) * mm, "end": v(-12.26, -24.35) * mm});
            skLineSegment(sketch, "E2033", {"start": v(-12.26, -24.35) * mm, "end": v(-12.2, -24.25) * mm});
            skLineSegment(sketch, "E2034", {"start": v(-12.2, -24.25) * mm, "end": v(-12.12, -24.17) * mm});
            skLineSegment(sketch, "E2035", {"start": v(-12.12, -24.17) * mm, "end": v(-12.06, -24.1) * mm});
            skLineSegment(sketch, "E2036", {"start": v(-12.06, -24.1) * mm, "end": v(-12, -24.03) * mm});
            skLineSegment(sketch, "E2037", {"start": v(-12, -24.03) * mm, "end": v(-11.93, -23.98) * mm});
            skLineSegment(sketch, "E2038", {"start": v(-11.93, -23.98) * mm, "end": v(-11.87, -23.95) * mm});
            skLineSegment(sketch, "E2039", {"start": v(-11.87, -23.95) * mm, "end": v(-11.82, -23.93) * mm});
            skLineSegment(sketch, "E2040", {"start": v(-11.82, -23.93) * mm, "end": v(-11.77, -23.92) * mm});
            skLineSegment(sketch, "E2041", {"start": v(-11.77, -23.92) * mm, "end": v(-11.72, -23.92) * mm});
            skLineSegment(sketch, "E2042", {"start": v(-11.72, -23.92) * mm, "end": v(-11.69, -23.94) * mm});
            skLineSegment(sketch, "E2043", {"start": v(-11.69, -23.94) * mm, "end": v(-11.6, -23.98) * mm});
            skLineSegment(sketch, "E2044", {"start": v(-11.6, -23.98) * mm, "end": v(-11.09, -24.22) * mm});
            skLineSegment(sketch, "E2045", {"start": v(-11.09, -24.22) * mm, "end": v(-10.58, -24.45) * mm});
            skLineSegment(sketch, "E2046", {"start": v(-10.58, -24.45) * mm, "end": v(-10.07, -24.66) * mm});
            skLineSegment(sketch, "E2047", {"start": v(-10.07, -24.66) * mm, "end": v(-9.97, -24.7) * mm});
            skLineSegment(sketch, "E2048", {"start": v(-9.97, -24.7) * mm, "end": v(-9.93, -24.72) * mm});
            skLineSegment(sketch, "E2049", {"start": v(-9.93, -24.72) * mm, "end": v(-9.9, -24.75) * mm});
            skLineSegment(sketch, "E2050", {"start": v(-9.9, -24.75) * mm, "end": v(-9.87, -24.8) * mm});
            skLineSegment(sketch, "E2051", {"start": v(-9.87, -24.8) * mm, "end": v(-9.85, -24.85) * mm});
            skLineSegment(sketch, "E2052", {"start": v(-9.85, -24.85) * mm, "end": v(-9.84, -24.91) * mm});
            skLineSegment(sketch, "E2053", {"start": v(-9.84, -24.91) * mm, "end": v(-9.83, -25) * mm});
            skLineSegment(sketch, "E2054", {"start": v(-9.83, -25) * mm, "end": v(-9.84, -25.08) * mm});
            skLineSegment(sketch, "E2055", {"start": v(-9.84, -25.08) * mm, "end": v(-9.85, -25.18) * mm});
            skLineSegment(sketch, "E2056", {"start": v(-9.85, -25.18) * mm, "end": v(-9.86, -25.29) * mm});
            skLineSegment(sketch, "E2057", {"start": v(-9.86, -25.29) * mm, "end": v(-9.9, -25.4) * mm});
            skLineSegment(sketch, "E2058", {"start": v(-9.9, -25.4) * mm, "end": v(-9.93, -25.54) * mm});
            skLineSegment(sketch, "E2059", {"start": v(-9.93, -25.54) * mm, "end": v(-9.98, -25.68) * mm});
            skLineSegment(sketch, "E2060", {"start": v(-9.98, -25.68) * mm, "end": v(-10.03, -25.83) * mm});
            skLineSegment(sketch, "E2061", {"start": v(-10.03, -25.83) * mm, "end": v(-10.07, -25.9) * mm});
            skLineSegment(sketch, "E2062", {"start": v(-10.07, -25.9) * mm, "end": v(-10.07, -25.9) * mm});
            skLineSegment(sketch, "E2063", {"start": v(-10.07, -25.9) * mm, "end": v(-10.07, -25.92) * mm});
            skLineSegment(sketch, "E2064", {"start": v(-10.07, -25.92) * mm, "end": v(-10.08, -25.95) * mm});
            skLineSegment(sketch, "E2065", {"start": v(-10.08, -25.95) * mm, "end": v(-10.1, -26) * mm});
            skLineSegment(sketch, "E2066", {"start": v(-10.1, -26) * mm, "end": v(-10.11, -26.04) * mm});
            skLineSegment(sketch, "E2067", {"start": v(-10.11, -26.04) * mm, "end": v(-10.13, -26.1) * mm});
            skLineSegment(sketch, "E2068", {"start": v(-10.13, -26.1) * mm, "end": v(-10.15, -26.18) * mm});
            skLineSegment(sketch, "E2069", {"start": v(-10.15, -26.18) * mm, "end": v(-10.16, -26.27) * mm});
            skLineSegment(sketch, "E2070", {"start": v(-10.16, -26.27) * mm, "end": v(-10.18, -26.37) * mm});
            skLineSegment(sketch, "E2071", {"start": v(-10.18, -26.37) * mm, "end": v(-10.2, -26.49) * mm});
            skLineSegment(sketch, "E2072", {"start": v(-10.2, -26.49) * mm, "end": v(-10.22, -26.61) * mm});
            skLineSegment(sketch, "E2073", {"start": v(-10.22, -26.61) * mm, "end": v(-10.24, -26.75) * mm});
            skLineSegment(sketch, "E2074", {"start": v(-10.24, -26.75) * mm, "end": v(-10.26, -26.9) * mm});
            skLineSegment(sketch, "E2075", {"start": v(-10.26, -26.9) * mm, "end": v(-10.27, -27.06) * mm});
            skLineSegment(sketch, "E2076", {"start": v(-10.27, -27.06) * mm, "end": v(-10.29, -27.24) * mm});
            skLineSegment(sketch, "E2077", {"start": v(-10.29, -27.24) * mm, "end": v(-10.3, -27.42) * mm});
            skLineSegment(sketch, "E2078", {"start": v(-10.3, -27.42) * mm, "end": v(-10.3, -27.62) * mm});
            skLineSegment(sketch, "E2079", {"start": v(-10.3, -27.62) * mm, "end": v(-10.3, -27.84) * mm});
            skLineSegment(sketch, "E2080", {"start": v(-10.3, -27.84) * mm, "end": v(-10.3, -28.06) * mm});
            skLineSegment(sketch, "E2081", {"start": v(-10.3, -28.06) * mm, "end": v(-10.29, -28.3) * mm});
            skLineSegment(sketch, "E2082", {"start": v(-10.29, -28.3) * mm, "end": v(-10.28, -28.55) * mm});
            skLineSegment(sketch, "E2083", {"start": v(-10.28, -28.55) * mm, "end": v(-10.26, -28.75) * mm});
            skLineSegment(sketch, "E2084", {"start": v(-10.26, -28.75) * mm, "end": v(-9.44, -29.06) * mm});
            skLineSegment(sketch, "E2085", {"start": v(-9.44, -29.06) * mm, "end": v(-8.6, -29.29) * mm});
            skLineSegment(sketch, "E2086", {"start": v(-8.6, -29.29) * mm, "end": v(-8.47, -29.13) * mm});
            skLineSegment(sketch, "E2087", {"start": v(-8.47, -29.13) * mm, "end": v(-8.3, -28.94) * mm});
            skLineSegment(sketch, "E2088", {"start": v(-8.3, -28.94) * mm, "end": v(-8.16, -28.76) * mm});
            skLineSegment(sketch, "E2089", {"start": v(-8.16, -28.76) * mm, "end": v(-8.03, -28.58) * mm});
            skLineSegment(sketch, "E2090", {"start": v(-8.03, -28.58) * mm, "end": v(-7.9, -28.4) * mm});
            skLineSegment(sketch, "E2091", {"start": v(-7.9, -28.4) * mm, "end": v(-7.8, -28.24) * mm});
            skLineSegment(sketch, "E2092", {"start": v(-7.8, -28.24) * mm, "end": v(-7.69, -28.08) * mm});
            skLineSegment(sketch, "E2093", {"start": v(-7.69, -28.08) * mm, "end": v(-7.6, -27.93) * mm});
            skLineSegment(sketch, "E2094", {"start": v(-7.6, -27.93) * mm, "end": v(-7.51, -27.8) * mm});
            skLineSegment(sketch, "E2095", {"start": v(-7.51, -27.8) * mm, "end": v(-7.44, -27.66) * mm});
            skLineSegment(sketch, "E2096", {"start": v(-7.44, -27.66) * mm, "end": v(-7.37, -27.54) * mm});
            skLineSegment(sketch, "E2097", {"start": v(-7.37, -27.54) * mm, "end": v(-7.31, -27.43) * mm});
            skLineSegment(sketch, "E2098", {"start": v(-7.31, -27.43) * mm, "end": v(-7.26, -27.32) * mm});
            skLineSegment(sketch, "E2099", {"start": v(-7.26, -27.32) * mm, "end": v(-7.22, -27.23) * mm});
            skLineSegment(sketch, "E2100", {"start": v(-7.22, -27.23) * mm, "end": v(-7.18, -27.15) * mm});
            skLineSegment(sketch, "E2101", {"start": v(-7.18, -27.15) * mm, "end": v(-7.15, -27.07) * mm});
            skLineSegment(sketch, "E2102", {"start": v(-7.15, -27.07) * mm, "end": v(-7.13, -27.01) * mm});
            skLineSegment(sketch, "E2103", {"start": v(-7.13, -27.01) * mm, "end": v(-7.11, -26.96) * mm});
            skLineSegment(sketch, "E2104", {"start": v(-7.11, -26.96) * mm, "end": v(-7.1, -26.92) * mm});
            skLineSegment(sketch, "E2105", {"start": v(-7.1, -26.92) * mm, "end": v(-7.09, -26.9) * mm});
            skLineSegment(sketch, "E2106", {"start": v(-7.09, -26.9) * mm, "end": v(-7.08, -26.88) * mm});
            skLineSegment(sketch, "E2107", {"start": v(-7.08, -26.88) * mm, "end": v(-7.08, -26.88) * mm});
            skLineSegment(sketch, "E2108", {"start": v(-7.08, -26.88) * mm, "end": v(-7.06, -26.8) * mm});
            skLineSegment(sketch, "E2109", {"start": v(-7.06, -26.8) * mm, "end": v(-7.02, -26.64) * mm});
            skLineSegment(sketch, "E2110", {"start": v(-7.02, -26.64) * mm, "end": v(-6.98, -26.5) * mm});
            skLineSegment(sketch, "E2111", {"start": v(-6.98, -26.5) * mm, "end": v(-6.93, -26.37) * mm});
            skLineSegment(sketch, "E2112", {"start": v(-6.93, -26.37) * mm, "end": v(-6.88, -26.26) * mm});
            skLineSegment(sketch, "E2113", {"start": v(-6.88, -26.26) * mm, "end": v(-6.84, -26.16) * mm});
            skLineSegment(sketch, "E2114", {"start": v(-6.84, -26.16) * mm, "end": v(-6.78, -26.07) * mm});
            skLineSegment(sketch, "E2115", {"start": v(-6.78, -26.07) * mm, "end": v(-6.73, -26) * mm});
            skLineSegment(sketch, "E2116", {"start": v(-6.73, -26) * mm, "end": v(-6.68, -25.94) * mm});
            skLineSegment(sketch, "E2117", {"start": v(-6.68, -25.94) * mm, "end": v(-6.63, -25.9) * mm});
            skLineSegment(sketch, "E2118", {"start": v(-6.63, -25.9) * mm, "end": v(-6.59, -25.86) * mm});
            skLineSegment(sketch, "E2119", {"start": v(-6.59, -25.86) * mm, "end": v(-6.54, -25.84) * mm});
            skLineSegment(sketch, "E2120", {"start": v(-6.54, -25.84) * mm, "end": v(-6.5, -25.84) * mm});
            skLineSegment(sketch, "E2121", {"start": v(-6.5, -25.84) * mm, "end": v(-6.45, -25.85) * mm});
            skLineSegment(sketch, "E2122", {"start": v(-6.45, -25.85) * mm, "end": v(-6.35, -25.87) * mm});
            skLineSegment(sketch, "E2123", {"start": v(-6.35, -25.87) * mm, "end": v(-5.81, -26) * mm});
            skLineSegment(sketch, "E2124", {"start": v(-5.81, -26) * mm, "end": v(-5.27, -26.11) * mm});
            skLineSegment(sketch, "E2125", {"start": v(-5.27, -26.11) * mm, "end": v(-4.72, -26.22) * mm});
            skLineSegment(sketch, "E2126", {"start": v(-4.72, -26.22) * mm, "end": v(-4.62, -26.24) * mm});
            skLineSegment(sketch, "E2127", {"start": v(-4.62, -26.24) * mm, "end": v(-4.58, -26.25) * mm});
            skLineSegment(sketch, "E2128", {"start": v(-4.58, -26.25) * mm, "end": v(-4.54, -26.27) * mm});
            skLineSegment(sketch, "E2129", {"start": v(-4.54, -26.27) * mm, "end": v(-4.5, -26.3) * mm});
            skLineSegment(sketch, "E2130", {"start": v(-4.5, -26.3) * mm, "end": v(-4.47, -26.35) * mm});
            skLineSegment(sketch, "E2131", {"start": v(-4.47, -26.35) * mm, "end": v(-4.44, -26.42) * mm});
            skLineSegment(sketch, "E2132", {"start": v(-4.44, -26.42) * mm, "end": v(-4.42, -26.5) * mm});
            skLineSegment(sketch, "E2133", {"start": v(-4.42, -26.5) * mm, "end": v(-4.4, -26.58) * mm});
            skLineSegment(sketch, "E2134", {"start": v(-4.4, -26.58) * mm, "end": v(-4.4, -26.68) * mm});
            skLineSegment(sketch, "E2135", {"start": v(-4.4, -26.68) * mm, "end": v(-4.4, -26.79) * mm});
            skLineSegment(sketch, "E2136", {"start": v(-4.4, -26.79) * mm, "end": v(-4.4, -26.91) * mm});
            skLineSegment(sketch, "E2137", {"start": v(-4.4, -26.91) * mm, "end": v(-4.4, -27.05) * mm});
            skLineSegment(sketch, "E2138", {"start": v(-4.4, -27.05) * mm, "end": v(-4.42, -27.2) * mm});
            skLineSegment(sketch, "E2139", {"start": v(-4.42, -27.2) * mm, "end": v(-4.44, -27.35) * mm});
            skLineSegment(sketch, "E2140", {"start": v(-4.44, -27.35) * mm, "end": v(-4.46, -27.43) * mm});
            skLineSegment(sketch, "E2141", {"start": v(-4.46, -27.43) * mm, "end": v(-4.46, -27.44) * mm});
            skLineSegment(sketch, "E2142", {"start": v(-4.46, -27.44) * mm, "end": v(-4.46, -27.45) * mm});
            skLineSegment(sketch, "E2143", {"start": v(-4.46, -27.45) * mm, "end": v(-4.47, -27.48) * mm});
            skLineSegment(sketch, "E2144", {"start": v(-4.47, -27.48) * mm, "end": v(-4.47, -27.52) * mm});
            skLineSegment(sketch, "E2145", {"start": v(-4.47, -27.52) * mm, "end": v(-4.47, -27.58) * mm});
            skLineSegment(sketch, "E2146", {"start": v(-4.47, -27.58) * mm, "end": v(-4.48, -27.64) * mm});
            skLineSegment(sketch, "E2147", {"start": v(-4.48, -27.64) * mm, "end": v(-4.48, -27.72) * mm});
            skLineSegment(sketch, "E2148", {"start": v(-4.48, -27.72) * mm, "end": v(-4.48, -27.81) * mm});
            skLineSegment(sketch, "E2149", {"start": v(-4.48, -27.81) * mm, "end": v(-4.48, -27.91) * mm});
            skLineSegment(sketch, "E2150", {"start": v(-4.48, -27.91) * mm, "end": v(-4.47, -28.03) * mm});
            skLineSegment(sketch, "E2151", {"start": v(-4.47, -28.03) * mm, "end": v(-4.47, -28.15) * mm});
            skLineSegment(sketch, "E2152", {"start": v(-4.47, -28.15) * mm, "end": v(-4.46, -28.3) * mm});
            skLineSegment(sketch, "E2153", {"start": v(-4.46, -28.3) * mm, "end": v(-4.44, -28.44) * mm});
            skLineSegment(sketch, "E2154", {"start": v(-4.44, -28.44) * mm, "end": v(-4.42, -28.6) * mm});
            skLineSegment(sketch, "E2155", {"start": v(-4.42, -28.6) * mm, "end": v(-4.4, -28.78) * mm});
            skLineSegment(sketch, "E2156", {"start": v(-4.4, -28.78) * mm, "end": v(-4.37, -28.97) * mm});
            skLineSegment(sketch, "E2157", {"start": v(-4.37, -28.97) * mm, "end": v(-4.33, -29.16) * mm});
            skLineSegment(sketch, "E2158", {"start": v(-4.33, -29.16) * mm, "end": v(-4.29, -29.37) * mm});
            skLineSegment(sketch, "E2159", {"start": v(-4.29, -29.37) * mm, "end": v(-4.24, -29.59) * mm});
            skLineSegment(sketch, "E2160", {"start": v(-4.24, -29.59) * mm, "end": v(-4.18, -29.82) * mm});
            skLineSegment(sketch, "E2161", {"start": v(-4.18, -29.82) * mm, "end": v(-4.12, -30.06) * mm});
            skLineSegment(sketch, "E2162", {"start": v(-4.12, -30.06) * mm, "end": v(-4.06, -30.25) * mm});
            skLineSegment(sketch, "E2163", {"start": v(-4.06, -30.25) * mm, "end": v(-3.2, -30.4) * mm});
            skLineSegment(sketch, "E2164", {"start": v(-3.2, -30.4) * mm, "end": v(-2.32, -30.44) * mm});
            skLineSegment(sketch, "E2165", {"start": v(-2.32, -30.44) * mm, "end": v(-2.22, -30.26) * mm});
            skLineSegment(sketch, "E2166", {"start": v(-2.22, -30.26) * mm, "end": v(-2.11, -30.04) * mm});
            skLineSegment(sketch, "E2167", {"start": v(-2.11, -30.04) * mm, "end": v(-2, -29.82) * mm});
            skLineSegment(sketch, "E2168", {"start": v(-2, -29.82) * mm, "end": v(-1.91, -29.62) * mm});
            skLineSegment(sketch, "E2169", {"start": v(-1.91, -29.62) * mm, "end": v(-1.83, -29.43) * mm});
            skLineSegment(sketch, "E2170", {"start": v(-1.83, -29.43) * mm, "end": v(-1.75, -29.24) * mm});
            skLineSegment(sketch, "E2171", {"start": v(-1.75, -29.24) * mm, "end": v(-1.68, -29.07) * mm});
            skLineSegment(sketch, "E2172", {"start": v(-1.68, -29.07) * mm, "end": v(-1.62, -28.9) * mm});
            skLineSegment(sketch, "E2173", {"start": v(-1.62, -28.9) * mm, "end": v(-1.57, -28.75) * mm});
            skLineSegment(sketch, "E2174", {"start": v(-1.57, -28.75) * mm, "end": v(-1.52, -28.6) * mm});
            skLineSegment(sketch, "E2175", {"start": v(-1.52, -28.6) * mm, "end": v(-1.48, -28.47) * mm});
            skLineSegment(sketch, "E2176", {"start": v(-1.48, -28.47) * mm, "end": v(-1.45, -28.35) * mm});
            skLineSegment(sketch, "E2177", {"start": v(-1.45, -28.35) * mm, "end": v(-1.42, -28.23) * mm});
            skLineSegment(sketch, "E2178", {"start": v(-1.42, -28.23) * mm, "end": v(-1.4, -28.13) * mm});
            skLineSegment(sketch, "E2179", {"start": v(-1.4, -28.13) * mm, "end": v(-1.38, -28.05) * mm});
            skLineSegment(sketch, "E2180", {"start": v(-1.38, -28.05) * mm, "end": v(-1.37, -27.97) * mm});
            skLineSegment(sketch, "E2181", {"start": v(-1.37, -27.97) * mm, "end": v(-1.36, -27.9) * mm});
            skLineSegment(sketch, "E2182", {"start": v(-1.36, -27.9) * mm, "end": v(-1.35, -27.85) * mm});
            skLineSegment(sketch, "E2183", {"start": v(-1.35, -27.85) * mm, "end": v(-1.34, -27.8) * mm});
            skLineSegment(sketch, "E2184", {"start": v(-1.34, -27.8) * mm, "end": v(-1.34, -27.78) * mm});
            skLineSegment(sketch, "E2185", {"start": v(-1.34, -27.78) * mm, "end": v(-1.34, -27.76) * mm});
            skLineSegment(sketch, "E2186", {"start": v(-1.34, -27.76) * mm, "end": v(-1.34, -27.76) * mm});
            skLineSegment(sketch, "E2187", {"start": v(-1.34, -27.76) * mm, "end": v(-1.34, -27.67) * mm});
            skLineSegment(sketch, "E2188", {"start": v(-1.34, -27.67) * mm, "end": v(-1.33, -27.52) * mm});
            skLineSegment(sketch, "E2189", {"start": v(-1.33, -27.52) * mm, "end": v(-1.32, -27.37) * mm});
            skLineSegment(sketch, "E2190", {"start": v(-1.32, -27.37) * mm, "end": v(-1.3, -27.24) * mm});
            skLineSegment(sketch, "E2191", {"start": v(-1.3, -27.24) * mm, "end": v(-1.28, -27.12) * mm});
            skLineSegment(sketch, "E2192", {"start": v(-1.28, -27.12) * mm, "end": v(-1.25, -27) * mm});
            skLineSegment(sketch, "E2193", {"start": v(-1.25, -27) * mm, "end": v(-1.22, -26.91) * mm});
            skLineSegment(sketch, "E2194", {"start": v(-1.22, -26.91) * mm, "end": v(-1.18, -26.83) * mm});
            skLineSegment(sketch, "E2195", {"start": v(-1.18, -26.83) * mm, "end": v(-1.14, -26.76) * mm});
            skLineSegment(sketch, "E2196", {"start": v(-1.14, -26.76) * mm, "end": v(-1.1, -26.7) * mm});
            skLineSegment(sketch, "E2197", {"start": v(-1.1, -26.7) * mm, "end": v(-1.06, -26.67) * mm});
            skLineSegment(sketch, "E2198", {"start": v(-1.06, -26.67) * mm, "end": v(-1.02, -26.64) * mm});
            skLineSegment(sketch, "E2199", {"start": v(-1.02, -26.64) * mm, "end": v(-0.98, -26.62) * mm});
            skLineSegment(sketch, "E2200", {"start": v(-0.98, -26.62) * mm, "end": v(-0.94, -26.62) * mm});
            skLineSegment(sketch, "E2201", {"start": v(-0.94, -26.62) * mm, "end": v(-0.84, -26.63) * mm});
            skLineSegment(sketch, "E2202", {"start": v(-0.84, -26.63) * mm, "end": v(-0.28, -26.64) * mm});
            skLineSegment(sketch, "E2203", {"start": v(-0.28, -26.64) * mm, "end": v(0.28, -26.64) * mm});
            skLineSegment(sketch, "E2204", {"start": v(0.28, -26.64) * mm, "end": v(0.84, -26.63) * mm});
            skLineSegment(sketch, "E2205", {"start": v(0.84, -26.63) * mm, "end": v(0.94, -26.62) * mm});
            skLineSegment(sketch, "E2206", {"start": v(0.94, -26.62) * mm, "end": v(0.98, -26.62) * mm});
            skLineSegment(sketch, "E2207", {"start": v(0.98, -26.62) * mm, "end": v(1.02, -26.64) * mm});
            skLineSegment(sketch, "E2208", {"start": v(1.02, -26.64) * mm, "end": v(1.06, -26.67) * mm});
            skLineSegment(sketch, "E2209", {"start": v(1.06, -26.67) * mm, "end": v(1.1, -26.7) * mm});
            skLineSegment(sketch, "E2210", {"start": v(1.1, -26.7) * mm, "end": v(1.14, -26.76) * mm});
            skLineSegment(sketch, "E2211", {"start": v(1.14, -26.76) * mm, "end": v(1.18, -26.83) * mm});
            skLineSegment(sketch, "E2212", {"start": v(1.18, -26.83) * mm, "end": v(1.22, -26.91) * mm});
            skLineSegment(sketch, "E2213", {"start": v(1.22, -26.91) * mm, "end": v(1.25, -27) * mm});
            skLineSegment(sketch, "E2214", {"start": v(1.25, -27) * mm, "end": v(1.28, -27.12) * mm});
            skLineSegment(sketch, "E2215", {"start": v(1.28, -27.12) * mm, "end": v(1.3, -27.24) * mm});
            skLineSegment(sketch, "E2216", {"start": v(1.3, -27.24) * mm, "end": v(1.32, -27.37) * mm});
            skLineSegment(sketch, "E2217", {"start": v(1.32, -27.37) * mm, "end": v(1.33, -27.52) * mm});
            skLineSegment(sketch, "E2218", {"start": v(1.33, -27.52) * mm, "end": v(1.34, -27.67) * mm});
            skLineSegment(sketch, "E2219", {"start": v(1.34, -27.67) * mm, "end": v(1.34, -27.76) * mm});
            skLineSegment(sketch, "E2220", {"start": v(1.34, -27.76) * mm, "end": v(1.34, -27.76) * mm});
            skLineSegment(sketch, "E2221", {"start": v(1.34, -27.76) * mm, "end": v(1.34, -27.78) * mm});
            skLineSegment(sketch, "E2222", {"start": v(1.34, -27.78) * mm, "end": v(1.34, -27.8) * mm});
            skLineSegment(sketch, "E2223", {"start": v(1.34, -27.8) * mm, "end": v(1.35, -27.85) * mm});
            skLineSegment(sketch, "E2224", {"start": v(1.35, -27.85) * mm, "end": v(1.36, -27.9) * mm});
            skLineSegment(sketch, "E2225", {"start": v(1.36, -27.9) * mm, "end": v(1.37, -27.97) * mm});
            skLineSegment(sketch, "E2226", {"start": v(1.37, -27.97) * mm, "end": v(1.38, -28.05) * mm});
            skLineSegment(sketch, "E2227", {"start": v(1.38, -28.05) * mm, "end": v(1.4, -28.13) * mm});
            skLineSegment(sketch, "E2228", {"start": v(1.4, -28.13) * mm, "end": v(1.42, -28.23) * mm});
            skLineSegment(sketch, "E2229", {"start": v(1.42, -28.23) * mm, "end": v(1.45, -28.35) * mm});
            skLineSegment(sketch, "E2230", {"start": v(1.45, -28.35) * mm, "end": v(1.48, -28.47) * mm});
            skLineSegment(sketch, "E2231", {"start": v(1.48, -28.47) * mm, "end": v(1.52, -28.6) * mm});
            skLineSegment(sketch, "E2232", {"start": v(1.52, -28.6) * mm, "end": v(1.57, -28.75) * mm});
            skLineSegment(sketch, "E2233", {"start": v(1.57, -28.75) * mm, "end": v(1.62, -28.9) * mm});
            skLineSegment(sketch, "E2234", {"start": v(1.62, -28.9) * mm, "end": v(1.68, -29.07) * mm});
            skLineSegment(sketch, "E2235", {"start": v(1.68, -29.07) * mm, "end": v(1.75, -29.24) * mm});
            skLineSegment(sketch, "E2236", {"start": v(1.75, -29.24) * mm, "end": v(1.83, -29.43) * mm});
            skLineSegment(sketch, "E2237", {"start": v(1.83, -29.43) * mm, "end": v(1.91, -29.62) * mm});
            skLineSegment(sketch, "E2238", {"start": v(1.91, -29.62) * mm, "end": v(2, -29.82) * mm});
            skLineSegment(sketch, "E2239", {"start": v(2, -29.82) * mm, "end": v(2.11, -30.04) * mm});
            skLineSegment(sketch, "E2240", {"start": v(2.11, -30.04) * mm, "end": v(2.22, -30.26) * mm});
            skLineSegment(sketch, "E2241", {"start": v(2.22, -30.26) * mm, "end": v(2.32, -30.44) * mm});
            skLineSegment(sketch, "E2242", {"start": v(2.32, -30.44) * mm, "end": v(3.2, -30.4) * mm});
            skLineSegment(sketch, "E2243", {"start": v(3.2, -30.4) * mm, "end": v(4.06, -30.25) * mm});
            skLineSegment(sketch, "E2244", {"start": v(4.06, -30.25) * mm, "end": v(4.12, -30.06) * mm});
            skLineSegment(sketch, "E2245", {"start": v(4.12, -30.06) * mm, "end": v(4.18, -29.82) * mm});
            skLineSegment(sketch, "E2246", {"start": v(4.18, -29.82) * mm, "end": v(4.24, -29.59) * mm});
            skLineSegment(sketch, "E2247", {"start": v(4.24, -29.59) * mm, "end": v(4.29, -29.37) * mm});
            skLineSegment(sketch, "E2248", {"start": v(4.29, -29.37) * mm, "end": v(4.33, -29.16) * mm});
            skLineSegment(sketch, "E2249", {"start": v(4.33, -29.16) * mm, "end": v(4.37, -28.97) * mm});
            skLineSegment(sketch, "E2250", {"start": v(4.37, -28.97) * mm, "end": v(4.4, -28.78) * mm});
            skLineSegment(sketch, "E2251", {"start": v(4.4, -28.78) * mm, "end": v(4.42, -28.6) * mm});
            skLineSegment(sketch, "E2252", {"start": v(4.42, -28.6) * mm, "end": v(4.44, -28.44) * mm});
            skLineSegment(sketch, "E2253", {"start": v(4.44, -28.44) * mm, "end": v(4.46, -28.3) * mm});
            skLineSegment(sketch, "E2254", {"start": v(4.46, -28.3) * mm, "end": v(4.47, -28.15) * mm});
            skLineSegment(sketch, "E2255", {"start": v(4.47, -28.15) * mm, "end": v(4.47, -28.03) * mm});
            skLineSegment(sketch, "E2256", {"start": v(4.47, -28.03) * mm, "end": v(4.48, -27.91) * mm});
            skLineSegment(sketch, "E2257", {"start": v(4.48, -27.91) * mm, "end": v(4.48, -27.81) * mm});
            skLineSegment(sketch, "E2258", {"start": v(4.48, -27.81) * mm, "end": v(4.48, -27.72) * mm});
            skLineSegment(sketch, "E2259", {"start": v(4.48, -27.72) * mm, "end": v(4.48, -27.64) * mm});
            skLineSegment(sketch, "E2260", {"start": v(4.48, -27.64) * mm, "end": v(4.47, -27.58) * mm});
            skLineSegment(sketch, "E2261", {"start": v(4.47, -27.58) * mm, "end": v(4.47, -27.52) * mm});
            skLineSegment(sketch, "E2262", {"start": v(4.47, -27.52) * mm, "end": v(4.47, -27.48) * mm});
            skLineSegment(sketch, "E2263", {"start": v(4.47, -27.48) * mm, "end": v(4.46, -27.45) * mm});
            skLineSegment(sketch, "E2264", {"start": v(4.46, -27.45) * mm, "end": v(4.46, -27.44) * mm});
            skLineSegment(sketch, "E2265", {"start": v(4.46, -27.44) * mm, "end": v(4.46, -27.43) * mm});
            skLineSegment(sketch, "E2266", {"start": v(4.46, -27.43) * mm, "end": v(4.44, -27.35) * mm});
            skLineSegment(sketch, "E2267", {"start": v(4.44, -27.35) * mm, "end": v(4.42, -27.2) * mm});
            skLineSegment(sketch, "E2268", {"start": v(4.42, -27.2) * mm, "end": v(4.4, -27.05) * mm});
            skLineSegment(sketch, "E2269", {"start": v(4.4, -27.05) * mm, "end": v(4.4, -26.91) * mm});
            skLineSegment(sketch, "E2270", {"start": v(4.4, -26.91) * mm, "end": v(4.4, -26.79) * mm});
            skLineSegment(sketch, "E2271", {"start": v(4.4, -26.79) * mm, "end": v(4.4, -26.68) * mm});
            skLineSegment(sketch, "E2272", {"start": v(4.4, -26.68) * mm, "end": v(4.4, -26.58) * mm});
            skLineSegment(sketch, "E2273", {"start": v(4.4, -26.58) * mm, "end": v(4.42, -26.5) * mm});
            skLineSegment(sketch, "E2274", {"start": v(4.42, -26.5) * mm, "end": v(4.44, -26.42) * mm});
            skLineSegment(sketch, "E2275", {"start": v(4.44, -26.42) * mm, "end": v(4.47, -26.35) * mm});
            skLineSegment(sketch, "E2276", {"start": v(4.47, -26.35) * mm, "end": v(4.5, -26.3) * mm});
            skLineSegment(sketch, "E2277", {"start": v(4.5, -26.3) * mm, "end": v(4.54, -26.27) * mm});
            skLineSegment(sketch, "E2278", {"start": v(4.54, -26.27) * mm, "end": v(4.58, -26.25) * mm});
            skLineSegment(sketch, "E2279", {"start": v(4.58, -26.25) * mm, "end": v(4.62, -26.24) * mm});
            skLineSegment(sketch, "E2280", {"start": v(4.62, -26.24) * mm, "end": v(4.72, -26.22) * mm});
            skLineSegment(sketch, "E2281", {"start": v(4.72, -26.22) * mm, "end": v(5.27, -26.11) * mm});
            skLineSegment(sketch, "E2282", {"start": v(5.27, -26.11) * mm, "end": v(5.81, -26) * mm});
            skLineSegment(sketch, "E2283", {"start": v(5.81, -26) * mm, "end": v(6.35, -25.87) * mm});
            skLineSegment(sketch, "E2284", {"start": v(6.35, -25.87) * mm, "end": v(6.45, -25.85) * mm});
            skLineSegment(sketch, "E2285", {"start": v(6.45, -25.85) * mm, "end": v(6.5, -25.84) * mm});
            skLineSegment(sketch, "E2286", {"start": v(6.5, -25.84) * mm, "end": v(6.54, -25.84) * mm});
            skLineSegment(sketch, "E2287", {"start": v(6.54, -25.84) * mm, "end": v(6.59, -25.86) * mm});
            skLineSegment(sketch, "E2288", {"start": v(6.59, -25.86) * mm, "end": v(6.63, -25.9) * mm});
            skLineSegment(sketch, "E2289", {"start": v(6.63, -25.9) * mm, "end": v(6.68, -25.94) * mm});
            skLineSegment(sketch, "E2290", {"start": v(6.68, -25.94) * mm, "end": v(6.73, -26) * mm});
            skLineSegment(sketch, "E2291", {"start": v(6.73, -26) * mm, "end": v(6.78, -26.07) * mm});
            skLineSegment(sketch, "E2292", {"start": v(6.78, -26.07) * mm, "end": v(6.84, -26.16) * mm});
            skLineSegment(sketch, "E2293", {"start": v(6.84, -26.16) * mm, "end": v(6.88, -26.26) * mm});
            skLineSegment(sketch, "E2294", {"start": v(6.88, -26.26) * mm, "end": v(6.93, -26.37) * mm});
            skLineSegment(sketch, "E2295", {"start": v(6.93, -26.37) * mm, "end": v(6.98, -26.5) * mm});
            skLineSegment(sketch, "E2296", {"start": v(6.98, -26.5) * mm, "end": v(7.02, -26.64) * mm});
            skLineSegment(sketch, "E2297", {"start": v(7.02, -26.64) * mm, "end": v(7.06, -26.8) * mm});
            skLineSegment(sketch, "E2298", {"start": v(7.06, -26.8) * mm, "end": v(7.08, -26.88) * mm});
            skLineSegment(sketch, "E2299", {"start": v(7.08, -26.88) * mm, "end": v(7.08, -26.88) * mm});
            skLineSegment(sketch, "E2300", {"start": v(7.08, -26.88) * mm, "end": v(7.09, -26.9) * mm});
            skLineSegment(sketch, "E2301", {"start": v(7.09, -26.9) * mm, "end": v(7.1, -26.92) * mm});
            skLineSegment(sketch, "E2302", {"start": v(7.1, -26.92) * mm, "end": v(7.11, -26.96) * mm});
            skLineSegment(sketch, "E2303", {"start": v(7.11, -26.96) * mm, "end": v(7.13, -27.01) * mm});
            skLineSegment(sketch, "E2304", {"start": v(7.13, -27.01) * mm, "end": v(7.15, -27.07) * mm});
            skLineSegment(sketch, "E2305", {"start": v(7.15, -27.07) * mm, "end": v(7.18, -27.15) * mm});
            skLineSegment(sketch, "E2306", {"start": v(7.18, -27.15) * mm, "end": v(7.22, -27.23) * mm});
            skLineSegment(sketch, "E2307", {"start": v(7.22, -27.23) * mm, "end": v(7.26, -27.32) * mm});
            skLineSegment(sketch, "E2308", {"start": v(7.26, -27.32) * mm, "end": v(7.31, -27.43) * mm});
            skLineSegment(sketch, "E2309", {"start": v(7.31, -27.43) * mm, "end": v(7.37, -27.54) * mm});
            skLineSegment(sketch, "E2310", {"start": v(7.37, -27.54) * mm, "end": v(7.44, -27.66) * mm});
            skLineSegment(sketch, "E2311", {"start": v(7.44, -27.66) * mm, "end": v(7.51, -27.8) * mm});
            skLineSegment(sketch, "E2312", {"start": v(7.51, -27.8) * mm, "end": v(7.6, -27.93) * mm});
            skLineSegment(sketch, "E2313", {"start": v(7.6, -27.93) * mm, "end": v(7.69, -28.08) * mm});
            skLineSegment(sketch, "E2314", {"start": v(7.69, -28.08) * mm, "end": v(7.8, -28.24) * mm});
            skLineSegment(sketch, "E2315", {"start": v(7.8, -28.24) * mm, "end": v(7.9, -28.4) * mm});
            skLineSegment(sketch, "E2316", {"start": v(7.9, -28.4) * mm, "end": v(8.03, -28.58) * mm});
            skLineSegment(sketch, "E2317", {"start": v(8.03, -28.58) * mm, "end": v(8.16, -28.76) * mm});
            skLineSegment(sketch, "E2318", {"start": v(8.16, -28.76) * mm, "end": v(8.3, -28.94) * mm});
            skLineSegment(sketch, "E2319", {"start": v(8.3, -28.94) * mm, "end": v(8.47, -29.13) * mm});
            skLineSegment(sketch, "E2320", {"start": v(8.47, -29.13) * mm, "end": v(8.6, -29.29) * mm});
            skLineSegment(sketch, "E2321", {"start": v(8.6, -29.29) * mm, "end": v(9.44, -29.06) * mm});
            skLineSegment(sketch, "E2322", {"start": v(9.44, -29.06) * mm, "end": v(10.26, -28.75) * mm});
            skLineSegment(sketch, "E2323", {"start": v(10.26, -28.75) * mm, "end": v(10.28, -28.55) * mm});
            skLineSegment(sketch, "E2324", {"start": v(10.28, -28.55) * mm, "end": v(10.29, -28.3) * mm});
            skLineSegment(sketch, "E2325", {"start": v(10.29, -28.3) * mm, "end": v(10.3, -28.06) * mm});
            skLineSegment(sketch, "E2326", {"start": v(10.3, -28.06) * mm, "end": v(10.3, -27.84) * mm});
            skLineSegment(sketch, "E2327", {"start": v(10.3, -27.84) * mm, "end": v(10.3, -27.62) * mm});
            skLineSegment(sketch, "E2328", {"start": v(10.3, -27.62) * mm, "end": v(10.3, -27.42) * mm});
            skLineSegment(sketch, "E2329", {"start": v(10.3, -27.42) * mm, "end": v(10.29, -27.24) * mm});
            skLineSegment(sketch, "E2330", {"start": v(10.29, -27.24) * mm, "end": v(10.27, -27.06) * mm});
            skLineSegment(sketch, "E2331", {"start": v(10.27, -27.06) * mm, "end": v(10.26, -26.9) * mm});
            skLineSegment(sketch, "E2332", {"start": v(10.26, -26.9) * mm, "end": v(10.24, -26.75) * mm});
            skLineSegment(sketch, "E2333", {"start": v(10.24, -26.75) * mm, "end": v(10.22, -26.61) * mm});
            skLineSegment(sketch, "E2334", {"start": v(10.22, -26.61) * mm, "end": v(10.2, -26.49) * mm});
            skLineSegment(sketch, "E2335", {"start": v(10.2, -26.49) * mm, "end": v(10.18, -26.37) * mm});
            skLineSegment(sketch, "E2336", {"start": v(10.18, -26.37) * mm, "end": v(10.16, -26.27) * mm});
            skLineSegment(sketch, "E2337", {"start": v(10.16, -26.27) * mm, "end": v(10.15, -26.18) * mm});
            skLineSegment(sketch, "E2338", {"start": v(10.15, -26.18) * mm, "end": v(10.13, -26.1) * mm});
            skLineSegment(sketch, "E2339", {"start": v(10.13, -26.1) * mm, "end": v(10.11, -26.04) * mm});
            skLineSegment(sketch, "E2340", {"start": v(10.11, -26.04) * mm, "end": v(10.1, -26) * mm});
            skLineSegment(sketch, "E2341", {"start": v(10.1, -26) * mm, "end": v(10.08, -25.95) * mm});
            skLineSegment(sketch, "E2342", {"start": v(10.08, -25.95) * mm, "end": v(10.07, -25.92) * mm});
            skLineSegment(sketch, "E2343", {"start": v(10.07, -25.92) * mm, "end": v(10.07, -25.9) * mm});
            skLineSegment(sketch, "E2344", {"start": v(10.07, -25.9) * mm, "end": v(10.07, -25.9) * mm});
            skLineSegment(sketch, "E2345", {"start": v(10.07, -25.9) * mm, "end": v(10.03, -25.83) * mm});
            skLineSegment(sketch, "E2346", {"start": v(10.03, -25.83) * mm, "end": v(9.98, -25.68) * mm});
            skLineSegment(sketch, "E2347", {"start": v(9.98, -25.68) * mm, "end": v(9.93, -25.54) * mm});
            skLineSegment(sketch, "E2348", {"start": v(9.93, -25.54) * mm, "end": v(9.9, -25.4) * mm});
            skLineSegment(sketch, "E2349", {"start": v(9.9, -25.4) * mm, "end": v(9.86, -25.29) * mm});
            skLineSegment(sketch, "E2350", {"start": v(9.86, -25.29) * mm, "end": v(9.85, -25.18) * mm});
            skLineSegment(sketch, "E2351", {"start": v(9.85, -25.18) * mm, "end": v(9.84, -25.08) * mm});
            skLineSegment(sketch, "E2352", {"start": v(9.84, -25.08) * mm, "end": v(9.83, -25) * mm});
            skLineSegment(sketch, "E2353", {"start": v(9.83, -25) * mm, "end": v(9.84, -24.91) * mm});
            skLineSegment(sketch, "E2354", {"start": v(9.84, -24.91) * mm, "end": v(9.85, -24.85) * mm});
            skLineSegment(sketch, "E2355", {"start": v(9.85, -24.85) * mm, "end": v(9.87, -24.8) * mm});
            skLineSegment(sketch, "E2356", {"start": v(9.87, -24.8) * mm, "end": v(9.9, -24.75) * mm});
            skLineSegment(sketch, "E2357", {"start": v(9.9, -24.75) * mm, "end": v(9.93, -24.72) * mm});
            skLineSegment(sketch, "E2358", {"start": v(9.93, -24.72) * mm, "end": v(9.97, -24.7) * mm});
            skLineSegment(sketch, "E2359", {"start": v(9.97, -24.7) * mm, "end": v(10.07, -24.66) * mm});
            skLineSegment(sketch, "E2360", {"start": v(10.07, -24.66) * mm, "end": v(10.58, -24.45) * mm});
            skLineSegment(sketch, "E2361", {"start": v(10.58, -24.45) * mm, "end": v(11.09, -24.22) * mm});
            skLineSegment(sketch, "E2362", {"start": v(11.09, -24.22) * mm, "end": v(11.6, -23.98) * mm});
            skLineSegment(sketch, "E2363", {"start": v(11.6, -23.98) * mm, "end": v(11.69, -23.94) * mm});
            skLineSegment(sketch, "E2364", {"start": v(11.69, -23.94) * mm, "end": v(11.72, -23.92) * mm});
            skLineSegment(sketch, "E2365", {"start": v(11.72, -23.92) * mm, "end": v(11.77, -23.92) * mm});
            skLineSegment(sketch, "E2366", {"start": v(11.77, -23.92) * mm, "end": v(11.82, -23.93) * mm});
            skLineSegment(sketch, "E2367", {"start": v(11.82, -23.93) * mm, "end": v(11.87, -23.95) * mm});
            skLineSegment(sketch, "E2368", {"start": v(11.87, -23.95) * mm, "end": v(11.93, -23.98) * mm});
            skLineSegment(sketch, "E2369", {"start": v(11.93, -23.98) * mm, "end": v(12, -24.03) * mm});
            skLineSegment(sketch, "E2370", {"start": v(12, -24.03) * mm, "end": v(12.06, -24.1) * mm});
            skLineSegment(sketch, "E2371", {"start": v(12.06, -24.1) * mm, "end": v(12.12, -24.17) * mm});
            skLineSegment(sketch, "E2372", {"start": v(12.12, -24.17) * mm, "end": v(12.2, -24.25) * mm});
            skLineSegment(sketch, "E2373", {"start": v(12.2, -24.25) * mm, "end": v(12.26, -24.35) * mm});
            skLineSegment(sketch, "E2374", {"start": v(12.26, -24.35) * mm, "end": v(12.34, -24.47) * mm});
            skLineSegment(sketch, "E2375", {"start": v(12.34, -24.47) * mm, "end": v(12.4, -24.6) * mm});
            skLineSegment(sketch, "E2376", {"start": v(12.4, -24.6) * mm, "end": v(12.48, -24.74) * mm});
            skLineSegment(sketch, "E2377", {"start": v(12.48, -24.74) * mm, "end": v(12.52, -24.82) * mm});
            skLineSegment(sketch, "E2378", {"start": v(12.52, -24.82) * mm, "end": v(12.52, -24.82) * mm});
            skLineSegment(sketch, "E2379", {"start": v(12.52, -24.82) * mm, "end": v(12.52, -24.83) * mm});
            skLineSegment(sketch, "E2380", {"start": v(12.52, -24.83) * mm, "end": v(12.54, -24.86) * mm});
            skLineSegment(sketch, "E2381", {"start": v(12.54, -24.86) * mm, "end": v(12.56, -24.9) * mm});
            skLineSegment(sketch, "E2382", {"start": v(12.56, -24.9) * mm, "end": v(12.59, -24.94) * mm});
            skLineSegment(sketch, "E2383", {"start": v(12.59, -24.94) * mm, "end": v(12.63, -25) * mm});
            skLineSegment(sketch, "E2384", {"start": v(12.63, -25) * mm, "end": v(12.67, -25.06) * mm});
            skLineSegment(sketch, "E2385", {"start": v(12.67, -25.06) * mm, "end": v(12.72, -25.13) * mm});
            skLineSegment(sketch, "E2386", {"start": v(12.72, -25.13) * mm, "end": v(12.78, -25.22) * mm});
            skLineSegment(sketch, "E2387", {"start": v(12.78, -25.22) * mm, "end": v(12.85, -25.3) * mm});
            skLineSegment(sketch, "E2388", {"start": v(12.85, -25.3) * mm, "end": v(12.93, -25.4) * mm});
            skLineSegment(sketch, "E2389", {"start": v(12.93, -25.4) * mm, "end": v(13.02, -25.5) * mm});
            skLineSegment(sketch, "E2390", {"start": v(13.02, -25.5) * mm, "end": v(13.13, -25.62) * mm});
            skLineSegment(sketch, "E2391", {"start": v(13.13, -25.62) * mm, "end": v(13.24, -25.74) * mm});
            skLineSegment(sketch, "E2392", {"start": v(13.24, -25.74) * mm, "end": v(13.36, -25.87) * mm});
            skLineSegment(sketch, "E2393", {"start": v(13.36, -25.87) * mm, "end": v(13.5, -26) * mm});
            skLineSegment(sketch, "E2394", {"start": v(13.5, -26) * mm, "end": v(13.64, -26.14) * mm});
            skLineSegment(sketch, "E2395", {"start": v(13.64, -26.14) * mm, "end": v(13.8, -26.28) * mm});
            skLineSegment(sketch, "E2396", {"start": v(13.8, -26.28) * mm, "end": v(13.96, -26.43) * mm});
            skLineSegment(sketch, "E2397", {"start": v(13.96, -26.43) * mm, "end": v(14.14, -26.58) * mm});
            skLineSegment(sketch, "E2398", {"start": v(14.14, -26.58) * mm, "end": v(14.34, -26.74) * mm});
            skLineSegment(sketch, "E2399", {"start": v(14.34, -26.74) * mm, "end": v(14.5, -26.86) * mm});
            skLineSegment(sketch, "E2400", {"start": v(14.5, -26.86) * mm, "end": v(15.28, -26.46) * mm});
            skLineSegment(sketch, "E2401", {"start": v(15.28, -26.46) * mm, "end": v(16.01, -25.99) * mm});
            skLineSegment(sketch, "E2402", {"start": v(16.01, -25.99) * mm, "end": v(15.99, -25.79) * mm});
            skLineSegment(sketch, "E2403", {"start": v(15.99, -25.79) * mm, "end": v(15.95, -25.54) * mm});
            skLineSegment(sketch, "E2404", {"start": v(15.95, -25.54) * mm, "end": v(15.9, -25.3) * mm});
            skLineSegment(sketch, "E2405", {"start": v(15.9, -25.3) * mm, "end": v(15.86, -25.09) * mm});
            skLineSegment(sketch, "E2406", {"start": v(15.86, -25.09) * mm, "end": v(15.82, -24.88) * mm});
            skLineSegment(sketch, "E2407", {"start": v(15.82, -24.88) * mm, "end": v(15.77, -24.69) * mm});
            skLineSegment(sketch, "E2408", {"start": v(15.77, -24.69) * mm, "end": v(15.72, -24.5) * mm});
            skLineSegment(sketch, "E2409", {"start": v(15.72, -24.5) * mm, "end": v(15.68, -24.33) * mm});
            skLineSegment(sketch, "E2410", {"start": v(15.68, -24.33) * mm, "end": v(15.63, -24.18) * mm});
            skLineSegment(sketch, "E2411", {"start": v(15.63, -24.18) * mm, "end": v(15.58, -24.03) * mm});
            skLineSegment(sketch, "E2412", {"start": v(15.58, -24.03) * mm, "end": v(15.53, -23.9) * mm});
            skLineSegment(sketch, "E2413", {"start": v(15.53, -23.9) * mm, "end": v(15.49, -23.78) * mm});
            skLineSegment(sketch, "E2414", {"start": v(15.49, -23.78) * mm, "end": v(15.45, -23.68) * mm});
            skLineSegment(sketch, "E2415", {"start": v(15.45, -23.68) * mm, "end": v(15.4, -23.58) * mm});
            skLineSegment(sketch, "E2416", {"start": v(15.4, -23.58) * mm, "end": v(15.37, -23.5) * mm});
            skLineSegment(sketch, "E2417", {"start": v(15.37, -23.5) * mm, "end": v(15.33, -23.43) * mm});
            skLineSegment(sketch, "E2418", {"start": v(15.33, -23.43) * mm, "end": v(15.3, -23.37) * mm});
            skLineSegment(sketch, "E2419", {"start": v(15.3, -23.37) * mm, "end": v(15.28, -23.32) * mm});
            skLineSegment(sketch, "E2420", {"start": v(15.28, -23.32) * mm, "end": v(15.26, -23.29) * mm});
            skLineSegment(sketch, "E2421", {"start": v(15.26, -23.29) * mm, "end": v(15.24, -23.26) * mm});
            skLineSegment(sketch, "E2422", {"start": v(15.24, -23.26) * mm, "end": v(15.23, -23.25) * mm});
            skLineSegment(sketch, "E2423", {"start": v(15.23, -23.25) * mm, "end": v(15.23, -23.25) * mm});
            skLineSegment(sketch, "E2424", {"start": v(15.23, -23.25) * mm, "end": v(15.18, -23.18) * mm});
            skLineSegment(sketch, "E2425", {"start": v(15.18, -23.18) * mm, "end": v(15.1, -23.04) * mm});
            skLineSegment(sketch, "E2426", {"start": v(15.1, -23.04) * mm, "end": v(15.02, -22.92) * mm});
            skLineSegment(sketch, "E2427", {"start": v(15.02, -22.92) * mm, "end": v(14.96, -22.8) * mm});
            skLineSegment(sketch, "E2428", {"start": v(14.96, -22.8) * mm, "end": v(14.9, -22.69) * mm});
            skLineSegment(sketch, "E2429", {"start": v(14.9, -22.69) * mm, "end": v(14.87, -22.58) * mm});
            skLineSegment(sketch, "E2430", {"start": v(14.87, -22.58) * mm, "end": v(14.83, -22.49) * mm});
            skLineSegment(sketch, "E2431", {"start": v(14.83, -22.49) * mm, "end": v(14.81, -22.4) * mm});
            skLineSegment(sketch, "E2432", {"start": v(14.81, -22.4) * mm, "end": v(14.8, -22.32) * mm});
            skLineSegment(sketch, "E2433", {"start": v(14.8, -22.32) * mm, "end": v(14.8, -22.26) * mm});
            skLineSegment(sketch, "E2434", {"start": v(14.8, -22.26) * mm, "end": v(14.81, -22.2) * mm});
            skLineSegment(sketch, "E2435", {"start": v(14.81, -22.2) * mm, "end": v(14.83, -22.15) * mm});
            skLineSegment(sketch, "E2436", {"start": v(14.83, -22.15) * mm, "end": v(14.86, -22.11) * mm});
            skLineSegment(sketch, "E2437", {"start": v(14.86, -22.11) * mm, "end": v(14.89, -22.09) * mm});
            skLineSegment(sketch, "E2438", {"start": v(14.89, -22.09) * mm, "end": v(14.97, -22.03) * mm});
            skLineSegment(sketch, "E2439", {"start": v(14.97, -22.03) * mm, "end": v(15.43, -21.71) * mm});
            skLineSegment(sketch, "E2440", {"start": v(15.43, -21.71) * mm, "end": v(15.88, -21.39) * mm});
            skLineSegment(sketch, "E2441", {"start": v(15.88, -21.39) * mm, "end": v(16.33, -21.05) * mm});
            skLineSegment(sketch, "E2442", {"start": v(16.33, -21.05) * mm, "end": v(16.4, -20.99) * mm});
            skLineSegment(sketch, "E2443", {"start": v(16.4, -20.99) * mm, "end": v(16.44, -20.96) * mm});
            skLineSegment(sketch, "E2444", {"start": v(16.44, -20.96) * mm, "end": v(16.48, -20.95) * mm});
            skLineSegment(sketch, "E2445", {"start": v(16.48, -20.95) * mm, "end": v(16.54, -20.95) * mm});
            skLineSegment(sketch, "E2446", {"start": v(16.54, -20.95) * mm, "end": v(16.6, -20.96) * mm});
            skLineSegment(sketch, "E2447", {"start": v(16.6, -20.96) * mm, "end": v(16.66, -20.98) * mm});
            skLineSegment(sketch, "E2448", {"start": v(16.66, -20.98) * mm, "end": v(16.73, -21.01) * mm});
            skLineSegment(sketch, "E2449", {"start": v(16.73, -21.01) * mm, "end": v(16.8, -21.06) * mm});
            skLineSegment(sketch, "E2450", {"start": v(16.8, -21.06) * mm, "end": v(16.88, -21.12) * mm});
            skLineSegment(sketch, "E2451", {"start": v(16.88, -21.12) * mm, "end": v(16.97, -21.19) * mm});
            skLineSegment(sketch, "E2452", {"start": v(16.97, -21.19) * mm, "end": v(17.06, -21.27) * mm});
            skLineSegment(sketch, "E2453", {"start": v(17.06, -21.27) * mm, "end": v(17.15, -21.37) * mm});
            skLineSegment(sketch, "E2454", {"start": v(17.15, -21.37) * mm, "end": v(17.25, -21.48) * mm});
            skLineSegment(sketch, "E2455", {"start": v(17.25, -21.48) * mm, "end": v(17.35, -21.6) * mm});
            skLineSegment(sketch, "E2456", {"start": v(17.35, -21.6) * mm, "end": v(17.4, -21.67) * mm});
            skLineSegment(sketch, "E2457", {"start": v(17.4, -21.67) * mm, "end": v(17.4, -21.67) * mm});
            skLineSegment(sketch, "E2458", {"start": v(17.4, -21.67) * mm, "end": v(17.41, -21.69) * mm});
            skLineSegment(sketch, "E2459", {"start": v(17.41, -21.69) * mm, "end": v(17.43, -21.7) * mm});
            skLineSegment(sketch, "E2460", {"start": v(17.43, -21.7) * mm, "end": v(17.46, -21.74) * mm});
            skLineSegment(sketch, "E2461", {"start": v(17.46, -21.74) * mm, "end": v(17.5, -21.78) * mm});
            skLineSegment(sketch, "E2462", {"start": v(17.5, -21.78) * mm, "end": v(17.55, -21.82) * mm});
            skLineSegment(sketch, "E2463", {"start": v(17.55, -21.82) * mm, "end": v(17.6, -21.88) * mm});
            skLineSegment(sketch, "E2464", {"start": v(17.6, -21.88) * mm, "end": v(17.67, -21.94) * mm});
            skLineSegment(sketch, "E2465", {"start": v(17.67, -21.94) * mm, "end": v(17.75, -22) * mm});
            skLineSegment(sketch, "E2466", {"start": v(17.75, -22) * mm, "end": v(17.83, -22.08) * mm});
            skLineSegment(sketch, "E2467", {"start": v(17.83, -22.08) * mm, "end": v(17.93, -22.16) * mm});
            skLineSegment(sketch, "E2468", {"start": v(17.93, -22.16) * mm, "end": v(18.04, -22.24) * mm});
            skLineSegment(sketch, "E2469", {"start": v(18.04, -22.24) * mm, "end": v(18.17, -22.33) * mm});
            skLineSegment(sketch, "E2470", {"start": v(18.17, -22.33) * mm, "end": v(18.3, -22.43) * mm});
            skLineSegment(sketch, "E2471", {"start": v(18.3, -22.43) * mm, "end": v(18.45, -22.53) * mm});
            skLineSegment(sketch, "E2472", {"start": v(18.45, -22.53) * mm, "end": v(18.6, -22.63) * mm});
            skLineSegment(sketch, "E2473", {"start": v(18.6, -22.63) * mm, "end": v(18.77, -22.73) * mm});
            skLineSegment(sketch, "E2474", {"start": v(18.77, -22.73) * mm, "end": v(18.96, -22.84) * mm});
            skLineSegment(sketch, "E2475", {"start": v(18.96, -22.84) * mm, "end": v(19.15, -22.95) * mm});
            skLineSegment(sketch, "E2476", {"start": v(19.15, -22.95) * mm, "end": v(19.36, -23.06) * mm});
            skLineSegment(sketch, "E2477", {"start": v(19.36, -23.06) * mm, "end": v(19.58, -23.17) * mm});
            skLineSegment(sketch, "E2478", {"start": v(19.58, -23.17) * mm, "end": v(19.77, -23.26) * mm});
            skLineSegment(sketch, "E2479", {"start": v(19.77, -23.26) * mm, "end": v(20.45, -22.7) * mm});
            skLineSegment(sketch, "E2480", {"start": v(20.45, -22.7) * mm, "end": v(21.07, -22.1) * mm});
            skLineSegment(sketch, "E2481", {"start": v(21.07, -22.1) * mm, "end": v(21, -21.9) * mm});
            skLineSegment(sketch, "E2482", {"start": v(21, -21.9) * mm, "end": v(20.9, -21.67) * mm});
            skLineSegment(sketch, "E2483", {"start": v(20.9, -21.67) * mm, "end": v(20.82, -21.45) * mm});
            skLineSegment(sketch, "E2484", {"start": v(20.82, -21.45) * mm, "end": v(20.73, -21.24) * mm});
            skLineSegment(sketch, "E2485", {"start": v(20.73, -21.24) * mm, "end": v(20.65, -21.05) * mm});
            skLineSegment(sketch, "E2486", {"start": v(20.65, -21.05) * mm, "end": v(20.56, -20.87) * mm});
            skLineSegment(sketch, "E2487", {"start": v(20.56, -20.87) * mm, "end": v(20.47, -20.7) * mm});
            skLineSegment(sketch, "E2488", {"start": v(20.47, -20.7) * mm, "end": v(20.4, -20.54) * mm});
            skLineSegment(sketch, "E2489", {"start": v(20.4, -20.54) * mm, "end": v(20.31, -20.4) * mm});
            skLineSegment(sketch, "E2490", {"start": v(20.31, -20.4) * mm, "end": v(20.24, -20.27) * mm});
            skLineSegment(sketch, "E2491", {"start": v(20.24, -20.27) * mm, "end": v(20.16, -20.15) * mm});
            skLineSegment(sketch, "E2492", {"start": v(20.16, -20.15) * mm, "end": v(20.1, -20.04) * mm});
            skLineSegment(sketch, "E2493", {"start": v(20.1, -20.04) * mm, "end": v(20.03, -19.95) * mm});
            skLineSegment(sketch, "E2494", {"start": v(20.03, -19.95) * mm, "end": v(19.97, -19.87) * mm});
            skLineSegment(sketch, "E2495", {"start": v(19.97, -19.87) * mm, "end": v(19.92, -19.8) * mm});
            skLineSegment(sketch, "E2496", {"start": v(19.92, -19.8) * mm, "end": v(19.87, -19.73) * mm});
            skLineSegment(sketch, "E2497", {"start": v(19.87, -19.73) * mm, "end": v(19.83, -19.68) * mm});
            skLineSegment(sketch, "E2498", {"start": v(19.83, -19.68) * mm, "end": v(19.8, -19.64) * mm});
            skLineSegment(sketch, "E2499", {"start": v(19.8, -19.64) * mm, "end": v(19.77, -19.6) * mm});
            skLineSegment(sketch, "E2500", {"start": v(19.77, -19.6) * mm, "end": v(19.75, -19.59) * mm});
            skLineSegment(sketch, "E2501", {"start": v(19.75, -19.59) * mm, "end": v(19.74, -19.57) * mm});
            skLineSegment(sketch, "E2502", {"start": v(19.74, -19.57) * mm, "end": v(19.73, -19.57) * mm});
            skLineSegment(sketch, "E2503", {"start": v(19.73, -19.57) * mm, "end": v(19.67, -19.51) * mm});
            skLineSegment(sketch, "E2504", {"start": v(19.67, -19.51) * mm, "end": v(19.56, -19.4) * mm});
            skLineSegment(sketch, "E2505", {"start": v(19.56, -19.4) * mm, "end": v(19.46, -19.3) * mm});
            skLineSegment(sketch, "E2506", {"start": v(19.46, -19.3) * mm, "end": v(19.37, -19.19) * mm});
            skLineSegment(sketch, "E2507", {"start": v(19.37, -19.19) * mm, "end": v(19.3, -19.1) * mm});
            skLineSegment(sketch, "E2508", {"start": v(19.3, -19.1) * mm, "end": v(19.24, -19) * mm});
            skLineSegment(sketch, "E2509", {"start": v(19.24, -19) * mm, "end": v(19.19, -18.91) * mm});
            skLineSegment(sketch, "E2510", {"start": v(19.19, -18.91) * mm, "end": v(19.15, -18.83) * mm});
            skLineSegment(sketch, "E2511", {"start": v(19.15, -18.83) * mm, "end": v(19.12, -18.76) * mm});
            skLineSegment(sketch, "E2512", {"start": v(19.12, -18.76) * mm, "end": v(19.1, -18.7) * mm});
            skLineSegment(sketch, "E2513", {"start": v(19.1, -18.7) * mm, "end": v(19.1, -18.63) * mm});
            skLineSegment(sketch, "E2514", {"start": v(19.1, -18.63) * mm, "end": v(19.11, -18.58) * mm});
            skLineSegment(sketch, "E2515", {"start": v(19.11, -18.58) * mm, "end": v(19.13, -18.54) * mm});
            skLineSegment(sketch, "E2516", {"start": v(19.13, -18.54) * mm, "end": v(19.16, -18.51) * mm});
            skLineSegment(sketch, "E2517", {"start": v(19.16, -18.51) * mm, "end": v(19.23, -18.44) * mm});
            skLineSegment(sketch, "E2518", {"start": v(19.23, -18.44) * mm, "end": v(19.6, -18.03) * mm});
            skLineSegment(sketch, "E2519", {"start": v(19.6, -18.03) * mm, "end": v(19.98, -17.62) * mm});
            skLineSegment(sketch, "E2520", {"start": v(19.98, -17.62) * mm, "end": v(20.35, -17.2) * mm});
            skLineSegment(sketch, "E2521", {"start": v(20.35, -17.2) * mm, "end": v(20.41, -17.12) * mm});
            skLineSegment(sketch, "E2522", {"start": v(20.41, -17.12) * mm, "end": v(20.44, -17.09) * mm});
            skLineSegment(sketch, "E2523", {"start": v(20.44, -17.09) * mm, "end": v(20.48, -17.06) * mm});
            skLineSegment(sketch, "E2524", {"start": v(20.48, -17.06) * mm, "end": v(20.53, -17.05) * mm});
            skLineSegment(sketch, "E2525", {"start": v(20.53, -17.05) * mm, "end": v(20.59, -17.05) * mm});
            skLineSegment(sketch, "E2526", {"start": v(20.59, -17.05) * mm, "end": v(20.65, -17.06) * mm});
            skLineSegment(sketch, "E2527", {"start": v(20.65, -17.06) * mm, "end": v(20.73, -17.08) * mm});
            skLineSegment(sketch, "E2528", {"start": v(20.73, -17.08) * mm, "end": v(20.81, -17.1) * mm});
            skLineSegment(sketch, "E2529", {"start": v(20.81, -17.1) * mm, "end": v(20.9, -17.14) * mm});
            skLineSegment(sketch, "E2530", {"start": v(20.9, -17.14) * mm, "end": v(21, -17.2) * mm});
            skLineSegment(sketch, "E2531", {"start": v(21, -17.2) * mm, "end": v(21.1, -17.26) * mm});
            skLineSegment(sketch, "E2532", {"start": v(21.1, -17.26) * mm, "end": v(21.22, -17.33) * mm});
            skLineSegment(sketch, "E2533", {"start": v(21.22, -17.33) * mm, "end": v(21.34, -17.42) * mm});
            skLineSegment(sketch, "E2534", {"start": v(21.34, -17.42) * mm, "end": v(21.46, -17.52) * mm});
            skLineSegment(sketch, "E2535", {"start": v(21.46, -17.52) * mm, "end": v(21.53, -17.58) * mm});
            skLineSegment(sketch, "E2536", {"start": v(21.53, -17.58) * mm, "end": v(21.53, -17.58) * mm});
            skLineSegment(sketch, "E2537", {"start": v(21.53, -17.58) * mm, "end": v(21.54, -17.6) * mm});
            skLineSegment(sketch, "E2538", {"start": v(21.54, -17.6) * mm, "end": v(21.57, -17.6) * mm});
            skLineSegment(sketch, "E2539", {"start": v(21.57, -17.6) * mm, "end": v(21.6, -17.63) * mm});
            skLineSegment(sketch, "E2540", {"start": v(21.6, -17.63) * mm, "end": v(21.64, -17.66) * mm});
            skLineSegment(sketch, "E2541", {"start": v(21.64, -17.66) * mm, "end": v(21.7, -17.7) * mm});
            skLineSegment(sketch, "E2542", {"start": v(21.7, -17.7) * mm, "end": v(21.77, -17.74) * mm});
            skLineSegment(sketch, "E2543", {"start": v(21.77, -17.74) * mm, "end": v(21.84, -17.79) * mm});
            skLineSegment(sketch, "E2544", {"start": v(21.84, -17.79) * mm, "end": v(21.93, -17.84) * mm});
            skLineSegment(sketch, "E2545", {"start": v(21.93, -17.84) * mm, "end": v(22.04, -17.89) * mm});
            skLineSegment(sketch, "E2546", {"start": v(22.04, -17.89) * mm, "end": v(22.15, -17.95) * mm});
            skLineSegment(sketch, "E2547", {"start": v(22.15, -17.95) * mm, "end": v(22.27, -18) * mm});
            skLineSegment(sketch, "E2548", {"start": v(22.27, -18) * mm, "end": v(22.41, -18.07) * mm});
            skLineSegment(sketch, "E2549", {"start": v(22.41, -18.07) * mm, "end": v(22.56, -18.13) * mm});
            skLineSegment(sketch, "E2550", {"start": v(22.56, -18.13) * mm, "end": v(22.73, -18.2) * mm});
            skLineSegment(sketch, "E2551", {"start": v(22.73, -18.2) * mm, "end": v(22.9, -18.27) * mm});
            skLineSegment(sketch, "E2552", {"start": v(22.9, -18.27) * mm, "end": v(23.09, -18.33) * mm});
            skLineSegment(sketch, "E2553", {"start": v(23.09, -18.33) * mm, "end": v(23.3, -18.4) * mm});
            skLineSegment(sketch, "E2554", {"start": v(23.3, -18.4) * mm, "end": v(23.5, -18.47) * mm});
            skLineSegment(sketch, "E2555", {"start": v(23.5, -18.47) * mm, "end": v(23.73, -18.53) * mm});
            skLineSegment(sketch, "E2556", {"start": v(23.73, -18.53) * mm, "end": v(23.97, -18.6) * mm});
            skLineSegment(sketch, "E2557", {"start": v(23.97, -18.6) * mm, "end": v(24.17, -18.64) * mm});
            skLineSegment(sketch, "E2558", {"start": v(24.17, -18.64) * mm, "end": v(24.72, -17.96) * mm});
            skLineSegment(sketch, "E2559", {"start": v(24.72, -17.96) * mm, "end": v(25.2, -17.23) * mm});
            skLineSegment(sketch, "E2560", {"start": v(25.2, -17.23) * mm, "end": v(25.1, -17.05) * mm});
            skLineSegment(sketch, "E2561", {"start": v(25.1, -17.05) * mm, "end": v(24.96, -16.85) * mm});
            skLineSegment(sketch, "E2562", {"start": v(24.96, -16.85) * mm, "end": v(24.83, -16.65) * mm});
            skLineSegment(sketch, "E2563", {"start": v(24.83, -16.65) * mm, "end": v(24.7, -16.47) * mm});
            skLineSegment(sketch, "E2564", {"start": v(24.7, -16.47) * mm, "end": v(24.57, -16.3) * mm});
            skLineSegment(sketch, "E2565", {"start": v(24.57, -16.3) * mm, "end": v(24.45, -16.14) * mm});
            skLineSegment(sketch, "E2566", {"start": v(24.45, -16.14) * mm, "end": v(24.33, -15.99) * mm});
            skLineSegment(sketch, "E2567", {"start": v(24.33, -15.99) * mm, "end": v(24.22, -15.85) * mm});
            skLineSegment(sketch, "E2568", {"start": v(24.22, -15.85) * mm, "end": v(24.11, -15.73) * mm});
            skLineSegment(sketch, "E2569", {"start": v(24.11, -15.73) * mm, "end": v(24, -15.62) * mm});
            skLineSegment(sketch, "E2570", {"start": v(24, -15.62) * mm, "end": v(23.91, -15.52) * mm});
            skLineSegment(sketch, "E2571", {"start": v(23.91, -15.52) * mm, "end": v(23.82, -15.43) * mm});
            skLineSegment(sketch, "E2572", {"start": v(23.82, -15.43) * mm, "end": v(23.74, -15.35) * mm});
            skLineSegment(sketch, "E2573", {"start": v(23.74, -15.35) * mm, "end": v(23.67, -15.28) * mm});
            skLineSegment(sketch, "E2574", {"start": v(23.67, -15.28) * mm, "end": v(23.6, -15.22) * mm});
            skLineSegment(sketch, "E2575", {"start": v(23.6, -15.22) * mm, "end": v(23.54, -15.17) * mm});
            skLineSegment(sketch, "E2576", {"start": v(23.54, -15.17) * mm, "end": v(23.49, -15.13) * mm});
            skLineSegment(sketch, "E2577", {"start": v(23.49, -15.13) * mm, "end": v(23.45, -15.1) * mm});
            skLineSegment(sketch, "E2578", {"start": v(23.45, -15.1) * mm, "end": v(23.41, -15.07) * mm});
            skLineSegment(sketch, "E2579", {"start": v(23.41, -15.07) * mm, "end": v(23.39, -15.05) * mm});
            skLineSegment(sketch, "E2580", {"start": v(23.39, -15.05) * mm, "end": v(23.37, -15.04) * mm});
            skLineSegment(sketch, "E2581", {"start": v(23.37, -15.04) * mm, "end": v(23.37, -15.04) * mm});
            skLineSegment(sketch, "E2582", {"start": v(23.37, -15.04) * mm, "end": v(23.3, -15) * mm});
            skLineSegment(sketch, "E2583", {"start": v(23.3, -15) * mm, "end": v(23.16, -14.91) * mm});
            skLineSegment(sketch, "E2584", {"start": v(23.16, -14.91) * mm, "end": v(23.04, -14.83) * mm});
            skLineSegment(sketch, "E2585", {"start": v(23.04, -14.83) * mm, "end": v(22.94, -14.74) * mm});
            skLineSegment(sketch, "E2586", {"start": v(22.94, -14.74) * mm, "end": v(22.84, -14.66) * mm});
            skLineSegment(sketch, "E2587", {"start": v(22.84, -14.66) * mm, "end": v(22.77, -14.58) * mm});
            skLineSegment(sketch, "E2588", {"start": v(22.77, -14.58) * mm, "end": v(22.7, -14.5) * mm});
            skLineSegment(sketch, "E2589", {"start": v(22.7, -14.5) * mm, "end": v(22.65, -14.44) * mm});
            skLineSegment(sketch, "E2590", {"start": v(22.65, -14.44) * mm, "end": v(22.6, -14.37) * mm});
            skLineSegment(sketch, "E2591", {"start": v(22.6, -14.37) * mm, "end": v(22.58, -14.31) * mm});
            skLineSegment(sketch, "E2592", {"start": v(22.58, -14.31) * mm, "end": v(22.56, -14.25) * mm});
            skLineSegment(sketch, "E2593", {"start": v(22.56, -14.25) * mm, "end": v(22.56, -14.2) * mm});
            skLineSegment(sketch, "E2594", {"start": v(22.56, -14.2) * mm, "end": v(22.57, -14.16) * mm});
            skLineSegment(sketch, "E2595", {"start": v(22.57, -14.16) * mm, "end": v(22.59, -14.12) * mm});
            skLineSegment(sketch, "E2596", {"start": v(22.59, -14.12) * mm, "end": v(22.64, -14.04) * mm});
            skLineSegment(sketch, "E2597", {"start": v(22.64, -14.04) * mm, "end": v(22.93, -13.56) * mm});
            skLineSegment(sketch, "E2598", {"start": v(22.93, -13.56) * mm, "end": v(23.2, -13.08) * mm});
            skLineSegment(sketch, "E2599", {"start": v(23.2, -13.08) * mm, "end": v(23.48, -12.59) * mm});
            skLineSegment(sketch, "E2600", {"start": v(23.48, -12.59) * mm, "end": v(23.52, -12.5) * mm});
            skLineSegment(sketch, "E2601", {"start": v(23.52, -12.5) * mm, "end": v(23.55, -12.46) * mm});
            skLineSegment(sketch, "E2602", {"start": v(23.55, -12.46) * mm, "end": v(23.58, -12.43) * mm});
            skLineSegment(sketch, "E2603", {"start": v(23.58, -12.43) * mm, "end": v(23.63, -12.41) * mm});
            skLineSegment(sketch, "E2604", {"start": v(23.63, -12.41) * mm, "end": v(23.68, -12.4) * mm});
            skLineSegment(sketch, "E2605", {"start": v(23.68, -12.4) * mm, "end": v(23.75, -12.4) * mm});
            skLineSegment(sketch, "E2606", {"start": v(23.75, -12.4) * mm, "end": v(23.83, -12.4) * mm});
            skLineSegment(sketch, "E2607", {"start": v(23.83, -12.4) * mm, "end": v(23.92, -12.4) * mm});
            skLineSegment(sketch, "E2608", {"start": v(23.92, -12.4) * mm, "end": v(24.01, -12.42) * mm});
            skLineSegment(sketch, "E2609", {"start": v(24.01, -12.42) * mm, "end": v(24.12, -12.45) * mm});
            skLineSegment(sketch, "E2610", {"start": v(24.12, -12.45) * mm, "end": v(24.24, -12.5) * mm});
            skLineSegment(sketch, "E2611", {"start": v(24.24, -12.5) * mm, "end": v(24.36, -12.54) * mm});
            skLineSegment(sketch, "E2612", {"start": v(24.36, -12.54) * mm, "end": v(24.5, -12.6) * mm});
            skLineSegment(sketch, "E2613", {"start": v(24.5, -12.6) * mm, "end": v(24.64, -12.68) * mm});
            skLineSegment(sketch, "E2614", {"start": v(24.64, -12.68) * mm, "end": v(24.71, -12.72) * mm});
            skLineSegment(sketch, "E2615", {"start": v(24.71, -12.72) * mm, "end": v(24.71, -12.72) * mm});
            skLineSegment(sketch, "E2616", {"start": v(24.71, -12.72) * mm, "end": v(24.73, -12.73) * mm});
            skLineSegment(sketch, "E2617", {"start": v(24.73, -12.73) * mm, "end": v(24.76, -12.74) * mm});
            skLineSegment(sketch, "E2618", {"start": v(24.76, -12.74) * mm, "end": v(24.8, -12.76) * mm});
            skLineSegment(sketch, "E2619", {"start": v(24.8, -12.76) * mm, "end": v(24.84, -12.78) * mm});
            skLineSegment(sketch, "E2620", {"start": v(24.84, -12.78) * mm, "end": v(24.9, -12.8) * mm});
            skLineSegment(sketch, "E2621", {"start": v(24.9, -12.8) * mm, "end": v(24.98, -12.83) * mm});
            skLineSegment(sketch, "E2622", {"start": v(24.98, -12.83) * mm, "end": v(25.07, -12.86) * mm});
            skLineSegment(sketch, "E2623", {"start": v(25.07, -12.86) * mm, "end": v(25.16, -12.89) * mm});
            skLineSegment(sketch, "E2624", {"start": v(25.16, -12.89) * mm, "end": v(25.27, -12.92) * mm});
            skLineSegment(sketch, "E2625", {"start": v(25.27, -12.92) * mm, "end": v(25.4, -12.95) * mm});
            skLineSegment(sketch, "E2626", {"start": v(25.4, -12.95) * mm, "end": v(25.53, -12.98) * mm});
            skLineSegment(sketch, "E2627", {"start": v(25.53, -12.98) * mm, "end": v(25.68, -13.01) * mm});
            skLineSegment(sketch, "E2628", {"start": v(25.68, -13.01) * mm, "end": v(25.84, -13.05) * mm});
            skLineSegment(sketch, "E2629", {"start": v(25.84, -13.05) * mm, "end": v(26.01, -13.08) * mm});
            skLineSegment(sketch, "E2630", {"start": v(26.01, -13.08) * mm, "end": v(26.2, -13.1) * mm});
            skLineSegment(sketch, "E2631", {"start": v(26.2, -13.1) * mm, "end": v(26.4, -13.13) * mm});
            skLineSegment(sketch, "E2632", {"start": v(26.4, -13.13) * mm, "end": v(26.6, -13.15) * mm});
            skLineSegment(sketch, "E2633", {"start": v(26.6, -13.15) * mm, "end": v(26.83, -13.17) * mm});
            skLineSegment(sketch, "E2634", {"start": v(26.83, -13.17) * mm, "end": v(27.07, -13.2) * mm});
            skLineSegment(sketch, "E2635", {"start": v(27.07, -13.2) * mm, "end": v(27.32, -13.2) * mm});
            skLineSegment(sketch, "E2636", {"start": v(27.32, -13.2) * mm, "end": v(27.52, -13.2) * mm});
            skLineSegment(sketch, "E2637", {"start": v(27.52, -13.2) * mm, "end": v(27.92, -12.43) * mm});
            skLineSegment(sketch, "E2638", {"start": v(27.92, -12.43) * mm, "end": v(28.23, -11.61) * mm});
            skLineSegment(sketch, "E2639", {"start": v(28.23, -11.61) * mm, "end": v(28.09, -11.47) * mm});
            skLineSegment(sketch, "E2640", {"start": v(28.09, -11.47) * mm, "end": v(27.91, -11.29) * mm});
            skLineSegment(sketch, "E2641", {"start": v(27.91, -11.29) * mm, "end": v(27.74, -11.12) * mm});
            skLineSegment(sketch, "E2642", {"start": v(27.74, -11.12) * mm, "end": v(27.58, -10.97) * mm});
            skLineSegment(sketch, "E2643", {"start": v(27.58, -10.97) * mm, "end": v(27.42, -10.83) * mm});
            skLineSegment(sketch, "E2644", {"start": v(27.42, -10.83) * mm, "end": v(27.27, -10.7) * mm});
            skLineSegment(sketch, "E2645", {"start": v(27.27, -10.7) * mm, "end": v(27.12, -10.58) * mm});
            skLineSegment(sketch, "E2646", {"start": v(27.12, -10.58) * mm, "end": v(26.99, -10.47) * mm});
            skLineSegment(sketch, "E2647", {"start": v(26.99, -10.47) * mm, "end": v(26.85, -10.38) * mm});
            skLineSegment(sketch, "E2648", {"start": v(26.85, -10.38) * mm, "end": v(26.73, -10.29) * mm});
            skLineSegment(sketch, "E2649", {"start": v(26.73, -10.29) * mm, "end": v(26.62, -10.2) * mm});
            skLineSegment(sketch, "E2650", {"start": v(26.62, -10.2) * mm, "end": v(26.51, -10.14) * mm});
            skLineSegment(sketch, "E2651", {"start": v(26.51, -10.14) * mm, "end": v(26.41, -10.08) * mm});
            skLineSegment(sketch, "E2652", {"start": v(26.41, -10.08) * mm, "end": v(26.33, -10.03) * mm});
            skLineSegment(sketch, "E2653", {"start": v(26.33, -10.03) * mm, "end": v(26.25, -9.98) * mm});
            skLineSegment(sketch, "E2654", {"start": v(26.25, -9.98) * mm, "end": v(26.18, -9.94) * mm});
            skLineSegment(sketch, "E2655", {"start": v(26.18, -9.94) * mm, "end": v(26.12, -9.91) * mm});
            skLineSegment(sketch, "E2656", {"start": v(26.12, -9.91) * mm, "end": v(26.07, -9.89) * mm});
            skLineSegment(sketch, "E2657", {"start": v(26.07, -9.89) * mm, "end": v(26.03, -9.87) * mm});
            skLineSegment(sketch, "E2658", {"start": v(26.03, -9.87) * mm, "end": v(26, -9.86) * mm});
            skLineSegment(sketch, "E2659", {"start": v(26, -9.86) * mm, "end": v(26, -9.85) * mm});
            skLineSegment(sketch, "E2660", {"start": v(26, -9.85) * mm, "end": v(25.99, -9.85) * mm});
            skLineSegment(sketch, "E2661", {"start": v(25.99, -9.85) * mm, "end": v(25.9, -9.82) * mm});
            skLineSegment(sketch, "E2662", {"start": v(25.9, -9.82) * mm, "end": v(25.76, -9.77) * mm});
            skLineSegment(sketch, "E2663", {"start": v(25.76, -9.77) * mm, "end": v(25.62, -9.71) * mm});
            skLineSegment(sketch, "E2664", {"start": v(25.62, -9.71) * mm, "end": v(25.5, -9.65) * mm});
            skLineSegment(sketch, "E2665", {"start": v(25.5, -9.65) * mm, "end": v(25.4, -9.6) * mm});
            skLineSegment(sketch, "E2666", {"start": v(25.4, -9.6) * mm, "end": v(25.3, -9.53) * mm});
            skLineSegment(sketch, "E2667", {"start": v(25.3, -9.53) * mm, "end": v(25.22, -9.47) * mm});
            skLineSegment(sketch, "E2668", {"start": v(25.22, -9.47) * mm, "end": v(25.15, -9.41) * mm});
            skLineSegment(sketch, "E2669", {"start": v(25.15, -9.41) * mm, "end": v(25.1, -9.36) * mm});
            skLineSegment(sketch, "E2670", {"start": v(25.1, -9.36) * mm, "end": v(25.06, -9.3) * mm});
            skLineSegment(sketch, "E2671", {"start": v(25.06, -9.3) * mm, "end": v(25.03, -9.25) * mm});
            skLineSegment(sketch, "E2672", {"start": v(25.03, -9.25) * mm, "end": v(25.02, -9.2) * mm});
            skLineSegment(sketch, "E2673", {"start": v(25.02, -9.2) * mm, "end": v(25.02, -9.16) * mm});
            skLineSegment(sketch, "E2674", {"start": v(25.02, -9.16) * mm, "end": v(25.03, -9.12) * mm});
            skLineSegment(sketch, "E2675", {"start": v(25.03, -9.12) * mm, "end": v(25.06, -9.02) * mm});
            skLineSegment(sketch, "E2676", {"start": v(25.06, -9.02) * mm, "end": v(25.25, -8.5) * mm});
            skLineSegment(sketch, "E2677", {"start": v(25.25, -8.5) * mm, "end": v(25.42, -7.97) * mm});
            skLineSegment(sketch, "E2678", {"start": v(25.42, -7.97) * mm, "end": v(25.58, -7.43) * mm});
            skLineSegment(sketch, "E2679", {"start": v(25.58, -7.43) * mm, "end": v(25.6, -7.33) * mm});
            skLineSegment(sketch, "E2680", {"start": v(25.6, -7.33) * mm, "end": v(25.62, -7.3) * mm});
            skLineSegment(sketch, "E2681", {"start": v(25.62, -7.3) * mm, "end": v(25.65, -7.26) * mm});
            skLineSegment(sketch, "E2682", {"start": v(25.65, -7.26) * mm, "end": v(25.69, -7.23) * mm});
            skLineSegment(sketch, "E2683", {"start": v(25.69, -7.23) * mm, "end": v(25.74, -7.2) * mm});
            skLineSegment(sketch, "E2684", {"start": v(25.74, -7.2) * mm, "end": v(25.8, -7.18) * mm});
            skLineSegment(sketch, "E2685", {"start": v(25.8, -7.18) * mm, "end": v(25.88, -7.17) * mm});
            skLineSegment(sketch, "E2686", {"start": v(25.88, -7.17) * mm, "end": v(25.97, -7.16) * mm});
            skLineSegment(sketch, "E2687", {"start": v(25.97, -7.16) * mm, "end": v(26.07, -7.16) * mm});
            skLineSegment(sketch, "E2688", {"start": v(26.07, -7.16) * mm, "end": v(26.18, -7.17) * mm});
            skLineSegment(sketch, "E2689", {"start": v(26.18, -7.17) * mm, "end": v(26.3, -7.18) * mm});
            skLineSegment(sketch, "E2690", {"start": v(26.3, -7.18) * mm, "end": v(26.44, -7.2) * mm});
            skLineSegment(sketch, "E2691", {"start": v(26.44, -7.2) * mm, "end": v(26.58, -7.24) * mm});
            skLineSegment(sketch, "E2692", {"start": v(26.58, -7.24) * mm, "end": v(26.73, -7.28) * mm});
            skLineSegment(sketch, "E2693", {"start": v(26.73, -7.28) * mm, "end": v(26.82, -7.3) * mm});
            skLineSegment(sketch, "E2694", {"start": v(26.82, -7.3) * mm, "end": v(26.82, -7.3) * mm});
            skLineSegment(sketch, "E2695", {"start": v(26.82, -7.3) * mm, "end": v(26.84, -7.3) * mm});
            skLineSegment(sketch, "E2696", {"start": v(26.84, -7.3) * mm, "end": v(26.86, -7.32) * mm});
            skLineSegment(sketch, "E2697", {"start": v(26.86, -7.32) * mm, "end": v(26.9, -7.32) * mm});
            skLineSegment(sketch, "E2698", {"start": v(26.9, -7.32) * mm, "end": v(26.96, -7.33) * mm});
            skLineSegment(sketch, "E2699", {"start": v(26.96, -7.33) * mm, "end": v(27.02, -7.34) * mm});
            skLineSegment(sketch, "E2700", {"start": v(27.02, -7.34) * mm, "end": v(27.1, -7.35) * mm});
            skLineSegment(sketch, "E2701", {"start": v(27.1, -7.35) * mm, "end": v(27.2, -7.36) * mm});
            skLineSegment(sketch, "E2702", {"start": v(27.2, -7.36) * mm, "end": v(27.3, -7.37) * mm});
            skLineSegment(sketch, "E2703", {"start": v(27.3, -7.37) * mm, "end": v(27.4, -7.38) * mm});
            skLineSegment(sketch, "E2704", {"start": v(27.4, -7.38) * mm, "end": v(27.53, -7.39) * mm});
            skLineSegment(sketch, "E2705", {"start": v(27.53, -7.39) * mm, "end": v(27.67, -7.39) * mm});
            skLineSegment(sketch, "E2706", {"start": v(27.67, -7.39) * mm, "end": v(27.82, -7.4) * mm});
            skLineSegment(sketch, "E2707", {"start": v(27.82, -7.4) * mm, "end": v(27.99, -7.39) * mm});
            skLineSegment(sketch, "E2708", {"start": v(27.99, -7.39) * mm, "end": v(28.16, -7.38) * mm});
            skLineSegment(sketch, "E2709", {"start": v(28.16, -7.38) * mm, "end": v(28.35, -7.37) * mm});
            skLineSegment(sketch, "E2710", {"start": v(28.35, -7.37) * mm, "end": v(28.55, -7.36) * mm});
            skLineSegment(sketch, "E2711", {"start": v(28.55, -7.36) * mm, "end": v(28.76, -7.33) * mm});
            skLineSegment(sketch, "E2712", {"start": v(28.76, -7.33) * mm, "end": v(28.98, -7.3) * mm});
            skLineSegment(sketch, "E2713", {"start": v(28.98, -7.3) * mm, "end": v(29.22, -7.28) * mm});
            skLineSegment(sketch, "E2714", {"start": v(29.22, -7.28) * mm, "end": v(29.46, -7.23) * mm});
            skLineSegment(sketch, "E2715", {"start": v(29.46, -7.23) * mm, "end": v(29.66, -7.2) * mm});
            skSolve(sketch);
        }
        {
            var Q0;
            Q0=makeQuery(id+"F2.imprint","IMPRINT",FACE,{"disambiguationData":[TD([[makeQuery(id+"F2.imprint","IMPRINT",EDGE,{"derivedFrom":sQuery(id+"F2.wireOp",EDGE,"E346")}),1.0]])]});
            var Q1;
            Q1=makeQuery(id+"F2.imprint","IMPRINT",FACE,{"disambiguationData":[TD([[makeQuery(id+"F2.imprint","IMPRINT",EDGE,{"derivedFrom":sQuery(id+"F2.wireOp",EDGE,"E345")}),-1.0]])]});
            extrude(context, id + "F3", {"entities" : qUnion([Q0, Q1]), "operationType" : NewBodyOperationType.ADD, "depth" : 3 * mm});
        }
    });
